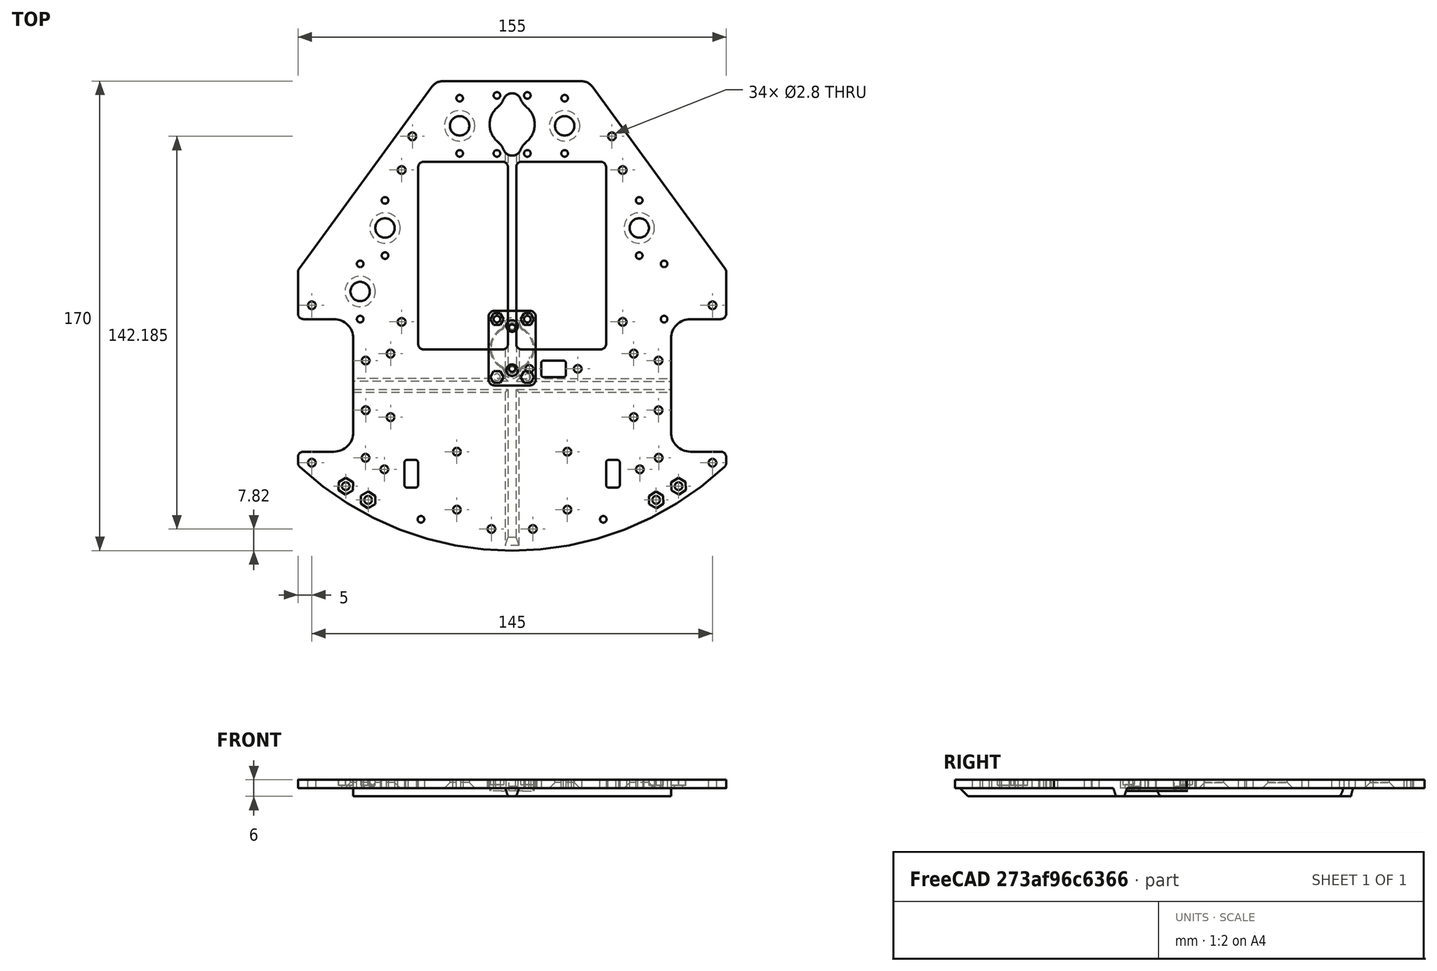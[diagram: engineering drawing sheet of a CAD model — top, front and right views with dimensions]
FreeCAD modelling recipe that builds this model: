
FCSTD DOCUMENT  (FreeCAD 0.19R24276 (Git))
Label: PB3D_TriPlate_Base
License: All rights reserved
LicenseURL: http://en.wikipedia.org/wiki/All_rights_reserved
objects: Sketcher::SketchObject×37, PartDesign::Pocket×23, PartDesign::Pad×5, PartDesign::Plane×5, PartDesign::SubtractiveLoft×4, PartDesign::Body×3, App::Part×3, Mesh::Feature×2, Spreadsheet::Sheet×1, PartDesign::Chamfer×1
note: 111 computed .brp shape members not serialized (recipe doc carries the construction recipe); baked Part::Feature solids carry a one-line shape summary decoded from their .brp

FEATURE [Sketcher::SketchObject] Sketch  label="Sketch_MainPlate"
  FullyConstrained = true
  MapMode = 5
  Support = -> [XY_Plane001]
  expr: Constraints[40] = <<params>>.plate_length
  expr: Constraints[65] = <<params>>.std_rad
  expr: Constraints[42] = <<params>>.tail_width
  expr: Constraints[78] = <<params>>.wheel_well_clearance
  expr: Constraints[79] = <<params>>.plate_width
  expr: Constraints[36] = <<params>>.wheel_well_plate_width
  expr: Constraints[47] = <<params>>.front_diameter
  expr: Constraints[63] = <<params>>.std_rad
  expr: Constraints[76] = <<params>>.front_vert_edge
  expr: Constraints[77] = <<params>>.back_vert_edge
  expr: Constraints[80] = <<params>>.std_rad
  expr: Constraints[81] = <<params>>.std_rad
  expr: Constraints[41] = <<params>>.tail_rad
  sketch-geometry (34):
    g0: LineSegment StartX=-57.5 StartY=17 StartZ=0 EndX=-57.5 EndY=-17 EndZ=0
    g1: LineSegment StartX=57.5 StartY=17 StartZ=0 EndX=57.5 EndY=-17 EndZ=0
    g2: LineSegment StartX=-57.5 StartY=0 StartZ=0 EndX=57.5 EndY=0 EndZ=0
    g3: LineSegment StartX=-64.5 StartY=-24 StartZ=0 EndX=64.5 EndY=-24 EndZ=0
    g4: LineSegment StartX=-64.5 StartY=24 StartZ=0 EndX=64.5 EndY=24 EndZ=0
    g5: LineSegment StartX=-64.5 StartY=-24 StartZ=0 EndX=-75.5 EndY=-24 EndZ=0
    g6: LineSegment StartX=64.5 StartY=-24 StartZ=0 EndX=75.5 EndY=-24 EndZ=0
    g7: ArcOfCircle CenterX=0 CenterY=52.6846 CenterZ=0 NormalX=0 NormalY=0 NormalZ=1 AngleXU=0 Radius=112.5 StartAngle=3.96017 EndAngle=5.4646
    g8: LineSegment StartX=-64.5 StartY=24 StartZ=0 EndX=-75.5 EndY=24 EndZ=0
    g9: LineSegment StartX=64.5 StartY=24 StartZ=0 EndX=75.5 EndY=24 EndZ=0
    g10: LineSegment StartX=-77.1162 StartY=42.1781 StartZ=0 EndX=-29.0404 EndY=108.13 EndZ=0
    g11: LineSegment StartX=-25 StartY=110.185 StartZ=0 EndX=25 EndY=110.185 EndZ=0
    g12: LineSegment StartX=29.0404 StartY=108.13 StartZ=0 EndX=77.1162 EndY=42.1781 EndZ=0
    g13: LineSegment StartX=0 StartY=0 StartZ=0 EndX=0 EndY=110.185 EndZ=0
    g14: ArcOfCircle CenterX=-25 CenterY=105.185 CenterZ=0 NormalX=0 NormalY=0 NormalZ=1 AngleXU=0 Radius=5 StartAngle=1.5708 EndAngle=2.5117
    g15: ArcOfCircle CenterX=25 CenterY=105.185 CenterZ=0 NormalX=0 NormalY=0 NormalZ=1 AngleXU=0 Radius=5 StartAngle=0.629894 EndAngle=1.5708
    g16: ArcOfCircle CenterX=-64.5 CenterY=17 CenterZ=0 NormalX=0 NormalY=0 NormalZ=1 AngleXU=0 Radius=7 StartAngle=0 EndAngle=1.5708
    g17: ArcOfCircle CenterX=-64.5 CenterY=-17 CenterZ=0 NormalX=0 NormalY=0 NormalZ=1 AngleXU=0 Radius=7 StartAngle=4.71239 EndAngle=6.28319
    g18: ArcOfCircle CenterX=64.5 CenterY=-17 CenterZ=0 NormalX=0 NormalY=0 NormalZ=1 AngleXU=0 Radius=7 StartAngle=3.14159 EndAngle=4.71239
    g19: ArcOfCircle CenterX=64.5 CenterY=17 CenterZ=0 NormalX=0 NormalY=0 NormalZ=1 AngleXU=0 Radius=7 StartAngle=1.5708 EndAngle=3.14159
    g20: GeomPoint X=0 Y=-59.8154 Z=0
    g21: Circle CenterX=0 CenterY=52.6846 CenterZ=0 NormalX=0 NormalY=0 NormalZ=1 AngleXU=0 Radius=112.5
    g22: LineSegment StartX=77.5 StartY=26 StartZ=0 EndX=77.5 EndY=41 EndZ=0
    g23: LineSegment StartX=77.5 StartY=-26 StartZ=0 EndX=77.5 EndY=-28 EndZ=0
    g24: LineSegment StartX=-77.5 StartY=-28 StartZ=0 EndX=-77.5 EndY=-26 EndZ=0
    g25: LineSegment StartX=-77.5 StartY=26 StartZ=0 EndX=-77.5 EndY=41 EndZ=0
    g26: ArcOfCircle CenterX=75.5 CenterY=-28 CenterZ=0 NormalX=0 NormalY=0 NormalZ=1 AngleXU=0 Radius=2 StartAngle=5.4646 EndAngle=6.28319
    g27: ArcOfCircle CenterX=75.5 CenterY=-26 CenterZ=0 NormalX=0 NormalY=0 NormalZ=1 AngleXU=0 Radius=2 StartAngle=-9e-16 EndAngle=1.5708
    g28: ArcOfCircle CenterX=-75.5 CenterY=-28 CenterZ=0 NormalX=0 NormalY=0 NormalZ=1 AngleXU=0 Radius=2 StartAngle=3.14159 EndAngle=3.96017
    g29: ArcOfCircle CenterX=-75.5 CenterY=-26 CenterZ=0 NormalX=0 NormalY=0 NormalZ=1 AngleXU=0 Radius=2 StartAngle=1.5708 EndAngle=3.14159
    g30: ArcOfCircle CenterX=75.5 CenterY=26 CenterZ=0 NormalX=0 NormalY=0 NormalZ=1 AngleXU=0 Radius=2 StartAngle=4.71239 EndAngle=6.28319
    g31: ArcOfCircle CenterX=75.5 CenterY=41 CenterZ=0 NormalX=0 NormalY=0 NormalZ=1 AngleXU=0 Radius=2 StartAngle=-7.1e-15 EndAngle=0.629894
    g32: ArcOfCircle CenterX=-75.5 CenterY=26 CenterZ=0 NormalX=0 NormalY=0 NormalZ=1 AngleXU=0 Radius=2 StartAngle=3.14159 EndAngle=4.71239
    g33: ArcOfCircle CenterX=-75.5 CenterY=41 CenterZ=0 NormalX=0 NormalY=0 NormalZ=1 AngleXU=0 Radius=2 StartAngle=2.5117 EndAngle=3.14159
  constraints (82):
    c: Vertical(g0)
    c: Vertical(g1)
    c: Horizontal(g2)
    c: Symmetric(g2,g2,g-1)
    c: Horizontal(g3)
    c: Horizontal(g5)
    c: Horizontal(g6)
    c: PointOnObject(g7,g-2)
    c: Horizontal(g8)
    c: Horizontal(g9)
    c: Horizontal(g11)
    c: Coincident(g13,g-1)
    c: PointOnObject(g13,g-2)
    c: Tangent(g10,g14) = 1.5708
    c: Tangent(g11,g14) = 1.5708
    c: Tangent(g11,g15) = 1.5708
    c: Tangent(g12,g15) = 1.5708
    c: Tangent(g8,g16) = -1.5708
    c: Tangent(g0,g16) = 1.5708
    c: Tangent(g5,g17) = 1.5708
    c: Tangent(g0,g17) = 1.5708
    c: Tangent(g1,g18) = -1.5708
    c: Tangent(g6,g18) = -1.5708
    c: Tangent(g1,g19) = -1.5708
    c: Tangent(g9,g19) = 1.5708
    c: Equal(g15,g14)
    c: Symmetric(g11,g11,g13)
    c: Equal(g18,g19)
    c: Equal(g19,g16)
    c: Equal(g16,g17)
    c: PointOnObject(g20,g-2)
    c: PointOnObject(g20,g7)
    c: Coincident(g4,g8)
    c: Coincident(g4,g9)
    c: Coincident(g3,g6)
    c: Coincident(g3,g5)
    c: DistanceX(g2,g2) = 115
    c: Symmetric(g0,g0,g2)
    c: Symmetric(g1,g1,g2)
    c: Radius(g19) = 7
    c: DistanceY(g20,g11) = 170
    c: Radius(g15) = 5
    c: DistanceX(g11,g11) = 50
    c: Equal(g9,g8)
    c: Equal(g9,g6)
    c: Coincident(g21,g7)
    c: PointOnObject(g20,g21)
    c: Diameter(g21) = 225
    c: Vertical(g22)
    c: Vertical(g23)
    c: Vertical(g24)
    c: Vertical(g25)
    c: Equal(g5,g8)
    c: Equal(g10,g12)
    c: Tangent(g7,g26) = -1.5708
    c: Tangent(g23,g26) = 1.5708
    c: Tangent(g23,g27) = 1.5708
    c: Tangent(g6,g27) = 1.5708
    c: Tangent(g7,g28) = -1.5708
    c: Tangent(g24,g28) = 1.5708
    c: Tangent(g24,g29) = 1.5708
    c: Tangent(g5,g29) = -1.5708
    c: Equal(g29,g27)
    c: Radius(g27) = 2
    c: Equal(g26,g28)
    c: Radius(g26) = 2
    c: Tangent(g9,g30) = -1.5708
    c: Tangent(g22,g30) = -1.5708
    c: Tangent(g22,g31) = -1.5708
    c: Tangent(g12,g31) = 1.5708
    c: Tangent(g8,g32) = 1.5708
    c: Tangent(g25,g32) = 1.5708
    c: Tangent(g10,g33) = 1.5708
    c: Tangent(g25,g33) = 1.5708
    c: Equal(g30,g32)
    c: Equal(g31,g33)
    c: DistanceY(g23,g23) = 2
    c: DistanceY(g22,g22) = 15
    c: DistanceY(g6,g9) = 48
    c: DistanceX(g24,g23) = 155
    c: Radius(g30) = 2
    c: Radius(g31) = 2
FEATURE [PartDesign::Pad] Pad  label="MainPlateExt"
  Direction = (1,1,1)
  Length = 6
  Length2 = 100
  Profile = -> Sketch
  Reversed = true
  Type = 0
  expr: Length = <<params>>.plate_thick + <<params>>.rib_thick
FEATURE [Spreadsheet::Sheet] Spreadsheet  label="params"
  cells = A1=Std Tol; B1(std_tol_clear)==0.3mm; A2=Bottom Plate Main Params; E2=Grove Board Mts; F2=X; G2=Y; I2=M2 Bolt Clearances; K2=M2.5 Bolt Clearances; A3=Plate Length; B3(plate_length)==170mm; C3=Mot Brac Hole Space L; D3(mot_brac_hole_space_l)==18mm; E3=LED 1; F3(grove_led_mood_x)==19mm; G3(grove_led_mood_y)==94mm; I3=Hole Clear Diam; J3(m2_hole_clear_diam)==2.4mm; K3=Hole Clear Diam; L3(m25_hole_clear_diam)==2.8mm; A4=Plate Width; B4(plate_width)==155mm; C4=Mot Brac Hole Space W; D4(mot_brac_hole_space_w)==wheel_well_plate_width - 2 * mot_brac_hole_offset_w; E4=LED 2; F4(grove_led_task_x)==46mm; G4(grove_led_task_y)==57mm; I4=Head Clear Diam; J4(m2_head_clear_diam)==4.2mm; K4=Head Clear Diam; L4(m25_head_clear_diam)==5mm; A5=Front Diameter; B5(front_diameter)==225mm; C5=Mot Brac Hole Offset W; D5(mot_brac_hole_offset_w)==4.5mm; E5=LSR/VIB; F5(grove_viblsr_x)==55mm; G5(grove_viblsr_y)==34mm; I5=Head Min Depth; J5(m2_head_min_depth)==1.3mm; K5=Head Min Depth; L5(m25_head_min_depth)==1.6mm; A6=Tail Width; B6(tail_width)==50mm; C6=Mot Ret Hole Space L; D6(mot_ret_hole_space_l)==23mm; I6=Nut Clear Flat; J6(m2_nut_clear_flat)==4.2mm; K6=Nut Clear Flat; L6(m25_nut_clear_flat)==5.2mm; A7=Plate Thickness; B7(plate_thick)==3mm; C7=Mot Ret Hole Space W; D7(mot_ret_hole_space_w)==wheel_well_plate_width - 2 * mot_ret_hole_offset_w; E7=BallCast Mt; G7=Shell Mts; I7=Nut Min Depth; J7(m2_nut_min_depth)==1.75mm; K7=Nut Min Depth; L7(m25_nut_min_depth)==2mm; C8=Mot Ret Hole Offset W; D8(mot_ret_hole_offset_w)==13.5mm; E8=BallC Mt L; F8(ballc_mt_l)==27mm; G8=ShellToBot FrMid Offset; H8(shelltobot_frontmid_offset_xy)==5mm; A9=Front Vert. Edge; B9(front_vert_edge)==2mm; E9=BallC Mt W; F9(ballc_mt_w)==17mm; G9=ShellToBot Back Offset X; H9(shelltobot_back_offset_x)==6mm; A10=Back Vert. Edge; B10(back_vert_edge)==15mm; E10=BallC Mt thick; F10(ballc_mt_t)==3mm; G10=ShellToBot Back Offset Y; H10(shelltobot_back_offset_y)==20mm; C11=BatB Cent Offset; D11(batb_cent_offset)==13mm; E11=BallC Mt Hole Space; F11(ballc_mt_holespace)==14.7mm; A12=Std. Radius; B12(std_rad)==2mm; C12=BatB Hole L; D12(batb_hole_l)==68mm; E12=BallC To Plate Offset; F12(ballc_to_plate_offset)==3mm; G12=US and LSR Mts; A13=Wheel Well Radius; B13(wheel_well_rad)==7mm; C13=BatB Hole W; D13(batb_hole_w)==64mm; E13=BallC To Plate L; F13(ballc_to_plate_l)==ballc_mt_l - 2 * ballc_to_plate_offset; G13=USR Mt Width; H13(usr_mt_width)==40mm; A14=Tail Radius; B14(tail_rad)==5mm; C14=BatB Mt L; D14(batb_mt_l)==55mm; E14=BallC To Plate W; F14(ballc_to_plate_w)==ballc_mt_w - 2 * ballc_to_plate_offset; G14=USR Mt Leng; H14(usr_mt_leng)==21mm; C15=BatB Mt W; D15(batb_mt_w)==80mm; E15=BallC Mt Thick Offset; F15(ballc_mt_thick_inset)==1mm; G15=USR Mt Loc X; H15(usr_mt_loc_x)==24mm; A16=Wheel Well Plate Width; B16(wheel_well_plate_width)==115mm; C16=BatB Mt Offset; D16(batb_mt_offset)==23mm; E16=BMPR Mts; G16=LSR Mt Width; H16(lsr_mt_width)==8mm; A17=Wheel Well Clearance; B17(wheel_well_clearance)==48mm; E17=BMPR Switch Hole Space; F17(bmpr_switch_hole_space)==9.5mm; G17=LSR Mt Diam Offset; H17(lsr_mt_diam_offset)==17.5mm; A18=Wheel Well Vert; B18(wheel_well_vert)==7mm; C18=Plate BallC Hole Loc L; D18(plate_ballc_hole_loc_l)==94.5mm; E18=BMPR Switch Diam Offset; F18(bmpr_switch_diam_offset)==5mm; G18=PWR Switch; E19=BMPR Switch Ang; F19(bmpr_switch_ang)=31.5; G19=PWR S Loc X; H19(pwrs_loc_x)==15mm; A20=Stiffeners; E20=BMPR Hole Diam; F20(bmpe_hole_diam)==3mm; G20=PWR S Loc Y; H20(pwrs_loc_y)==6mm; A21=Plate Rib Thickness; B21(rib_thick)==3mm; E21=BMPR Standoff Hole Width; F21(bmpr_standoff_hole_width)==66mm; G21=PWR S Slot Width; H21(pwrs_slot_w)==6mm; A22=Plate Rib Width Min; B22(rib_width_min)==3mm; E22=BMPR Standoff Hole Loc X; F22(bmpr_standoff_hole_loc_x)==48.5mm; G22=PWR S Slot Leng; H22(pwrs_slot_leng)==9mm; A23=Plate Rib Width Max; B23(rib_width_max)==5mm; E23=BMPR Pivot Hole Loc X; F23(bmpr_pivot_hole_loc_x)==52mm; G23=PWR S Slot Rad; H23(pwrs_slot_rad)==1mm; A24=Trim Front Rib Loc; B24(rib_trim_loc_front)==58mm; E24=BMPR Pivot Hole Spacing; F24(bmpr_pivot_hole_width)==15mm; G24=PWR S Hole Spacing; H24(pwrs_hole_spacing)==17.5mm; E26=BMPR Grove Hole Spacing Width; F26(bmpr_grove_hole_spacing_width)==68mm; E27=BMPR Grove Hole Loc X; F27(bmpr_grove_hole_loc_x)==32mm; E28=BMPR Grove Hole Width; F28(bmpr_grove_hole_width)==5mm; E29=BMPR Grove Hole Leng; F29(bmpr_grove_hole_leng)==10mm
FEATURE [Sketcher::SketchObject] Sketch016  label="Sketch_MainPlate_Temp"
  FullyConstrained = true
  MapMode = 5
  Support = -> [XY_Plane001]
  expr: Constraints[36] = <<params>>.tail_rad
  expr: Constraints[55] = <<params>>.std_rad
  expr: Constraints[70] = <<params>>.wheel_well_clearance
  expr: Constraints[68] = <<params>>.front_vert_edge
  expr: Constraints[72] = <<params>>.std_rad
  expr: Constraints[57] = <<params>>.std_rad
  expr: Constraints[73] = <<params>>.std_rad
  expr: Constraints[35] = <<params>>.plate_length
  expr: Constraints[37] = <<params>>.tail_width
  expr: Constraints[31] = <<params>>.wheel_well_plate_width
  expr: Constraints[71] = <<params>>.plate_width
  expr: Constraints[69] = <<params>>.back_vert_edge
  expr: Constraints[74] = <<params>>.front_diameter
  sketch-geometry (31):
    g0: LineSegment StartX=-57.5 StartY=17 StartZ=0 EndX=-57.5 EndY=-17 EndZ=0
    g1: LineSegment StartX=57.5 StartY=17 StartZ=0 EndX=57.5 EndY=-17 EndZ=0
    g2: LineSegment StartX=-57.5 StartY=0 StartZ=0 EndX=57.5 EndY=0 EndZ=0
    g3: LineSegment StartX=-64.5 StartY=-24 StartZ=0 EndX=-75.5 EndY=-24 EndZ=0
    g4: LineSegment StartX=64.5 StartY=-24 StartZ=0 EndX=75.5 EndY=-24 EndZ=0
    g5: ArcOfCircle CenterX=0 CenterY=52.6846 CenterZ=0 NormalX=0 NormalY=0 NormalZ=1 AngleXU=0 Radius=112.5 StartAngle=3.96017 EndAngle=5.4646
    g6: LineSegment StartX=-64.5 StartY=24 StartZ=0 EndX=-75.5 EndY=24 EndZ=0
    g7: LineSegment StartX=64.5 StartY=24 StartZ=0 EndX=75.5 EndY=24 EndZ=0
    g8: LineSegment StartX=-77.1162 StartY=42.1781 StartZ=0 EndX=-29.0404 EndY=108.13 EndZ=0
    g9: LineSegment StartX=-25 StartY=110.185 StartZ=0 EndX=25 EndY=110.185 EndZ=0
    g10: LineSegment StartX=29.0404 StartY=108.13 StartZ=0 EndX=77.1162 EndY=42.1781 EndZ=0
    g11: LineSegment StartX=0 StartY=0 StartZ=0 EndX=0 EndY=110.185 EndZ=0
    g12: ArcOfCircle CenterX=-25 CenterY=105.185 CenterZ=0 NormalX=0 NormalY=0 NormalZ=1 AngleXU=0 Radius=5 StartAngle=1.5708 EndAngle=2.5117
    g13: ArcOfCircle CenterX=25 CenterY=105.185 CenterZ=0 NormalX=0 NormalY=0 NormalZ=1 AngleXU=0 Radius=5 StartAngle=0.629894 EndAngle=1.5708
    g14: ArcOfCircle CenterX=-64.5 CenterY=17 CenterZ=0 NormalX=0 NormalY=0 NormalZ=1 AngleXU=0 Radius=7 StartAngle=0 EndAngle=1.5708
    g15: ArcOfCircle CenterX=-64.5 CenterY=-17 CenterZ=0 NormalX=0 NormalY=0 NormalZ=1 AngleXU=0 Radius=7 StartAngle=4.71239 EndAngle=6.28319
    g16: ArcOfCircle CenterX=64.5 CenterY=-17 CenterZ=0 NormalX=0 NormalY=0 NormalZ=1 AngleXU=0 Radius=7 StartAngle=3.14159 EndAngle=4.71239
    g17: ArcOfCircle CenterX=64.5 CenterY=17 CenterZ=0 NormalX=0 NormalY=0 NormalZ=1 AngleXU=0 Radius=7 StartAngle=1.5708 EndAngle=3.14159
    g18: GeomPoint X=0 Y=-59.8154 Z=0
    g19: LineSegment StartX=77.5 StartY=26 StartZ=0 EndX=77.5 EndY=41 EndZ=0
    g20: LineSegment StartX=77.5 StartY=-26 StartZ=0 EndX=77.5 EndY=-28 EndZ=0
    g21: LineSegment StartX=-77.5 StartY=-28 StartZ=0 EndX=-77.5 EndY=-26 EndZ=0
    g22: LineSegment StartX=-77.5 StartY=26 StartZ=0 EndX=-77.5 EndY=41 EndZ=0
    g23: ArcOfCircle CenterX=75.5 CenterY=-28 CenterZ=0 NormalX=0 NormalY=0 NormalZ=1 AngleXU=0 Radius=2 StartAngle=5.4646 EndAngle=6.28319
    g24: ArcOfCircle CenterX=75.5 CenterY=-26 CenterZ=0 NormalX=0 NormalY=0 NormalZ=1 AngleXU=0 Radius=2 StartAngle=-9e-16 EndAngle=1.5708
    g25: ArcOfCircle CenterX=-75.5 CenterY=-28 CenterZ=0 NormalX=0 NormalY=0 NormalZ=1 AngleXU=0 Radius=2 StartAngle=3.14159 EndAngle=3.96017
    g26: ArcOfCircle CenterX=-75.5 CenterY=-26 CenterZ=0 NormalX=0 NormalY=0 NormalZ=1 AngleXU=0 Radius=2 StartAngle=1.5708 EndAngle=3.14159
    g27: ArcOfCircle CenterX=75.5 CenterY=26 CenterZ=0 NormalX=0 NormalY=0 NormalZ=1 AngleXU=0 Radius=2 StartAngle=4.71239 EndAngle=6.28319
    g28: ArcOfCircle CenterX=75.5 CenterY=41 CenterZ=0 NormalX=0 NormalY=0 NormalZ=1 AngleXU=0 Radius=2 StartAngle=-7.1e-15 EndAngle=0.629894
    g29: ArcOfCircle CenterX=-75.5 CenterY=26 CenterZ=0 NormalX=0 NormalY=0 NormalZ=1 AngleXU=0 Radius=2 StartAngle=3.14159 EndAngle=4.71239
    g30: ArcOfCircle CenterX=-75.5 CenterY=41 CenterZ=0 NormalX=0 NormalY=0 NormalZ=1 AngleXU=0 Radius=2 StartAngle=2.5117 EndAngle=3.14159
  constraints (76):
    c: Vertical(g0)
    c: Vertical(g1)
    c: Horizontal(g2)
    c: Symmetric(g2,g2,g-1)
    c: Horizontal(g3)
    c: Horizontal(g4)
    c: PointOnObject(g5,g-2)
    c: Horizontal(g6)
    c: Horizontal(g7)
    c: Horizontal(g9)
    c: Coincident(g11,g-1)
    c: PointOnObject(g11,g-2)
    c: Tangent(g8,g12) = 1.5708
    c: Tangent(g9,g12) = 1.5708
    c: Tangent(g9,g13) = 1.5708
    c: Tangent(g10,g13) = 1.5708
    c: Tangent(g6,g14) = -1.5708
    c: Tangent(g0,g14) = 1.5708
    c: Tangent(g3,g15) = 1.5708
    c: Tangent(g0,g15) = 1.5708
    c: Tangent(g1,g16) = -1.5708
    c: Tangent(g4,g16) = -1.5708
    c: Tangent(g1,g17) = -1.5708
    c: Tangent(g7,g17) = 1.5708
    c: Equal(g13,g12)
    c: Symmetric(g9,g9,g11)
    c: Equal(g16,g17)
    c: Equal(g17,g14)
    c: Equal(g14,g15)
    c: PointOnObject(g18,g-2)
    c: PointOnObject(g18,g5)
    c: DistanceX(g2,g2) = 115
    c: Symmetric(g0,g0,g2)
    c: Symmetric(g1,g1,g2)
    c: Radius(g17) = 7
    c: DistanceY(g18,g9) = 170
    c: Radius(g13) = 5
    c: DistanceX(g9,g9) = 50
    c: Equal(g7,g6)
    c: Equal(g7,g4)
    c: Vertical(g19)
    c: Vertical(g20)
    c: Vertical(g21)
    c: Vertical(g22)
    c: Equal(g3,g6)
    c: Equal(g8,g10)
    c: Tangent(g5,g23) = -1.5708
    c: Tangent(g20,g23) = 1.5708
    c: Tangent(g20,g24) = 1.5708
    c: Tangent(g4,g24) = 1.5708
    c: Tangent(g5,g25) = -1.5708
    c: Tangent(g21,g25) = 1.5708
    c: Tangent(g21,g26) = 1.5708
    c: Tangent(g3,g26) = -1.5708
    c: Equal(g26,g24)
    c: Radius(g24) = 2
    c: Equal(g23,g25)
    c: Radius(g23) = 2
    c: Tangent(g7,g27) = -1.5708
    c: Tangent(g19,g27) = -1.5708
    c: Tangent(g19,g28) = -1.5708
    c: Tangent(g10,g28) = 1.5708
    c: Tangent(g6,g29) = 1.5708
    c: Tangent(g22,g29) = 1.5708
    c: Tangent(g8,g30) = 1.5708
    c: Tangent(g22,g30) = 1.5708
    c: Equal(g27,g29)
    c: Equal(g28,g30)
    c: DistanceY(g20,g20) = 2
    c: DistanceY(g19,g19) = 15
    c: DistanceY(g4,g7) = 48
    c: DistanceX(g21,g20) = 155
    c: Radius(g27) = 2
    c: Radius(g28) = 2
    c: Diameter(g5) = 225
    c: Equal(g21,g20)
FEATURE [Sketcher::SketchObject] Sketch017  label="Sketch_BatBoxCut"
  FullyConstrained = true
  MapMode = 5
  Support = -> [XY_Plane001]
  expr: Constraints[121] = Spreadsheet.rib_width_min
  expr: Constraints[87] = <<params>>.std_rad
  expr: Constraints[71] = <<params>>.plate_width
  expr: Constraints[69] = <<params>>.back_vert_edge
  expr: Constraints[120] = <<params>>.batb_hole_l
  expr: Constraints[72] = <<params>>.std_rad
  expr: Constraints[57] = <<params>>.std_rad
  expr: Constraints[37] = <<params>>.tail_width
  expr: Constraints[88] = <<params>>.batb_hole_w
  expr: Constraints[35] = <<params>>.plate_length
  expr: Constraints[89] = <<params>>.batb_cent_offset
  expr: Constraints[74] = <<params>>.front_diameter
  expr: Constraints[31] = <<params>>.wheel_well_plate_width
  expr: Constraints[73] = <<params>>.std_rad
  expr: Constraints[68] = <<params>>.front_vert_edge
  expr: Constraints[70] = <<params>>.wheel_well_clearance
  expr: Constraints[55] = <<params>>.std_rad
  expr: Constraints[36] = <<params>>.tail_rad
  sketch-geometry (50):
    g0: LineSegment StartX=-57.5 StartY=17 StartZ=0 EndX=-57.5 EndY=-17 EndZ=0
    g1: LineSegment StartX=57.5 StartY=17 StartZ=0 EndX=57.5 EndY=-17 EndZ=0
    g2: LineSegment StartX=-57.5 StartY=0 StartZ=0 EndX=57.5 EndY=0 EndZ=0
    g3: LineSegment StartX=-64.5 StartY=-24 StartZ=0 EndX=-75.5 EndY=-24 EndZ=0
    g4: LineSegment StartX=64.5 StartY=-24 StartZ=0 EndX=75.5 EndY=-24 EndZ=0
    g5: ArcOfCircle CenterX=0 CenterY=52.6846 CenterZ=0 NormalX=0 NormalY=0 NormalZ=1 AngleXU=0 Radius=112.5 StartAngle=3.96017 EndAngle=5.4646
    g6: LineSegment StartX=-64.5 StartY=24 StartZ=0 EndX=-75.5 EndY=24 EndZ=0
    g7: LineSegment StartX=64.5 StartY=24 StartZ=0 EndX=75.5 EndY=24 EndZ=0
    g8: LineSegment StartX=-77.1162 StartY=42.1781 StartZ=0 EndX=-29.0404 EndY=108.13 EndZ=0
    g9: LineSegment StartX=-25 StartY=110.185 StartZ=0 EndX=25 EndY=110.185 EndZ=0
    g10: LineSegment StartX=29.0404 StartY=108.13 StartZ=0 EndX=77.1162 EndY=42.1781 EndZ=0
    g11: LineSegment StartX=0 StartY=0 StartZ=0 EndX=0 EndY=110.185 EndZ=0
    g12: ArcOfCircle CenterX=-25 CenterY=105.185 CenterZ=0 NormalX=0 NormalY=0 NormalZ=1 AngleXU=0 Radius=5 StartAngle=1.5708 EndAngle=2.5117
    g13: ArcOfCircle CenterX=25 CenterY=105.185 CenterZ=0 NormalX=0 NormalY=0 NormalZ=1 AngleXU=0 Radius=5 StartAngle=0.629894 EndAngle=1.5708
    g14: ArcOfCircle CenterX=-64.5 CenterY=17 CenterZ=0 NormalX=0 NormalY=0 NormalZ=1 AngleXU=0 Radius=7 StartAngle=0 EndAngle=1.5708
    g15: ArcOfCircle CenterX=-64.5 CenterY=-17 CenterZ=0 NormalX=0 NormalY=0 NormalZ=1 AngleXU=0 Radius=7 StartAngle=4.71239 EndAngle=6.28319
    g16: ArcOfCircle CenterX=64.5 CenterY=-17 CenterZ=0 NormalX=0 NormalY=0 NormalZ=1 AngleXU=0 Radius=7 StartAngle=3.14159 EndAngle=4.71239
    g17: ArcOfCircle CenterX=64.5 CenterY=17 CenterZ=0 NormalX=0 NormalY=0 NormalZ=1 AngleXU=0 Radius=7 StartAngle=1.5708 EndAngle=3.14159
    g18: GeomPoint X=0 Y=-59.8154 Z=0
    g19: LineSegment StartX=77.5 StartY=26 StartZ=0 EndX=77.5 EndY=41 EndZ=0
    g20: LineSegment StartX=77.5 StartY=-26 StartZ=0 EndX=77.5 EndY=-28 EndZ=0
    g21: LineSegment StartX=-77.5 StartY=-28 StartZ=0 EndX=-77.5 EndY=-26 EndZ=0
    g22: LineSegment StartX=-77.5 StartY=26 StartZ=0 EndX=-77.5 EndY=41 EndZ=0
    g23: ArcOfCircle CenterX=75.5 CenterY=-28 CenterZ=0 NormalX=0 NormalY=0 NormalZ=1 AngleXU=0 Radius=2 StartAngle=5.4646 EndAngle=6.28319
    g24: ArcOfCircle CenterX=75.5 CenterY=-26 CenterZ=0 NormalX=0 NormalY=0 NormalZ=1 AngleXU=0 Radius=2 StartAngle=-9e-16 EndAngle=1.5708
    g25: ArcOfCircle CenterX=-75.5 CenterY=-28 CenterZ=0 NormalX=0 NormalY=0 NormalZ=1 AngleXU=0 Radius=2 StartAngle=3.14159 EndAngle=3.96017
    g26: ArcOfCircle CenterX=-75.5 CenterY=-26 CenterZ=0 NormalX=0 NormalY=0 NormalZ=1 AngleXU=0 Radius=2 StartAngle=1.5708 EndAngle=3.14159
    g27: ArcOfCircle CenterX=75.5 CenterY=26 CenterZ=0 NormalX=0 NormalY=0 NormalZ=1 AngleXU=0 Radius=2 StartAngle=4.71239 EndAngle=6.28319
    g28: ArcOfCircle CenterX=75.5 CenterY=41 CenterZ=0 NormalX=0 NormalY=0 NormalZ=1 AngleXU=0 Radius=2 StartAngle=-9e-16 EndAngle=0.629894
    g29: ArcOfCircle CenterX=-75.5 CenterY=26 CenterZ=0 NormalX=0 NormalY=0 NormalZ=1 AngleXU=0 Radius=2 StartAngle=3.14159 EndAngle=4.71239
    g30: ArcOfCircle CenterX=-75.5 CenterY=41 CenterZ=0 NormalX=0 NormalY=0 NormalZ=1 AngleXU=0 Radius=2 StartAngle=2.5117 EndAngle=3.14159
    g31: LineSegment StartX=34 StartY=79 StartZ=0 EndX=34 EndY=15 EndZ=0
    g32: LineSegment StartX=-34 StartY=15 StartZ=0 EndX=-34 EndY=79 EndZ=0
    g33: LineSegment StartX=0 StartY=0 StartZ=0 EndX=0 EndY=13 EndZ=0
    g34: ArcOfCircle CenterX=-32 CenterY=15 CenterZ=0 NormalX=0 NormalY=0 NormalZ=1 AngleXU=0 Radius=2 StartAngle=3.14159 EndAngle=4.71239
    g35: ArcOfCircle CenterX=32 CenterY=15 CenterZ=0 NormalX=0 NormalY=0 NormalZ=1 AngleXU=0 Radius=2 StartAngle=4.71239 EndAngle=6.28319
    g36: ArcOfCircle CenterX=32 CenterY=79 CenterZ=0 NormalX=0 NormalY=0 NormalZ=1 AngleXU=0 Radius=2 StartAngle=1.7e-15 EndAngle=1.5708
    g37: ArcOfCircle CenterX=-32 CenterY=79 CenterZ=0 NormalX=0 NormalY=0 NormalZ=1 AngleXU=0 Radius=2 StartAngle=1.5708 EndAngle=3.14159
    g38: LineSegment StartX=-32 StartY=81 StartZ=0 EndX=-3.5 EndY=81 EndZ=0
    g39: LineSegment StartX=-1.5 StartY=79 StartZ=0 EndX=-1.5 EndY=15 EndZ=0
    g40: LineSegment StartX=-3.5 StartY=13 StartZ=0 EndX=-32 EndY=13 EndZ=0
    g41: LineSegment StartX=32 StartY=81 StartZ=0 EndX=3.5 EndY=81 EndZ=0
    g42: LineSegment StartX=1.5 StartY=79 StartZ=0 EndX=1.5 EndY=15 EndZ=0
    g43: LineSegment StartX=3.5 StartY=13 StartZ=0 EndX=32 EndY=13 EndZ=0
    g44: ArcOfCircle CenterX=-3.5 CenterY=79 CenterZ=0 NormalX=0 NormalY=0 NormalZ=1 AngleXU=0 Radius=2 StartAngle=-1.8e-15 EndAngle=1.5708
    g45: ArcOfCircle CenterX=3.5 CenterY=79 CenterZ=0 NormalX=0 NormalY=0 NormalZ=1 AngleXU=0 Radius=2 StartAngle=1.5708 EndAngle=3.14159
    g46: ArcOfCircle CenterX=3.5 CenterY=15 CenterZ=0 NormalX=0 NormalY=0 NormalZ=1 AngleXU=0 Radius=2 StartAngle=3.14159 EndAngle=4.71239
    g47: ArcOfCircle CenterX=-3.5 CenterY=15 CenterZ=0 NormalX=0 NormalY=0 NormalZ=1 AngleXU=0 Radius=2 StartAngle=4.71239 EndAngle=6.28319
    g48: LineSegment StartX=-3.5 StartY=79 StartZ=0 EndX=3.5 EndY=79 EndZ=0
    g49: LineSegment StartX=-3.5 StartY=15 StartZ=0 EndX=3.5 EndY=15 EndZ=0
  constraints (126):
    c: Vertical(g0)
    c: Vertical(g1)
    c: Horizontal(g2)
    c: Symmetric(g2,g2,g-1)
    c: Horizontal(g3)
    c: Horizontal(g4)
    c: PointOnObject(g5,g-2)
    c: Horizontal(g6)
    c: Horizontal(g7)
    c: Horizontal(g9)
    c: Coincident(g11,g-1)
    c: PointOnObject(g11,g-2)
    c: Tangent(g8,g12) = 1.5708
    c: Tangent(g9,g12) = 1.5708
    c: Tangent(g9,g13) = 1.5708
    c: Tangent(g10,g13) = 1.5708
    c: Tangent(g6,g14) = -1.5708
    c: Tangent(g0,g14) = 1.5708
    c: Tangent(g3,g15) = 1.5708
    c: Tangent(g0,g15) = 1.5708
    c: Tangent(g1,g16) = -1.5708
    c: Tangent(g4,g16) = -1.5708
    c: Tangent(g1,g17) = -1.5708
    c: Tangent(g7,g17) = 1.5708
    c: Equal(g13,g12)
    c: Symmetric(g9,g9,g11)
    c: Equal(g16,g17)
    c: Equal(g17,g14)
    c: Equal(g14,g15)
    c: PointOnObject(g18,g-2)
    c: PointOnObject(g18,g5)
    c: DistanceX(g2,g2) = 115
    c: Symmetric(g0,g0,g2)
    c: Symmetric(g1,g1,g2)
    c: Radius(g17) = 7
    c: DistanceY(g18,g9) = 170
    c: Radius(g13) = 5
    c: DistanceX(g9,g9) = 50
    c: Equal(g7,g6)
    c: Equal(g7,g4)
    c: Vertical(g19)
    c: Vertical(g20)
    c: Vertical(g21)
    c: Vertical(g22)
    c: Equal(g3,g6)
    c: Equal(g8,g10)
    c: Tangent(g5,g23) = -1.5708
    c: Tangent(g20,g23) = 1.5708
    c: Tangent(g20,g24) = 1.5708
    c: Tangent(g4,g24) = 1.5708
    c: Tangent(g5,g25) = -1.5708
    c: Tangent(g21,g25) = 1.5708
    c: Tangent(g21,g26) = 1.5708
    c: Tangent(g3,g26) = -1.5708
    c: Equal(g26,g24)
    c: Radius(g24) = 2
    c: Equal(g23,g25)
    c: Radius(g23) = 2
    c: Tangent(g7,g27) = -1.5708
    c: Tangent(g19,g27) = -1.5708
    c: Tangent(g19,g28) = -1.5708
    c: Tangent(g10,g28) = 1.5708
    c: Tangent(g6,g29) = 1.5708
    c: Tangent(g22,g29) = 1.5708
    c: Tangent(g8,g30) = 1.5708
    c: Tangent(g22,g30) = 1.5708
    c: Equal(g27,g29)
    c: Equal(g28,g30)
    c: DistanceY(g20,g20) = 2
    c: DistanceY(g19,g19) = 15
    c: DistanceY(g4,g7) = 48
    c: DistanceX(g21,g20) = 155
    c: Radius(g27) = 2
    c: Radius(g28) = 2
    c: Diameter(g5) = 225
    c: Equal(g21,g20)
    c: Vertical(g31)
    c: Vertical(g32)
    c: Coincident(g33,g11)
    c: Vertical(g33)
    c: Tangent(g32,g34) = 1.5708
    c: Tangent(g31,g35) = 1.5708
    c: Tangent(g31,g36) = 1.5708
    c: Tangent(g32,g37) = 1.5708
    c: Equal(g36,g37)
    c: Equal(g37,g34)
    c: Equal(g34,g35)
    c: Radius(g35) = 2
    c: DistanceX(g37,g36) = 64
    c: DistanceY(g-1,g33) = 13
    c: Coincident(g38,g37)
    c: Horizontal(g38)
    c: Vertical(g39)
    c: Coincident(g40,g34)
    c: Horizontal(g40)
    c: Coincident(g41,g36)
    c: Horizontal(g41)
    c: Vertical(g42)
    c: Coincident(g43,g35)
    c: Horizontal(g43)
    c: Tangent(g38,g44) = 1.5708
    c: Tangent(g39,g44) = 1.5708
    c: Tangent(g42,g45) = -1.5708
    c: Tangent(g41,g45) = -1.5708
    c: Tangent(g42,g46) = -1.5708
    c: Tangent(g43,g46) = -1.5708
    c: Tangent(g39,g47) = 1.5708
    c: Tangent(g40,g47) = 1.5708
    c: Coincident(g48,g44)
    c: Coincident(g48,g45)
    c: Coincident(g49,g47)
    c: Coincident(g49,g46)
    c: Horizontal(g49)
    c: Horizontal(g48)
    c: Equal(g36,g45)
    c: Equal(g45,g44)
    c: Equal(g46,g47)
    c: Equal(g43,g40)
    c: Equal(g35,g46)
    c: Symmetric(g34,g35,g33)
    c: DistanceY(g35,g36) = 68
    c: DistanceX(g39,g42) = 3
    c: Tangent(g40,g34)
    c: Tangent(g43,g35)
    c: Tangent(g36,g41)
    c: Tangent(g37,g38)
FEATURE [PartDesign::Pocket] Pocket003  label="BatBoxCut"
  BaseFeature = -> Pad
  Length = 5
  Length2 = 100
  Profile = -> Sketch017
  Type = 1
FEATURE [Sketcher::SketchObject] Sketch018  label="Sketch_MotBrackHoles"
  FullyConstrained = true
  MapMode = 5
  Support = -> [XY_Plane001]
  expr: Constraints[9] = <<params>>.mot_brac_hole_space_l
  expr: Constraints[10] = <<params>>.mot_brac_hole_space_w
  expr: Constraints[18] = <<params>>.m25_hole_clear_diam
  sketch-geometry (8):
    g0: LineSegment StartX=-53 StartY=9 StartZ=0 EndX=53 EndY=9 EndZ=0
    g1: LineSegment StartX=53 StartY=9 StartZ=0 EndX=53 EndY=-9 EndZ=0
    g2: LineSegment StartX=53 StartY=-9 StartZ=0 EndX=-53 EndY=-9 EndZ=0
    g3: LineSegment StartX=-53 StartY=-9 StartZ=0 EndX=-53 EndY=9 EndZ=0
    g4: Circle CenterX=53 CenterY=9 CenterZ=0 NormalX=0 NormalY=0 NormalZ=1 AngleXU=0 Radius=1.4
    g5: Circle CenterX=53 CenterY=-9 CenterZ=0 NormalX=0 NormalY=0 NormalZ=1 AngleXU=0 Radius=1.4
    g6: Circle CenterX=-53 CenterY=-9 CenterZ=0 NormalX=0 NormalY=0 NormalZ=1 AngleXU=0 Radius=1.4
    g7: Circle CenterX=-53 CenterY=9 CenterZ=0 NormalX=0 NormalY=0 NormalZ=1 AngleXU=0 Radius=1.4
  constraints (19):
    c: Coincident(g0,g1)
    c: Coincident(g1,g2)
    c: Coincident(g2,g3)
    c: Coincident(g3,g0)
    c: Horizontal(g0)
    c: Horizontal(g2)
    c: Vertical(g1)
    c: Vertical(g3)
    c: Symmetric(g2,g0,g-1)
    c: DistanceY(g1,g0) = 18
    c: DistanceX(g0,g0) = 106
    c: Coincident(g4,g0)
    c: Coincident(g5,g1)
    c: Coincident(g6,g2)
    c: Coincident(g7,g0)
    c: Equal(g7,g4)
    c: Equal(g4,g5)
    c: Equal(g5,g6)
    c: Diameter(g5) = 2.8
FEATURE [PartDesign::Pocket] Pocket  label="MotBracketHoles"
  BaseFeature = -> Pocket003
  Length = 5
  Length2 = 100
  Midplane = true
  Profile = -> Sketch018
  Type = 1
FEATURE [Sketcher::SketchObject] Sketch019  label="Sketch_MotRetHoles"
  FullyConstrained = true
  MapMode = 5
  Support = -> [XY_Plane001]
  expr: Constraints[9] = <<params>>.mot_ret_hole_space_l
  expr: Constraints[18] = <<params>>.m25_hole_clear_diam
  expr: Constraints[10] = <<params>>.mot_ret_hole_space_w
  sketch-geometry (8):
    g0: LineSegment StartX=-44 StartY=11.5 StartZ=0 EndX=44 EndY=11.5 EndZ=0
    g1: LineSegment StartX=44 StartY=11.5 StartZ=0 EndX=44 EndY=-11.5 EndZ=0
    g2: LineSegment StartX=44 StartY=-11.5 StartZ=0 EndX=-44 EndY=-11.5 EndZ=0
    g3: LineSegment StartX=-44 StartY=-11.5 StartZ=0 EndX=-44 EndY=11.5 EndZ=0
    g4: Circle CenterX=-44 CenterY=11.5 CenterZ=0 NormalX=0 NormalY=0 NormalZ=1 AngleXU=0 Radius=1.4
    g5: Circle CenterX=44 CenterY=11.5 CenterZ=0 NormalX=0 NormalY=0 NormalZ=1 AngleXU=0 Radius=1.4
    g6: Circle CenterX=44 CenterY=-11.5 CenterZ=0 NormalX=0 NormalY=0 NormalZ=1 AngleXU=0 Radius=1.4
    g7: Circle CenterX=-44 CenterY=-11.5 CenterZ=0 NormalX=0 NormalY=0 NormalZ=1 AngleXU=0 Radius=1.4
  constraints (19):
    c: Coincident(g0,g1)
    c: Coincident(g1,g2)
    c: Coincident(g2,g3)
    c: Coincident(g3,g0)
    c: Horizontal(g0)
    c: Horizontal(g2)
    c: Vertical(g1)
    c: Vertical(g3)
    c: Symmetric(g0,g2,g-1)
    c: DistanceY(g1,g0) = 23
    c: DistanceX(g0,g0) = 88
    c: Coincident(g4,g0)
    c: Coincident(g5,g0)
    c: Coincident(g6,g1)
    c: Coincident(g7,g2)
    c: Equal(g4,g5)
    c: Equal(g5,g6)
    c: Equal(g6,g7)
    c: Diameter(g6) = 2.8
FEATURE [PartDesign::Pocket] Pocket004  label="MotWireRetHoles"
  BaseFeature = -> Pocket
  Length = 5
  Length2 = 100
  Midplane = true
  Profile = -> Sketch019
  Type = 1
FEATURE [Sketcher::SketchObject] Sketch020  label="Sketch_BatBMtHoles"
  FullyConstrained = true
  MapMode = 5
  Support = -> [XY_Plane001]
  expr: Constraints[11] = <<params>>.batb_mt_l
  expr: Constraints[12] = <<params>>.batb_mt_w
  expr: Constraints[13] = <<params>>.batb_mt_offset
  expr: Constraints[21] = <<params>>.m25_hole_clear_diam
  sketch-geometry (9):
    g0: LineSegment StartX=-40 StartY=78 StartZ=0 EndX=40 EndY=78 EndZ=0
    g1: LineSegment StartX=40 StartY=78 StartZ=0 EndX=40 EndY=23 EndZ=0
    g2: LineSegment StartX=40 StartY=23 StartZ=0 EndX=-40 EndY=23 EndZ=0
    g3: LineSegment StartX=-40 StartY=23 StartZ=0 EndX=-40 EndY=78 EndZ=0
    g4: LineSegment StartX=0 StartY=0 StartZ=0 EndX=0 EndY=23 EndZ=0
    g5: Circle CenterX=40 CenterY=78 CenterZ=0 NormalX=0 NormalY=0 NormalZ=1 AngleXU=0 Radius=1.4
    g6: Circle CenterX=40 CenterY=23 CenterZ=0 NormalX=0 NormalY=0 NormalZ=1 AngleXU=0 Radius=1.4
    g7: Circle CenterX=-40 CenterY=23 CenterZ=0 NormalX=0 NormalY=0 NormalZ=1 AngleXU=0 Radius=1.4
    g8: Circle CenterX=-40 CenterY=78 CenterZ=0 NormalX=0 NormalY=0 NormalZ=1 AngleXU=0 Radius=1.4
  constraints (22):
    c: Coincident(g0,g1)
    c: Coincident(g1,g2)
    c: Coincident(g2,g3)
    c: Coincident(g3,g0)
    c: Horizontal(g0)
    c: Horizontal(g2)
    c: Vertical(g1)
    c: Vertical(g3)
    c: Coincident(g4,g-1)
    c: PointOnObject(g4,g-2)
    c: Symmetric(g2,g1,g4)
    c: DistanceY(g1,g0) = 55
    c: DistanceX(g0,g0) = 80
    c: DistanceY(g-1,g4) = 23
    c: Coincident(g5,g0)
    c: Coincident(g6,g1)
    c: Coincident(g7,g2)
    c: Coincident(g8,g0)
    c: Equal(g8,g5)
    c: Equal(g5,g6)
    c: Equal(g6,g7)
    c: Diameter(g6) = 2.8
FEATURE [PartDesign::Pocket] Pocket005  label="BatBMtHoles"
  BaseFeature = -> Pocket004
  Length = 5
  Length2 = 100
  Midplane = true
  Profile = -> Sketch020
  Type = 1
FEATURE [Sketcher::SketchObject] Sketch021  label="Sketch_GroveMts"
  FullyConstrained = true
  MapMode = 5
  Support = -> [XY_Plane001]
  expr: Constraints[15] = <<params>>.grove_led_mood_y
  expr: Constraints[20] = <<params>>.grove_viblsr_y
  expr: Constraints[16] = <<params>>.grove_led_mood_x
  expr: Constraints[17] = <<params>>.grove_led_task_y
  expr: Constraints[18] = <<params>>.grove_led_task_x
  expr: Constraints[19] = <<params>>.grove_viblsr_x
  expr: Constraints[32] = <<params>>.m2_hole_clear_diam
  sketch-geometry (35):
    g0: LineSegment StartX=46 StartY=67 StartZ=0 EndX=46 EndY=57 EndZ=0
    g1: LineSegment StartX=46 StartY=57 StartZ=0 EndX=46 EndY=47 EndZ=0
    g2: LineSegment StartX=55 StartY=44 StartZ=0 EndX=55 EndY=34 EndZ=0
    g3: LineSegment StartX=55 StartY=34 StartZ=0 EndX=55 EndY=24 EndZ=0
    g4: LineSegment StartX=19 StartY=104 StartZ=0 EndX=19 EndY=94 EndZ=0
    g5: LineSegment StartX=19 StartY=94 StartZ=0 EndX=19 EndY=84 EndZ=0
    g6: Circle CenterX=19 CenterY=84 CenterZ=0 NormalX=0 NormalY=0 NormalZ=1 AngleXU=0 Radius=1.2
    g7: Circle CenterX=19 CenterY=104 CenterZ=0 NormalX=0 NormalY=0 NormalZ=1 AngleXU=0 Radius=1.2
    g8: Circle CenterX=46 CenterY=47 CenterZ=0 NormalX=0 NormalY=0 NormalZ=1 AngleXU=0 Radius=1.2
    g9: Circle CenterX=46 CenterY=67 CenterZ=0 NormalX=0 NormalY=0 NormalZ=1 AngleXU=0 Radius=1.2
    g10: Circle CenterX=55 CenterY=24 CenterZ=0 NormalX=0 NormalY=0 NormalZ=1 AngleXU=0 Radius=1.2
    g11: Circle CenterX=55 CenterY=44 CenterZ=0 NormalX=0 NormalY=0 NormalZ=1 AngleXU=0 Radius=1.2
    g12: Circle CenterX=19 CenterY=94 CenterZ=0 NormalX=0 NormalY=0 NormalZ=1 AngleXU=0 Radius=3.5
    g13: Circle CenterX=46 CenterY=57 CenterZ=0 NormalX=0 NormalY=0 NormalZ=1 AngleXU=0 Radius=3.5
    g14: LineSegment StartX=-19 StartY=104 StartZ=0 EndX=-19 EndY=94 EndZ=0
    g15: LineSegment StartX=-19 StartY=94 StartZ=0 EndX=-19 EndY=84 EndZ=0
    g16: LineSegment StartX=-46 StartY=67 StartZ=0 EndX=-46 EndY=57 EndZ=0
    g17: LineSegment StartX=-46 StartY=57 StartZ=0 EndX=-46 EndY=47 EndZ=0
    g18: LineSegment StartX=-55 StartY=44 StartZ=0 EndX=-55 EndY=34 EndZ=0
    g19: LineSegment StartX=-55 StartY=34 StartZ=0 EndX=-55 EndY=24 EndZ=0
    g20: LineSegment StartX=-55 StartY=34 StartZ=0 EndX=55 EndY=34 EndZ=0
    g21: LineSegment StartX=-46 StartY=57 StartZ=0 EndX=46 EndY=57 EndZ=0
    g22: LineSegment StartX=-19 StartY=94 StartZ=0 EndX=19 EndY=94 EndZ=0
    g23: LineSegment StartX=0 StartY=0 StartZ=0 EndX=0 EndY=34 EndZ=0
    g24: LineSegment StartX=0 StartY=0 StartZ=0 EndX=0 EndY=57 EndZ=0
    g25: LineSegment StartX=0 StartY=0 StartZ=0 EndX=0 EndY=94 EndZ=0
    g26: Circle CenterX=-19 CenterY=104 CenterZ=0 NormalX=0 NormalY=0 NormalZ=1 AngleXU=0 Radius=1.2
    g27: Circle CenterX=-19 CenterY=84 CenterZ=0 NormalX=0 NormalY=0 NormalZ=1 AngleXU=0 Radius=1.2
    g28: Circle CenterX=-46 CenterY=67 CenterZ=0 NormalX=0 NormalY=0 NormalZ=1 AngleXU=0 Radius=1.2
    g29: Circle CenterX=-19 CenterY=94 CenterZ=0 NormalX=0 NormalY=0 NormalZ=1 AngleXU=0 Radius=3.5
    g30: Circle CenterX=-46 CenterY=57 CenterZ=0 NormalX=0 NormalY=0 NormalZ=1 AngleXU=0 Radius=3.5
    g31: Circle CenterX=-55 CenterY=34 CenterZ=0 NormalX=0 NormalY=0 NormalZ=1 AngleXU=0 Radius=3.5
    g32: Circle CenterX=-46 CenterY=47 CenterZ=0 NormalX=0 NormalY=0 NormalZ=1 AngleXU=0 Radius=1.2
    g33: Circle CenterX=-55 CenterY=44 CenterZ=0 NormalX=0 NormalY=0 NormalZ=1 AngleXU=0 Radius=1.2
    g34: Circle CenterX=-55 CenterY=24 CenterZ=0 NormalX=0 NormalY=0 NormalZ=1 AngleXU=0 Radius=1.2
  constraints (88):
    c: Vertical(g0)
    c: Coincident(g1,g0)
    c: Vertical(g1)
    c: Vertical(g2)
    c: Coincident(g3,g2)
    c: Vertical(g3)
    c: Vertical(g4)
    c: Coincident(g5,g4)
    c: Vertical(g5)
    c: Equal(g4,g5)
    c: Equal(g0,g1)
    c: Equal(g2,g3)
    c: Equal(g3,g1)
    c: Equal(g1,g5)
    c: DistanceY(g3,g2) = 20
    c: DistanceY(g-1,g4) = 94
    c: DistanceX(g-1,g4) = 19
    c: DistanceY(g-1,g0) = 57
    c: DistanceX(g-1,g0) = 46
    c: DistanceX(g-1,g2) = 55
    c: DistanceY(g-1,g2) = 34
    c: Coincident(g6,g5)
    c: Coincident(g7,g4)
    c: Coincident(g8,g1)
    c: Coincident(g9,g0)
    c: Coincident(g10,g3)
    c: Coincident(g11,g2)
    c: Equal(g6,g7)
    c: Equal(g6,g9)
    c: Equal(g9,g8)
    c: Equal(g8,g11)
    c: Equal(g11,g10)
    c: Diameter(g10) = 2.4
    c: Coincident(g12,g4)
    c: Coincident(g13,g0)
    c: Equal(g13,g12)
    c: Diameter(g13) = 7
    c: Vertical(g14)
    c: Coincident(g15,g14)
    c: Vertical(g15)
    c: Vertical(g16)
    c: Coincident(g17,g16)
    c: Vertical(g17)
    c: Vertical(g18)
    c: Coincident(g19,g18)
    c: Vertical(g19)
    c: Equal(g14,g15)
    c: Equal(g17,g16)
    c: Equal(g18,g19)
    c: Equal(g19,g17)
    c: Equal(g17,g15)
    c: Equal(g19,g2)
    c: Coincident(g20,g18)
    c: Coincident(g20,g2)
    c: Coincident(g21,g16)
    c: Coincident(g21,g13)
    c: Coincident(g22,g14)
    c: Coincident(g22,g12)
    c: Coincident(g23,g-1)
    c: PointOnObject(g23,g-2)
    c: Coincident(g24,g-1)
    c: PointOnObject(g24,g-2)
    c: Coincident(g25,g-1)
    c: PointOnObject(g25,g-2)
    c: Horizontal(g22)
    c: Horizontal(g21)
    c: Horizontal(g20)
    c: Symmetric(g12,g14,g25)
    c: Symmetric(g16,g13,g24)
    c: Symmetric(g18,g2,g23)
    c: Coincident(g26,g14)
    c: Coincident(g27,g15)
    c: Coincident(g28,g16)
    c: Coincident(g29,g14)
    c: Coincident(g30,g16)
    c: Coincident(g31,g18)
    c: Coincident(g32,g17)
    c: Coincident(g33,g18)
    c: Coincident(g34,g19)
    c: Equal(g29,g12)
    c: Equal(g30,g29)
    c: Equal(g26,g27)
    c: Equal(g27,g28)
    c: Equal(g28,g32)
    c: Equal(g32,g33)
    c: Equal(g33,g34)
    c: Equal(g34,g10)
    c: Equal(g30,g31)
FEATURE [PartDesign::Pocket] Pocket006  label="GroveMtHoles"
  BaseFeature = -> Pocket005
  Length = 5
  Length2 = 100
  Midplane = true
  Profile = -> Sketch021
  Type = 1
FEATURE [Sketcher::SketchObject] Sketch022  label="Sketch_PlateDims"
  FullyConstrained = true
  MapMode = 5
  Support = -> [XY_Plane003]
  expr: Constraints[16] = <<params>>.std_rad
  expr: Constraints[17] = <<params>>.ballc_mt_w
  expr: Constraints[18] = <<params>>.ballc_mt_l
  sketch-geometry (8):
    g0: LineSegment StartX=-6.5 StartY=0 StartZ=0 EndX=6.5 EndY=0 EndZ=0
    g1: LineSegment StartX=8.5 StartY=2 StartZ=0 EndX=8.5 EndY=25 EndZ=0
    g2: LineSegment StartX=6.5 StartY=27 StartZ=0 EndX=-6.5 EndY=27 EndZ=0
    g3: LineSegment StartX=-8.5 StartY=25 StartZ=0 EndX=-8.5 EndY=2 EndZ=0
    g4: ArcOfCircle CenterX=-6.5 CenterY=2 CenterZ=0 NormalX=0 NormalY=0 NormalZ=1 AngleXU=0 Radius=2 StartAngle=3.14159 EndAngle=4.71239
    g5: ArcOfCircle CenterX=6.5 CenterY=2 CenterZ=0 NormalX=0 NormalY=0 NormalZ=1 AngleXU=0 Radius=2 StartAngle=4.71239 EndAngle=6.28319
    g6: ArcOfCircle CenterX=6.5 CenterY=25 CenterZ=0 NormalX=0 NormalY=0 NormalZ=1 AngleXU=0 Radius=2 StartAngle=0 EndAngle=1.5708
    g7: ArcOfCircle CenterX=-6.5 CenterY=25 CenterZ=0 NormalX=0 NormalY=0 NormalZ=1 AngleXU=0 Radius=2 StartAngle=1.5708 EndAngle=3.14159
  constraints (19):
    c: Horizontal(g0)
    c: Horizontal(g2)
    c: Vertical(g1)
    c: Vertical(g3)
    c: Tangent(g0,g4) = -1.5708
    c: Tangent(g3,g4) = -1.5708
    c: Tangent(g0,g5) = -1.5708
    c: Tangent(g1,g5) = -1.5708
    c: Tangent(g1,g6) = -1.5708
    c: Tangent(g2,g6) = -1.5708
    c: Tangent(g2,g7) = -1.5708
    c: Tangent(g3,g7) = -1.5708
    c: Equal(g7,g6)
    c: Equal(g6,g5)
    c: Equal(g5,g4)
    c: Symmetric(g0,g0,g-1)
    c: Radius(g5) = 2
    c: DistanceX(g3,g1) = 17
    c: DistanceY(g0,g2) = 27
FEATURE [PartDesign::Pad] Pad001  label="MainPlate_Ext"
  Direction = (1,1,1)
  Length = 3
  Length2 = 100
  Profile = -> Sketch022
  Reversed = true
  Type = 0
  expr: Length = <<params>>.ballc_mt_t
FEATURE [Sketcher::SketchObject] Sketch023  label="Sketch_BallCMtHoles"
  FullyConstrained = true
  MapMode = 5
  Support = -> [XY_Plane003]
  expr: Constraints[2] = <<params>>.ballc_mt_holespace
  expr: Constraints[4] = <<params>>.m2_hole_clear_diam
  expr: Constraints[6] = <<params>>.ballc_mt_l / 2
  sketch-geometry (3):
    g0: Circle CenterX=0 CenterY=6.15 CenterZ=0 NormalX=0 NormalY=0 NormalZ=1 AngleXU=0 Radius=1.2
    g1: Circle CenterX=0 CenterY=20.85 CenterZ=0 NormalX=0 NormalY=0 NormalZ=1 AngleXU=0 Radius=1.2
    g2: GeomPoint X=0 Y=13.5 Z=0
  constraints (7):
    c: PointOnObject(g0,g-2)
    c: PointOnObject(g1,g-2)
    c: DistanceY(g0,g1) = 14.7
    c: Equal(g1,g0)
    c: Diameter(g1) = 2.4
    c: Symmetric(g1,g0,g2)
    c: DistanceY(g-1,g2) = 13.5
FEATURE [Sketcher::SketchObject] Sketch024
  FullyConstrained = true
  MapMode = 5
  Support = -> [XY_Plane003]
  expr: Constraints[18] = <<params>>.m2_hole_clear_diam
  expr: Constraints[19] = <<params>>.ballc_to_plate_offset
  expr: Constraints[20] = <<params>>.ballc_to_plate_w
  expr: Constraints[21] = <<params>>.ballc_to_plate_l
  sketch-geometry (9):
    g0: LineSegment StartX=-5.5 StartY=24 StartZ=0 EndX=5.5 EndY=24 EndZ=0
    g1: LineSegment StartX=5.5 StartY=24 StartZ=0 EndX=5.5 EndY=3 EndZ=0
    g2: LineSegment StartX=5.5 StartY=3 StartZ=0 EndX=-5.5 EndY=3 EndZ=0
    g3: LineSegment StartX=-5.5 StartY=3 StartZ=0 EndX=-5.5 EndY=24 EndZ=0
    g4: LineSegment StartX=0 StartY=0 StartZ=0 EndX=0 EndY=3 EndZ=0
    g5: Circle CenterX=-5.5 CenterY=24 CenterZ=0 NormalX=0 NormalY=0 NormalZ=1 AngleXU=0 Radius=1.2
    g6: Circle CenterX=5.5 CenterY=24 CenterZ=0 NormalX=0 NormalY=0 NormalZ=1 AngleXU=0 Radius=1.2
    g7: Circle CenterX=5.5 CenterY=3 CenterZ=0 NormalX=0 NormalY=0 NormalZ=1 AngleXU=0 Radius=1.2
    g8: Circle CenterX=-5.5 CenterY=3 CenterZ=0 NormalX=0 NormalY=0 NormalZ=1 AngleXU=0 Radius=1.2
  constraints (22):
    c: Coincident(g0,g1)
    c: Coincident(g1,g2)
    c: Coincident(g2,g3)
    c: Coincident(g3,g0)
    c: Horizontal(g0)
    c: Horizontal(g2)
    c: Vertical(g1)
    c: Vertical(g3)
    c: Coincident(g4,g-1)
    c: PointOnObject(g4,g-2)
    c: Symmetric(g2,g1,g4)
    c: Coincident(g5,g0)
    c: Coincident(g6,g0)
    c: Coincident(g7,g1)
    c: Coincident(g8,g2)
    c: Equal(g7,g6)
    c: Equal(g6,g5)
    c: Equal(g5,g8)
    c: Diameter(g6) = 2.4
    c: DistanceY(g-1,g4) = 3
    c: DistanceX(g5,g6) = 11
    c: DistanceY(g7,g6) = 21
FEATURE [PartDesign::Pocket] Pocket008  label="BallCToPlateHoles"
  BaseFeature = -> Pad001
  Length = 5
  Length2 = 100
  Profile = -> Sketch024
  Type = 1
FEATURE [Sketcher::SketchObject] Sketch025
  FullyConstrained = true
  MapMode = 5
  Support = -> [XY_Plane001]
  expr: Constraints[30] = <<params>>.plate_ballc_hole_loc_l
  expr: Constraints[48] = <<params>>.m2_hole_clear_diam
  expr: Constraints[49] = <<params>>.ballc_to_plate_w
  expr: Constraints[50] = <<params>>.ballc_to_plate_l
  expr: Constraints[4] = 16mm + <<params>>.std_tol_clear
  expr: Constraints[5] = 3.3mm
  sketch-geometry (21):
    g0: Circle CenterX=0 CenterY=94.5 CenterZ=0 NormalX=0 NormalY=0 NormalZ=1 AngleXU=0 Radius=8.15
    g1: Circle CenterX=0 CenterY=102.5 CenterZ=0 NormalX=0 NormalY=0 NormalZ=1 AngleXU=0 Radius=3.3
    g2: Circle CenterX=0 CenterY=86.5 CenterZ=0 NormalX=0 NormalY=0 NormalZ=1 AngleXU=0 Radius=3.3
    g3: ArcOfCircle CenterX=0 CenterY=94.5 CenterZ=0 NormalX=0 NormalY=0 NormalZ=1 AngleXU=0 Radius=8.15 StartAngle=2.27381 EndAngle=4.00937
    g4: ArcOfCircle CenterX=0 CenterY=94.5 CenterZ=0 NormalX=0 NormalY=0 NormalZ=1 AngleXU=0 Radius=8.15 StartAngle=5.4154 EndAngle=7.15097
    g5: ArcOfCircle CenterX=0 CenterY=102.5 CenterZ=0 NormalX=0 NormalY=0 NormalZ=1 AngleXU=0 Radius=3.3 StartAngle=0.39236 EndAngle=2.74923
    g6: ArcOfCircle CenterX=0 CenterY=86.5 CenterZ=0 NormalX=0 NormalY=0 NormalZ=1 AngleXU=0 Radius=3.3 StartAngle=3.53395 EndAngle=5.89083
    g7: ArcOfCircle CenterX=-10.4413 CenterY=106.821 CenterZ=0 NormalX=0 NormalY=0 NormalZ=1 AngleXU=0 Radius=8 StartAngle=5.4154 EndAngle=5.89083
    g8: ArcOfCircle CenterX=10.4413 CenterY=106.821 CenterZ=0 NormalX=0 NormalY=0 NormalZ=1 AngleXU=0 Radius=8 StartAngle=3.53395 EndAngle=4.00937
    g9: ArcOfCircle CenterX=10.4413 CenterY=82.1792 CenterZ=0 NormalX=0 NormalY=0 NormalZ=1 AngleXU=0 Radius=8 StartAngle=2.27381 EndAngle=2.74923
    g10: ArcOfCircle CenterX=-10.4413 CenterY=82.1792 CenterZ=0 NormalX=0 NormalY=0 NormalZ=1 AngleXU=0 Radius=8 StartAngle=0.39236 EndAngle=0.867782
    g11: LineSegment StartX=-3.04923 StartY=103.762 StartZ=0 EndX=3.04923 EndY=103.762 EndZ=0
    g12: LineSegment StartX=-3.04923 StartY=85.2382 StartZ=0 EndX=3.04923 EndY=85.2382 EndZ=0
    g13: LineSegment StartX=-5.5 StartY=105 StartZ=0 EndX=5.5 EndY=105 EndZ=0
    g14: LineSegment StartX=5.5 StartY=105 StartZ=0 EndX=5.5 EndY=84 EndZ=0
    g15: LineSegment StartX=5.5 StartY=84 StartZ=0 EndX=-5.5 EndY=84 EndZ=0
    g16: LineSegment StartX=-5.5 StartY=84 StartZ=0 EndX=-5.5 EndY=105 EndZ=0
    g17: Circle CenterX=-5.5 CenterY=105 CenterZ=0 NormalX=0 NormalY=0 NormalZ=1 AngleXU=0 Radius=1.2
    g18: Circle CenterX=5.5 CenterY=105 CenterZ=0 NormalX=0 NormalY=0 NormalZ=1 AngleXU=0 Radius=1.2
    g19: Circle CenterX=5.5 CenterY=84 CenterZ=0 NormalX=0 NormalY=0 NormalZ=1 AngleXU=0 Radius=1.2
    g20: Circle CenterX=-5.5 CenterY=84 CenterZ=0 NormalX=0 NormalY=0 NormalZ=1 AngleXU=0 Radius=1.2
  constraints (51):
    c: PointOnObject(g0,g-2)
    c: PointOnObject(g1,g-2)
    c: Symmetric(g1,g2,g0)
    c: DistanceY(g2,g1) = 16
    c: Diameter(g0) = 16.3
    c: Radius(g2) = 3.3
    c: Equal(g1,g2)
    c: Coincident(g3,g0)
    c: Coincident(g4,g3)
    c: Coincident(g5,g1)
    c: Coincident(g6,g2)
    c: Tangent(g3,g7) = 1.5708
    c: Tangent(g5,g7) = 1.5708
    c: Tangent(g5,g8) = 1.5708
    c: Tangent(g4,g8) = 1.5708
    c: Tangent(g4,g9) = 1.5708
    c: Tangent(g6,g9) = 1.5708
    c: Tangent(g6,g10) = 1.5708
    c: Tangent(g3,g10) = 1.5708
    c: Equal(g7,g8)
    c: Equal(g8,g9)
    c: Equal(g9,g10)
    c: Coincident(g11,g5)
    c: Coincident(g11,g5)
    c: Horizontal(g11)
    c: Coincident(g12,g6)
    c: Coincident(g12,g6)
    c: PointOnObject(g5,g1)
    c: PointOnObject(g4,g0)
    c: PointOnObject(g6,g2)
    c: DistanceY(g-1,g3) = 94.5
    c: Radius(g8) = 8
    c: Coincident(g13,g14)
    c: Coincident(g14,g15)
    c: Coincident(g15,g16)
    c: Coincident(g16,g13)
    c: Horizontal(g13)
    c: Horizontal(g15)
    c: Vertical(g14)
    c: Vertical(g16)
    c: Symmetric(g13,g15,g3)
    c: Coincident(g17,g13)
    c: Coincident(g18,g13)
    c: Coincident(g19,g14)
    c: Coincident(g20,g15)
    c: Equal(g17,g18)
    c: Equal(g18,g19)
    c: Equal(g19,g20)
    c: Diameter(g18) = 2.4
    c: DistanceX(g17,g18) = 11
    c: DistanceY(g19,g18) = 21
FEATURE [PartDesign::Pocket] Pocket009  label="BallCThruMts"
  BaseFeature = -> Pocket006
  Length = 5
  Length2 = 100
  Midplane = true
  Profile = -> Sketch025
  Type = 1
FEATURE [PartDesign::Plane] DatumPlane  label="Datum_BallCPlate_Bottom"
  AttachmentOffset = pos=(0,0,-3) rot=(0,0,1;0rad)
  Length = 60.198
  MapMode = 5
  Placement = pos=(0,0,-3) rot=(0,0,1;0rad)
  ResizeMode = 0
  Support = -> [XY_Plane003]
  Width = 62.198
  expr: .AttachmentOffset.Base.z = -1 * <<params>>.ballc_mt_t
FEATURE [Sketcher::SketchObject] Sketch026  label="Sketch_BallC_Offset"
  FullyConstrained = true
  MapMode = 5
  Placement = pos=(0,0,-3) rot=(0,0,1;0rad)
  Support = -> [DatumPlane]
  expr: Constraints[7] = <<params>>.ballc_mt_l / 2
  sketch-geometry (11):
    g0: Circle CenterX=0 CenterY=13.5 CenterZ=0 NormalX=0 NormalY=0 NormalZ=1 AngleXU=0 Radius=7.6
    g1: Circle CenterX=0 CenterY=20.85 CenterZ=0 NormalX=0 NormalY=0 NormalZ=1 AngleXU=0 Radius=2.8
    g2: Circle CenterX=0 CenterY=6.15 CenterZ=0 NormalX=0 NormalY=0 NormalZ=1 AngleXU=0 Radius=2.8
    g3: ArcOfCircle CenterX=0 CenterY=13.5 CenterZ=0 NormalX=0 NormalY=0 NormalZ=1 AngleXU=0 Radius=7.6 StartAngle=2.08108 EndAngle=4.20211
    g4: ArcOfCircle CenterX=0 CenterY=13.5 CenterZ=0 NormalX=0 NormalY=0 NormalZ=1 AngleXU=0 Radius=7.6 StartAngle=5.22267 EndAngle=7.3437
    g5: ArcOfCircle CenterX=0 CenterY=20.85 CenterZ=0 NormalX=0 NormalY=0 NormalZ=1 AngleXU=0 Radius=2.8 StartAngle=0.215634 EndAngle=2.92596
    g6: ArcOfCircle CenterX=0 CenterY=6.15 CenterZ=0 NormalX=0 NormalY=0 NormalZ=1 AngleXU=0 Radius=2.8 StartAngle=3.35723 EndAngle=6.06755
    g7: ArcOfCircle CenterX=-4.68884 CenterY=21.877 CenterZ=0 NormalX=0 NormalY=0 NormalZ=1 AngleXU=0 Radius=2 StartAngle=5.22267 EndAngle=6.06755
    g8: ArcOfCircle CenterX=4.68884 CenterY=21.877 CenterZ=0 NormalX=0 NormalY=0 NormalZ=1 AngleXU=0 Radius=2 StartAngle=3.35723 EndAngle=4.20211
    g9: ArcOfCircle CenterX=4.68884 CenterY=5.12296 CenterZ=0 NormalX=0 NormalY=0 NormalZ=1 AngleXU=0 Radius=2 StartAngle=2.08108 EndAngle=2.92596
    g10: ArcOfCircle CenterX=-4.68884 CenterY=5.12296 CenterZ=0 NormalX=0 NormalY=0 NormalZ=1 AngleXU=0 Radius=2 StartAngle=0.215634 EndAngle=1.06052
  constraints (28):
    c: PointOnObject(g0,g-2)
    c: PointOnObject(g1,g-2)
    c: Symmetric(g1,g2,g0)
    c: Equal(g1,g2)
    c: Diameter(g0) = 15.2
    c: Radius(g2) = 2.8
    c: DistanceY(g2,g1) = 14.7
    c: DistanceY(g-1,g0) = 13.5
    c: Coincident(g3,g0)
    c: Coincident(g4,g3)
    c: Coincident(g5,g1)
    c: Coincident(g6,g2)
    c: Tangent(g3,g7) = 1.5708
    c: Tangent(g5,g7) = 1.5708
    c: Tangent(g5,g8) = 1.5708
    c: Tangent(g4,g8) = 1.5708
    c: Tangent(g4,g9) = 1.5708
    c: Tangent(g6,g9) = 1.5708
    c: Tangent(g6,g10) = 1.5708
    c: Tangent(g3,g10) = 1.5708
    c: Equal(g7,g8)
    c: Equal(g8,g9)
    c: Equal(g9,g10)
    c: Radius(g8) = 2
    c: PointOnObject(g3,g0)
    c: PointOnObject(g4,g0)
    c: PointOnObject(g6,g2)
    c: PointOnObject(g5,g1)
FEATURE [PartDesign::Pad] Pad002  label="BallCOffset"
  BaseFeature = -> Pocket008
  Direction = (1,1,1)
  Length = 1
  Length2 = 100
  Profile = -> Sketch026
  Reversed = true
  Type = 0
FEATURE [PartDesign::Pocket] Pocket010  label="BallCMtHoles"
  BaseFeature = -> Pad002
  Length = 5
  Length2 = 100
  Midplane = true
  Profile = -> Sketch023
  Type = 1
FEATURE [Sketcher::SketchObject] Sketch027
  FullyConstrained = true
  MapMode = 5
  Support = -> [XY_Plane003]
  expr: Constraints[11] = <<params>>.ballc_to_plate_w
  expr: Constraints[93] = <<params>>.m2_nut_clear_flat
  expr: Constraints[12] = <<params>>.ballc_to_plate_l
  expr: Constraints[13] = <<params>>.ballc_to_plate_offset
  sketch-geometry (33):
    g0: LineSegment StartX=-5.5 StartY=24 StartZ=0 EndX=5.5 EndY=24 EndZ=0
    g1: LineSegment StartX=5.5 StartY=24 StartZ=0 EndX=5.5 EndY=3 EndZ=0
    g2: LineSegment StartX=5.5 StartY=3 StartZ=0 EndX=-5.5 EndY=3 EndZ=0
    g3: LineSegment StartX=-5.5 StartY=3 StartZ=0 EndX=-5.5 EndY=24 EndZ=0
    g4: LineSegment StartX=0 StartY=0 StartZ=0 EndX=0 EndY=3 EndZ=0
    g5: LineSegment StartX=4.28756 StartY=0.9 StartZ=0 EndX=6.71244 EndY=0.9 EndZ=0
    g6: LineSegment StartX=6.71244 StartY=0.9 StartZ=0 EndX=7.92487 EndY=3 EndZ=0
    g7: LineSegment StartX=7.92487 StartY=3 StartZ=0 EndX=6.71244 EndY=5.1 EndZ=0
    g8: LineSegment StartX=6.71244 StartY=5.1 StartZ=0 EndX=4.28756 EndY=5.1 EndZ=0
    g9: LineSegment StartX=4.28756 StartY=5.1 StartZ=0 EndX=3.07513 EndY=3 EndZ=0
    g10: LineSegment StartX=3.07513 StartY=3 StartZ=0 EndX=4.28756 EndY=0.9 EndZ=0
    g11: Circle CenterX=5.5 CenterY=3 CenterZ=0 NormalX=0 NormalY=0 NormalZ=1 AngleXU=0 Radius=2.42487
    g12: LineSegment StartX=6.71244 StartY=26.1 StartZ=0 EndX=4.28756 EndY=26.1 EndZ=0
    g13: LineSegment StartX=4.28756 StartY=26.1 StartZ=0 EndX=3.07513 EndY=24 EndZ=0
    g14: LineSegment StartX=3.07513 StartY=24 StartZ=0 EndX=4.28756 EndY=21.9 EndZ=0
    g15: LineSegment StartX=4.28756 StartY=21.9 StartZ=0 EndX=6.71244 EndY=21.9 EndZ=0
    g16: LineSegment StartX=6.71244 StartY=21.9 StartZ=0 EndX=7.92487 EndY=24 EndZ=0
    g17: LineSegment StartX=7.92487 StartY=24 StartZ=0 EndX=6.71244 EndY=26.1 EndZ=0
    g18: Circle CenterX=5.5 CenterY=24 CenterZ=0 NormalX=0 NormalY=0 NormalZ=1 AngleXU=0 Radius=2.42487
    g19: LineSegment StartX=-4.28756 StartY=21.9 StartZ=0 EndX=-3.07513 EndY=24 EndZ=0
    g20: LineSegment StartX=-3.07513 StartY=24 StartZ=0 EndX=-4.28756 EndY=26.1 EndZ=0
    g21: LineSegment StartX=-4.28756 StartY=26.1 StartZ=0 EndX=-6.71244 EndY=26.1 EndZ=0
    g22: LineSegment StartX=-6.71244 StartY=26.1 StartZ=0 EndX=-7.92487 EndY=24 EndZ=0
    g23: LineSegment StartX=-7.92487 StartY=24 StartZ=0 EndX=-6.71244 EndY=21.9 EndZ=0
    g24: LineSegment StartX=-6.71244 StartY=21.9 StartZ=0 EndX=-4.28756 EndY=21.9 EndZ=0
    g25: Circle CenterX=-5.5 CenterY=24 CenterZ=0 NormalX=0 NormalY=0 NormalZ=1 AngleXU=0 Radius=2.42487
    g26: LineSegment StartX=-4.28756 StartY=0.9 StartZ=0 EndX=-3.07513 EndY=3 EndZ=0
    g27: LineSegment StartX=-3.07513 StartY=3 StartZ=0 EndX=-4.28756 EndY=5.1 EndZ=0
    g28: LineSegment StartX=-4.28756 StartY=5.1 StartZ=0 EndX=-6.71244 EndY=5.1 EndZ=0
    g29: LineSegment StartX=-6.71244 StartY=5.1 StartZ=0 EndX=-7.92487 EndY=3 EndZ=0
    g30: LineSegment StartX=-7.92487 StartY=3 StartZ=0 EndX=-6.71244 EndY=0.9 EndZ=0
    g31: LineSegment StartX=-6.71244 StartY=0.9 StartZ=0 EndX=-4.28756 EndY=0.9 EndZ=0
    g32: Circle CenterX=-5.5 CenterY=3 CenterZ=0 NormalX=0 NormalY=0 NormalZ=1 AngleXU=0 Radius=2.42487
  constraints (78):
    c: Coincident(g0,g1)
    c: Coincident(g1,g2)
    c: Coincident(g2,g3)
    c: Coincident(g3,g0)
    c: Horizontal(g0)
    c: Horizontal(g2)
    c: Vertical(g1)
    c: Vertical(g3)
    c: Coincident(g4,g-1)
    c: PointOnObject(g4,g-2)
    c: Symmetric(g2,g1,g4)
    c: DistanceX(g0,g0) = 11
    c: DistanceY(g1,g0) = 21
    c: DistanceY(g-1,g4) = 3
    c: Coincident(g5,g6)
    c: Coincident(g6,g7)
    c: Coincident(g7,g8)
    c: Coincident(g8,g9)
    c: Coincident(g9,g10)
    c: Coincident(g10,g5)
    c: Equal(g5, g6-g10) x5
    c: PointOnObject(g5,g11)
    c: PointOnObject(g6,g11)
    c: PointOnObject(g7,g11)
    c: PointOnObject(g8,g11)
    c: PointOnObject(g9,g11)
    c: PointOnObject(g10,g11)
    c: Coincident(g11,g1)
    c: Coincident(g12,g13)
    c: Coincident(g13,g14)
    c: Coincident(g14,g15)
    c: Coincident(g15,g16)
    c: Coincident(g16,g17)
    c: Coincident(g17,g12)
    c: Equal(g12, g13-g17) x5
    c: PointOnObject(g12,g18)
    c: PointOnObject(g13,g18)
    c: PointOnObject(g14,g18)
    c: PointOnObject(g15,g18)
    c: PointOnObject(g16,g18)
    c: PointOnObject(g17,g18)
    c: Coincident(g18,g0)
    c: Coincident(g19,g20)
    c: Coincident(g20,g21)
    c: Coincident(g21,g22)
    c: Coincident(g22,g23)
    c: Coincident(g23,g24)
    c: Coincident(g24,g19)
    c: Equal(g19, g20-g24) x5
    c: PointOnObject(g19,g25)
    c: PointOnObject(g20,g25)
    c: PointOnObject(g21,g25)
    c: PointOnObject(g22,g25)
    c: PointOnObject(g23,g25)
    c: PointOnObject(g24,g25)
    c: Coincident(g25,g0)
    c: Coincident(g26,g27)
    c: Coincident(g27,g28)
    c: Coincident(g28,g29)
    c: Coincident(g29,g30)
    c: Coincident(g30,g31)
    c: Coincident(g31,g26)
    c: Equal(g26, g27-g31) x5
    c: PointOnObject(g26,g32)
    c: PointOnObject(g27,g32)
    c: PointOnObject(g28,g32)
    c: PointOnObject(g29,g32)
    c: PointOnObject(g30,g32)
    c: PointOnObject(g31,g32)
    c: Coincident(g32,g2)
    c: Horizontal(g15)
    c: Horizontal(g24)
    c: Horizontal(g28)
    c: Horizontal(g8)
    c: Equal(g18,g11)
    c: Equal(g18,g25)
    c: Equal(g25,g32)
    c: DistanceY(g5,g7) = 4.2
FEATURE [PartDesign::Pocket] Pocket011  label="BallCMtCSunk"
  BaseFeature = -> Pocket010
  Length = 1.75
  Length2 = 100
  Profile = -> Sketch027
  Type = 0
  expr: Length = <<params>>.m2_nut_min_depth
FEATURE [PartDesign::Body] Body001  label="PB3D_Triplate_BallCastMt"
  Group = -> [Sketch022,Pad001,Sketch023,Sketch024,Pocket008,Sketch026,DatumPlane,Pad002,Pocket010,Sketch027,Pocket011]
  Origin = -> Origin003
  Tip = -> Pocket011
FEATURE [App::Part] Part001  label="PB3D_TriPlate_BallCastMt_Pololu"
  Group = -> [Body001]
  Origin = -> Origin002
  Placement = pos=(0,81,3) rot=(0,0,1;0rad)
FEATURE [Sketcher::SketchObject] Sketch028  label="Sketch_ShellMts"
  FullyConstrained = true
  MapMode = 5
  Support = -> [XY_Plane001]
  expr: Constraints[74] = <<params>>.front_diameter
  expr: Constraints[69] = <<params>>.back_vert_edge
  expr: Constraints[71] = <<params>>.plate_width
  expr: Constraints[31] = <<params>>.wheel_well_plate_width
  expr: Constraints[37] = <<params>>.tail_width
  expr: Constraints[35] = <<params>>.plate_length
  expr: Constraints[57] = <<params>>.std_rad
  expr: Constraints[72] = <<params>>.std_rad
  expr: Constraints[68] = <<params>>.front_vert_edge
  expr: Constraints[70] = <<params>>.wheel_well_clearance
  expr: Constraints[55] = <<params>>.std_rad
  expr: Constraints[36] = <<params>>.tail_rad
  expr: Constraints[99] = <<params>>.m25_hole_clear_diam
  expr: Constraints[102] = <<params>>.shelltobot_frontmid_offset_xy
  expr: Constraints[106] = <<params>>.shelltobot_frontmid_offset_xy
  expr: Constraints[101] = <<params>>.shelltobot_frontmid_offset_xy
  expr: Constraints[100] = <<params>>.shelltobot_back_offset_y
  expr: Constraints[73] = <<params>>.std_rad
  expr: Constraints[113] = <<params>>.shelltobot_back_offset_x
  sketch-geometry (46):
    g0: LineSegment StartX=-57.5 StartY=17 StartZ=0 EndX=-57.5 EndY=-17 EndZ=0
    g1: LineSegment StartX=57.5 StartY=17 StartZ=0 EndX=57.5 EndY=-17 EndZ=0
    g2: LineSegment StartX=-57.5 StartY=0 StartZ=0 EndX=57.5 EndY=0 EndZ=0
    g3: LineSegment StartX=-64.5 StartY=-24 StartZ=0 EndX=-75.5 EndY=-24 EndZ=0
    g4: LineSegment StartX=64.5 StartY=-24 StartZ=0 EndX=75.5 EndY=-24 EndZ=0
    g5: ArcOfCircle CenterX=0 CenterY=52.6846 CenterZ=0 NormalX=0 NormalY=0 NormalZ=1 AngleXU=0 Radius=112.5 StartAngle=3.96017 EndAngle=5.4646
    g6: LineSegment StartX=-64.5 StartY=24 StartZ=0 EndX=-75.5 EndY=24 EndZ=0
    g7: LineSegment StartX=64.5 StartY=24 StartZ=0 EndX=75.5 EndY=24 EndZ=0
    g8: LineSegment StartX=-77.1162 StartY=42.1781 StartZ=0 EndX=-29.0404 EndY=108.13 EndZ=0
    g9: LineSegment StartX=-25 StartY=110.185 StartZ=0 EndX=25 EndY=110.185 EndZ=0
    g10: LineSegment StartX=29.0404 StartY=108.13 StartZ=0 EndX=77.1162 EndY=42.1781 EndZ=0
    g11: LineSegment StartX=0 StartY=0 StartZ=0 EndX=0 EndY=110.185 EndZ=0
    g12: ArcOfCircle CenterX=-25 CenterY=105.185 CenterZ=0 NormalX=0 NormalY=0 NormalZ=1 AngleXU=0 Radius=5 StartAngle=1.5708 EndAngle=2.5117
    g13: ArcOfCircle CenterX=25 CenterY=105.185 CenterZ=0 NormalX=0 NormalY=0 NormalZ=1 AngleXU=0 Radius=5 StartAngle=0.629894 EndAngle=1.5708
    g14: ArcOfCircle CenterX=-64.5 CenterY=17 CenterZ=0 NormalX=0 NormalY=0 NormalZ=1 AngleXU=0 Radius=7 StartAngle=0 EndAngle=1.5708
    g15: ArcOfCircle CenterX=-64.5 CenterY=-17 CenterZ=0 NormalX=0 NormalY=0 NormalZ=1 AngleXU=0 Radius=7 StartAngle=4.71239 EndAngle=6.28319
    g16: ArcOfCircle CenterX=64.5 CenterY=-17 CenterZ=0 NormalX=0 NormalY=0 NormalZ=1 AngleXU=0 Radius=7 StartAngle=3.14159 EndAngle=4.71239
    g17: ArcOfCircle CenterX=64.5 CenterY=17 CenterZ=0 NormalX=0 NormalY=0 NormalZ=1 AngleXU=0 Radius=7 StartAngle=1.5708 EndAngle=3.14159
    g18: GeomPoint X=0 Y=-59.8154 Z=0
    g19: LineSegment StartX=77.5 StartY=26 StartZ=0 EndX=77.5 EndY=41 EndZ=0
    g20: LineSegment StartX=77.5 StartY=-26 StartZ=0 EndX=77.5 EndY=-28 EndZ=0
    g21: LineSegment StartX=-77.5 StartY=-28 StartZ=0 EndX=-77.5 EndY=-26 EndZ=0
    g22: LineSegment StartX=-77.5 StartY=26 StartZ=0 EndX=-77.5 EndY=41 EndZ=0
    g23: ArcOfCircle CenterX=75.5 CenterY=-28 CenterZ=0 NormalX=0 NormalY=0 NormalZ=1 AngleXU=0 Radius=2 StartAngle=5.4646 EndAngle=6.28319
    g24: ArcOfCircle CenterX=75.5 CenterY=-26 CenterZ=0 NormalX=0 NormalY=0 NormalZ=1 AngleXU=0 Radius=2 StartAngle=0 EndAngle=1.5708
    g25: ArcOfCircle CenterX=-75.5 CenterY=-28 CenterZ=0 NormalX=0 NormalY=0 NormalZ=1 AngleXU=0 Radius=2 StartAngle=3.14159 EndAngle=3.96017
    g26: ArcOfCircle CenterX=-75.5 CenterY=-26 CenterZ=0 NormalX=0 NormalY=0 NormalZ=1 AngleXU=0 Radius=2 StartAngle=1.5708 EndAngle=3.14159
    g27: ArcOfCircle CenterX=75.5 CenterY=26 CenterZ=0 NormalX=0 NormalY=0 NormalZ=1 AngleXU=0 Radius=2 StartAngle=4.71239 EndAngle=6.28319
    g28: ArcOfCircle CenterX=75.5 CenterY=41 CenterZ=0 NormalX=0 NormalY=0 NormalZ=1 AngleXU=0 Radius=2 StartAngle=5e-16 EndAngle=0.629894
    g29: ArcOfCircle CenterX=-75.5 CenterY=26 CenterZ=0 NormalX=0 NormalY=0 NormalZ=1 AngleXU=0 Radius=2 StartAngle=3.14159 EndAngle=4.71239
    g30: ArcOfCircle CenterX=-75.5 CenterY=41 CenterZ=0 NormalX=0 NormalY=0 NormalZ=1 AngleXU=0 Radius=2 StartAngle=2.5117 EndAngle=3.14159
    g31: LineSegment StartX=-36.1217 StartY=90.1846 StartZ=0 EndX=36.1217 EndY=90.1846 EndZ=0
    g32: LineSegment StartX=-72.5 StartY=29 StartZ=0 EndX=72.5 EndY=29 EndZ=0
    g33: LineSegment StartX=-72.5 StartY=-28 StartZ=0 EndX=72.5 EndY=-28 EndZ=0
    g34: LineSegment StartX=0 StartY=0 StartZ=0 EndX=0 EndY=29 EndZ=0
    g35: LineSegment StartX=0 StartY=0 StartZ=0 EndX=0 EndY=90.1846 EndZ=0
    g36: LineSegment StartX=0 StartY=0 StartZ=0 EndX=0 EndY=-28 EndZ=0
    g37: Circle CenterX=-36.1217 CenterY=90.1846 CenterZ=0 NormalX=0 NormalY=0 NormalZ=1 AngleXU=0 Radius=1.4
    g38: Circle CenterX=36.1217 CenterY=90.1846 CenterZ=0 NormalX=0 NormalY=0 NormalZ=1 AngleXU=0 Radius=1.4
    g39: Circle CenterX=72.5 CenterY=29 CenterZ=0 NormalX=0 NormalY=0 NormalZ=1 AngleXU=0 Radius=1.4
    g40: Circle CenterX=-72.5 CenterY=29 CenterZ=0 NormalX=0 NormalY=0 NormalZ=1 AngleXU=0 Radius=1.4
    g41: Circle CenterX=72.5 CenterY=-28 CenterZ=0 NormalX=0 NormalY=0 NormalZ=1 AngleXU=0 Radius=1.4
    g42: Circle CenterX=-72.5 CenterY=-28 CenterZ=0 NormalX=0 NormalY=0 NormalZ=1 AngleXU=0 Radius=1.4
    g43: LineSegment StartX=36.1217 StartY=90.1846 StartZ=0 EndX=42.1217 EndY=90.1846 EndZ=0
    g44: LineSegment StartX=36.1217 StartY=90.1846 StartZ=0 EndX=36.1217 EndY=98.4156 EndZ=0
    g45: LineSegment StartX=72.5 StartY=-28 StartZ=0 EndX=77.5 EndY=-28 EndZ=0
  constraints (114):
    c: Vertical(g0)
    c: Vertical(g1)
    c: Horizontal(g2)
    c: Symmetric(g2,g2,g-1)
    c: Horizontal(g3)
    c: Horizontal(g4)
    c: PointOnObject(g5,g-2)
    c: Horizontal(g6)
    c: Horizontal(g7)
    c: Horizontal(g9)
    c: Coincident(g11,g-1)
    c: PointOnObject(g11,g-2)
    c: Tangent(g8,g12) = 1.5708
    c: Tangent(g9,g12) = 1.5708
    c: Tangent(g9,g13) = 1.5708
    c: Tangent(g10,g13) = 1.5708
    c: Tangent(g6,g14) = -1.5708
    c: Tangent(g0,g14) = 1.5708
    c: Tangent(g3,g15) = 1.5708
    c: Tangent(g0,g15) = 1.5708
    c: Tangent(g1,g16) = -1.5708
    c: Tangent(g4,g16) = -1.5708
    c: Tangent(g1,g17) = -1.5708
    c: Tangent(g7,g17) = 1.5708
    c: Equal(g13,g12)
    c: Symmetric(g9,g9,g11)
    c: Equal(g16,g17)
    c: Equal(g17,g14)
    c: Equal(g14,g15)
    c: PointOnObject(g18,g-2)
    c: PointOnObject(g18,g5)
    c: DistanceX(g2,g2) = 115
    c: Symmetric(g0,g0,g2)
    c: Symmetric(g1,g1,g2)
    c: Radius(g17) = 7
    c: DistanceY(g18,g9) = 170
    c: Radius(g13) = 5
    c: DistanceX(g9,g9) = 50
    c: Equal(g7,g6)
    c: Equal(g7,g4)
    c: Vertical(g19)
    c: Vertical(g20)
    c: Vertical(g21)
    c: Vertical(g22)
    c: Equal(g3,g6)
    c: Equal(g8,g10)
    c: Tangent(g5,g23) = -1.5708
    c: Tangent(g20,g23) = 1.5708
    c: Tangent(g20,g24) = 1.5708
    c: Tangent(g4,g24) = 1.5708
    c: Tangent(g5,g25) = -1.5708
    c: Tangent(g21,g25) = 1.5708
    c: Tangent(g21,g26) = 1.5708
    c: Tangent(g3,g26) = -1.5708
    c: Equal(g26,g24)
    c: Radius(g24) = 2
    c: Equal(g23,g25)
    c: Radius(g23) = 2
    c: Tangent(g7,g27) = -1.5708
    c: Tangent(g19,g27) = -1.5708
    c: Tangent(g19,g28) = -1.5708
    c: Tangent(g10,g28) = 1.5708
    c: Tangent(g6,g29) = 1.5708
    c: Tangent(g22,g29) = 1.5708
    c: Tangent(g8,g30) = 1.5708
    c: Tangent(g22,g30) = 1.5708
    c: Equal(g27,g29)
    c: Equal(g28,g30)
    c: DistanceY(g20,g20) = 2
    c: DistanceY(g19,g19) = 15
    c: DistanceY(g4,g7) = 48
    c: DistanceX(g21,g20) = 155
    c: Radius(g27) = 2
    c: Radius(g28) = 2
    c: Diameter(g5) = 225
    c: Equal(g21,g20)
    c: Horizontal(g31)
    c: Horizontal(g32)
    c: Horizontal(g33)
    c: Coincident(g34,g-1)
    c: PointOnObject(g34,g11)
    c: Coincident(g35,g-1)
    c: PointOnObject(g35,g11)
    c: Coincident(g36,g-1)
    c: PointOnObject(g36,g-2)
    c: Symmetric(g31,g31,g35)
    c: Symmetric(g32,g32,g34)
    c: Symmetric(g33,g33,g36)
    c: Coincident(g37,g31)
    c: Coincident(g38,g31)
    c: Coincident(g39,g32)
    c: Coincident(g40,g32)
    c: Coincident(g41,g33)
    c: Coincident(g42,g33)
    c: Equal(g41,g39)
    c: Equal(g39,g38)
    c: Equal(g38,g37)
    c: Equal(g37,g40)
    c: Equal(g40,g42)
    c: Diameter(g41) = 2.8
    c: DistanceY(g35,g11) = 20
    c: DistanceX(g39,g19) = 5
    c: DistanceY(g7,g39) = 5
    c: Coincident(g43,g38)
    c: PointOnObject(g43,g10)
    c: Horizontal(g43)
    c: DistanceX(g41,g20) = 5
    c: Coincident(g44,g38)
    c: PointOnObject(g44,g10)
    c: Vertical(g44)
    c: Coincident(g45,g41)
    c: Coincident(g45,g20)
    c: Horizontal(g45)
    c: DistanceX(g38,g43) = 6
FEATURE [PartDesign::Pocket] Pocket012  label="ShellMts"
  BaseFeature = -> Pocket009
  Length = 5
  Length2 = 100
  Midplane = true
  Profile = -> Sketch028
  Type = 1
FEATURE [Sketcher::SketchObject] Sketch029  label="USMtHoles"
  FullyConstrained = true
  MapMode = 5
  Support = -> [XY_Plane001]
  expr: Constraints[19] = <<params>>.usr_mt_leng
  expr: Constraints[9] = <<params>>.usr_mt_width
  expr: Constraints[8] = <<params>>.usr_mt_loc_x
  expr: Constraints[7] = <<params>>.m25_hole_clear_diam
  sketch-geometry (8):
    g0: LineSegment StartX=-20 StartY=-24 StartZ=0 EndX=20 EndY=-24 EndZ=0
    g1: LineSegment StartX=0 StartY=0 StartZ=0 EndX=0 EndY=-24 EndZ=0
    g2: Circle CenterX=20 CenterY=-24 CenterZ=0 NormalX=0 NormalY=0 NormalZ=1 AngleXU=0 Radius=1.4
    g3: Circle CenterX=-20 CenterY=-24 CenterZ=0 NormalX=0 NormalY=0 NormalZ=1 AngleXU=0 Radius=1.4
    g4: LineSegment StartX=-20 StartY=-24 StartZ=0 EndX=-20 EndY=-45 EndZ=0
    g5: LineSegment StartX=20 StartY=-24 StartZ=0 EndX=20 EndY=-45 EndZ=0
    g6: Circle CenterX=-20 CenterY=-45 CenterZ=0 NormalX=0 NormalY=0 NormalZ=1 AngleXU=0 Radius=1.4
    g7: Circle CenterX=20 CenterY=-45 CenterZ=0 NormalX=0 NormalY=0 NormalZ=1 AngleXU=0 Radius=1.4
  constraints (20):
    c: Horizontal(g0)
    c: Coincident(g1,g-1)
    c: PointOnObject(g1,g-2)
    c: Symmetric(g0,g0,g1)
    c: Coincident(g2,g0)
    c: Coincident(g3,g0)
    c: Equal(g2,g3)
    c: Diameter(g2) = 2.8
    c: DistanceY(g1,g-1) = 24
    c: DistanceX(g3,g2) = 40
    c: Coincident(g4,g3)
    c: Vertical(g4)
    c: Coincident(g5,g2)
    c: Vertical(g5)
    c: Equal(g5,g4)
    c: Coincident(g6,g4)
    c: Coincident(g7,g5)
    c: Equal(g7,g2)
    c: Equal(g6,g3)
    c: DistanceY(g7,g2) = 21
FEATURE [PartDesign::Pocket] Pocket013  label="USRMtHoles"
  BaseFeature = -> Pocket012
  Length = 5
  Length2 = 100
  Profile = -> Sketch029
  Type = 1
FEATURE [Sketcher::SketchObject] Sketch030  label="Sketch_BMPRHoles"
  FullyConstrained = true
  MapMode = 5
  Support = -> [XY_Plane001]
  expr: Constraints[101] = <<params>>.m25_hole_clear_diam
  expr: Constraints[93] = <<params>>.bmpr_switch_hole_space
  expr: Constraints[77] = <<params>>.front_diameter - 2 * <<params>>.bmpr_switch_diam_offset
  expr: Constraints[92] = <<params>>.bmpr_switch_ang
  expr: Constraints[91] = <<params>>.bmpr_switch_ang
  expr: Constraints[72] = <<params>>.std_rad
  expr: Constraints[57] = <<params>>.std_rad
  expr: Constraints[68] = <<params>>.front_vert_edge
  expr: Constraints[71] = <<params>>.plate_width
  expr: Constraints[69] = <<params>>.back_vert_edge
  expr: Constraints[74] = <<params>>.front_diameter
  expr: Constraints[36] = <<params>>.tail_rad
  expr: Constraints[37] = <<params>>.tail_width
  expr: Constraints[35] = <<params>>.plate_length
  expr: Constraints[73] = <<params>>.std_rad
  expr: Constraints[31] = <<params>>.wheel_well_plate_width
  expr: Constraints[70] = <<params>>.wheel_well_clearance
  expr: Constraints[55] = <<params>>.std_rad
  sketch-geometry (44):
    g0: LineSegment StartX=-57.5 StartY=17 StartZ=0 EndX=-57.5 EndY=-17 EndZ=0
    g1: LineSegment StartX=57.5 StartY=17 StartZ=0 EndX=57.5 EndY=-17 EndZ=0
    g2: LineSegment StartX=-57.5 StartY=0 StartZ=0 EndX=57.5 EndY=0 EndZ=0
    g3: LineSegment StartX=-64.5 StartY=-24 StartZ=0 EndX=-75.5 EndY=-24 EndZ=0
    g4: LineSegment StartX=64.5 StartY=-24 StartZ=0 EndX=75.5 EndY=-24 EndZ=0
    g5: ArcOfCircle CenterX=0 CenterY=52.6846 CenterZ=0 NormalX=0 NormalY=0 NormalZ=1 AngleXU=0 Radius=112.5 StartAngle=3.96017 EndAngle=5.4646
    g6: LineSegment StartX=-64.5 StartY=24 StartZ=0 EndX=-75.5 EndY=24 EndZ=0
    g7: LineSegment StartX=64.5 StartY=24 StartZ=0 EndX=75.5 EndY=24 EndZ=0
    g8: LineSegment StartX=-77.1162 StartY=42.1781 StartZ=0 EndX=-29.0404 EndY=108.13 EndZ=0
    g9: LineSegment StartX=-25 StartY=110.185 StartZ=0 EndX=25 EndY=110.185 EndZ=0
    g10: LineSegment StartX=29.0404 StartY=108.13 StartZ=0 EndX=77.1162 EndY=42.1781 EndZ=0
    g11: LineSegment StartX=0 StartY=0 StartZ=0 EndX=0 EndY=110.185 EndZ=0
    g12: ArcOfCircle CenterX=-25 CenterY=105.185 CenterZ=0 NormalX=0 NormalY=0 NormalZ=1 AngleXU=0 Radius=5 StartAngle=1.5708 EndAngle=2.5117
    g13: ArcOfCircle CenterX=25 CenterY=105.185 CenterZ=0 NormalX=0 NormalY=0 NormalZ=1 AngleXU=0 Radius=5 StartAngle=0.629894 EndAngle=1.5708
    g14: ArcOfCircle CenterX=-64.5 CenterY=17 CenterZ=0 NormalX=0 NormalY=0 NormalZ=1 AngleXU=0 Radius=7 StartAngle=0 EndAngle=1.5708
    g15: ArcOfCircle CenterX=-64.5 CenterY=-17 CenterZ=0 NormalX=0 NormalY=0 NormalZ=1 AngleXU=0 Radius=7 StartAngle=4.71239 EndAngle=6.28319
    g16: ArcOfCircle CenterX=64.5 CenterY=-17 CenterZ=0 NormalX=0 NormalY=0 NormalZ=1 AngleXU=0 Radius=7 StartAngle=3.14159 EndAngle=4.71239
    g17: ArcOfCircle CenterX=64.5 CenterY=17 CenterZ=0 NormalX=0 NormalY=0 NormalZ=1 AngleXU=0 Radius=7 StartAngle=1.5708 EndAngle=3.14159
    g18: GeomPoint X=0 Y=-59.8154 Z=0
    g19: LineSegment StartX=77.5 StartY=26 StartZ=0 EndX=77.5 EndY=41 EndZ=0
    g20: LineSegment StartX=77.5 StartY=-26 StartZ=0 EndX=77.5 EndY=-28 EndZ=0
    g21: LineSegment StartX=-77.5 StartY=-28 StartZ=0 EndX=-77.5 EndY=-26 EndZ=0
    g22: LineSegment StartX=-77.5 StartY=26 StartZ=0 EndX=-77.5 EndY=41 EndZ=0
    g23: ArcOfCircle CenterX=75.5 CenterY=-28 CenterZ=0 NormalX=0 NormalY=0 NormalZ=1 AngleXU=0 Radius=2 StartAngle=5.4646 EndAngle=6.28319
    g24: ArcOfCircle CenterX=75.5 CenterY=-26 CenterZ=0 NormalX=0 NormalY=0 NormalZ=1 AngleXU=0 Radius=2 StartAngle=0 EndAngle=1.5708
    g25: ArcOfCircle CenterX=-75.5 CenterY=-28 CenterZ=0 NormalX=0 NormalY=0 NormalZ=1 AngleXU=0 Radius=2 StartAngle=3.14159 EndAngle=3.96017
    g26: ArcOfCircle CenterX=-75.5 CenterY=-26 CenterZ=0 NormalX=0 NormalY=0 NormalZ=1 AngleXU=0 Radius=2 StartAngle=1.5708 EndAngle=3.14159
    g27: ArcOfCircle CenterX=75.5 CenterY=26 CenterZ=0 NormalX=0 NormalY=0 NormalZ=1 AngleXU=0 Radius=2 StartAngle=4.71239 EndAngle=6.28319
    g28: ArcOfCircle CenterX=75.5 CenterY=41 CenterZ=0 NormalX=0 NormalY=0 NormalZ=1 AngleXU=0 Radius=2 StartAngle=-9e-16 EndAngle=0.629894
    g29: ArcOfCircle CenterX=-75.5 CenterY=26 CenterZ=0 NormalX=0 NormalY=0 NormalZ=1 AngleXU=0 Radius=2 StartAngle=3.14159 EndAngle=4.71239
    g30: ArcOfCircle CenterX=-75.5 CenterY=41 CenterZ=0 NormalX=0 NormalY=0 NormalZ=1 AngleXU=0 Radius=2 StartAngle=2.5117 EndAngle=3.14159
    g31: Circle CenterX=0 CenterY=52.6846 CenterZ=0 NormalX=0 NormalY=0 NormalZ=1 AngleXU=0 Radius=107.5
    g32: LineSegment StartX=0 StartY=52.6846 StartZ=0 EndX=56.1686 EndY=-38.9742 EndZ=0
    g33: LineSegment StartX=0 StartY=52.6846 StartZ=0 EndX=-56.1686 EndY=-38.9742 EndZ=0
    g34: LineSegment StartX=52.1186 StartY=-41.4561 StartZ=0 EndX=60.2186 EndY=-36.4924 EndZ=0
    g35: LineSegment StartX=-52.1186 StartY=-41.4561 StartZ=0 EndX=-60.2186 EndY=-36.4924 EndZ=0
    g36: GeomPoint X=-56.1686 Y=-38.9742 Z=0
    g37: GeomPoint X=56.1686 Y=-38.9742 Z=0
    g38: GeomPoint X=-56.1686 Y=-38.9742 Z=0
    g39: GeomPoint X=56.1686 Y=-38.9742 Z=0
    g40: Circle CenterX=60.2186 CenterY=-36.4924 CenterZ=0 NormalX=0 NormalY=0 NormalZ=1 AngleXU=0 Radius=1.4
    g41: Circle CenterX=52.1186 CenterY=-41.4561 CenterZ=0 NormalX=0 NormalY=0 NormalZ=1 AngleXU=0 Radius=1.4
    g42: Circle CenterX=-52.1186 CenterY=-41.4561 CenterZ=0 NormalX=0 NormalY=0 NormalZ=1 AngleXU=0 Radius=1.4
    g43: Circle CenterX=-60.2186 CenterY=-36.4924 CenterZ=0 NormalX=0 NormalY=0 NormalZ=1 AngleXU=0 Radius=1.4
  constraints (102):
    c: Vertical(g0)
    c: Vertical(g1)
    c: Horizontal(g2)
    c: Symmetric(g2,g2,g-1)
    c: Horizontal(g3)
    c: Horizontal(g4)
    c: PointOnObject(g5,g-2)
    c: Horizontal(g6)
    c: Horizontal(g7)
    c: Horizontal(g9)
    c: Coincident(g11,g-1)
    c: PointOnObject(g11,g-2)
    c: Tangent(g8,g12) = 1.5708
    c: Tangent(g9,g12) = 1.5708
    c: Tangent(g9,g13) = 1.5708
    c: Tangent(g10,g13) = 1.5708
    c: Tangent(g6,g14) = -1.5708
    c: Tangent(g0,g14) = 1.5708
    c: Tangent(g3,g15) = 1.5708
    c: Tangent(g0,g15) = 1.5708
    c: Tangent(g1,g16) = -1.5708
    c: Tangent(g4,g16) = -1.5708
    c: Tangent(g1,g17) = -1.5708
    c: Tangent(g7,g17) = 1.5708
    c: Equal(g13,g12)
    c: Symmetric(g9,g9,g11)
    c: Equal(g16,g17)
    c: Equal(g17,g14)
    c: Equal(g14,g15)
    c: PointOnObject(g18,g-2)
    c: PointOnObject(g18,g5)
    c: DistanceX(g2,g2) = 115
    c: Symmetric(g0,g0,g2)
    c: Symmetric(g1,g1,g2)
    c: Radius(g17) = 7
    c: DistanceY(g18,g9) = 170
    c: Radius(g13) = 5
    c: DistanceX(g9,g9) = 50
    c: Equal(g7,g6)
    c: Equal(g7,g4)
    c: Vertical(g19)
    c: Vertical(g20)
    c: Vertical(g21)
    c: Vertical(g22)
    c: Equal(g3,g6)
    c: Equal(g8,g10)
    c: Tangent(g5,g23) = -1.5708
    c: Tangent(g20,g23) = 1.5708
    c: Tangent(g20,g24) = 1.5708
    c: Tangent(g4,g24) = 1.5708
    c: Tangent(g5,g25) = -1.5708
    c: Tangent(g21,g25) = 1.5708
    c: Tangent(g21,g26) = 1.5708
    c: Tangent(g3,g26) = -1.5708
    c: Equal(g26,g24)
    c: Radius(g24) = 2
    c: Equal(g23,g25)
    c: Radius(g23) = 2
    c: Tangent(g7,g27) = -1.5708
    c: Tangent(g19,g27) = -1.5708
    c: Tangent(g19,g28) = -1.5708
    c: Tangent(g10,g28) = 1.5708
    c: Tangent(g6,g29) = 1.5708
    c: Tangent(g22,g29) = 1.5708
    c: Tangent(g8,g30) = 1.5708
    c: Tangent(g22,g30) = 1.5708
    c: Equal(g27,g29)
    c: Equal(g28,g30)
    c: DistanceY(g20,g20) = 2
    c: DistanceY(g19,g19) = 15
    c: DistanceY(g4,g7) = 48
    c: DistanceX(g21,g20) = 155
    c: Radius(g27) = 2
    c: Radius(g28) = 2
    c: Diameter(g5) = 225
    c: Equal(g21,g20)
    c: Coincident(g31,g5)
    c: Diameter(g31) = 215
    c: Coincident(g32,g5)
    c: PointOnObject(g32,g31)
    c: Coincident(g33,g5)
    c: PointOnObject(g33,g31)
    c: Equal(g34,g35)
    c: Symmetric(g34,g34,g32)
    c: Symmetric(g35,g35,g33)
    c: Perpendicular(g35,g33)
    c: Perpendicular(g32,g34)
    c: Coincident(g36,g33)
    c: Coincident(g37,g32)
    c: Coincident(g38,g33)
    c: Coincident(g39,g32)
    c: Angle(g-2,g32) = 0.549779
    c: Angle(g33,g-2) = 0.549779
    c: Distance(g34) = 9.5
    c: Coincident(g40,g34)
    c: Coincident(g41,g34)
    c: Coincident(g42,g35)
    c: Coincident(g43,g35)
    c: Equal(g41,g40)
    c: Equal(g41,g42)
    c: Equal(g42,g43)
    c: Diameter(g40) = 2.8
FEATURE [PartDesign::Pocket] Pocket014  label="BMPR_SwitchHoles"
  BaseFeature = -> Pocket013
  Length = 5
  Length2 = 100
  Profile = -> Sketch030
  Type = 1
FEATURE [PartDesign::Plane] DatumPlane001  label="Datum_BMPRCSunk"
  AttachmentOffset = pos=(0,0,-2) rot=(0,0,1;0rad)
  Length = 187.465
  MapMode = 5
  Placement = pos=(0,0,-2) rot=(0,0,1;0rad)
  ResizeMode = 0
  Support = -> [XY_Plane001]
  Width = 202.462
  expr: .AttachmentOffset.Base.z = -1 * <<params>>.m25_nut_min_depth
FEATURE [Sketcher::SketchObject] Sketch032  label="Sketch_BMPRStandoffHoleLocs"
  FullyConstrained = true
  MapMode = 5
  Support = -> [XY_Plane001]
  expr: Constraints[9] = <<params>>.bmpr_standoff_hole_loc_x
  expr: Constraints[8] = <<params>>.bmpr_standoff_hole_width
  expr: Constraints[7] = <<params>>.m2_hole_clear_diam
  sketch-geometry (4):
    g0: LineSegment StartX=0 StartY=0 StartZ=0 EndX=0 EndY=-48.5 EndZ=0
    g1: LineSegment StartX=-33 StartY=-48.5 StartZ=0 EndX=33 EndY=-48.5 EndZ=0
    g2: Circle CenterX=-33 CenterY=-48.5 CenterZ=0 NormalX=0 NormalY=0 NormalZ=1 AngleXU=0 Radius=1.2
    g3: Circle CenterX=33 CenterY=-48.5 CenterZ=0 NormalX=0 NormalY=0 NormalZ=1 AngleXU=0 Radius=1.2
  constraints (10):
    c: Coincident(g0,g-1)
    c: PointOnObject(g0,g-2)
    c: Horizontal(g1)
    c: Symmetric(g1,g1,g0)
    c: Coincident(g2,g1)
    c: Coincident(g3,g1)
    c: Equal(g3,g2)
    c: Diameter(g3) = 2.4
    c: DistanceX(g2,g3) = 66
    c: DistanceY(g0,g-1) = 48.5
FEATURE [PartDesign::Pocket] Pocket016  label="BMPR_StandoffHoles"
  BaseFeature = -> Pocket014
  Length = 5
  Length2 = 100
  Profile = -> Sketch032
  Type = 1
FEATURE [Sketcher::SketchObject] Sketch033  label="Sketch_PivotPlateHoles"
  FullyConstrained = true
  MapMode = 5
  Support = -> [XY_Plane001]
  expr: Constraints[9] = Spreadsheet.bmpr_pivot_hole_loc_x
  expr: Constraints[8] = <<params>>.m25_hole_clear_diam
  expr: Constraints[4] = <<params>>.bmpr_pivot_hole_width
  sketch-geometry (4):
    g0: LineSegment StartX=-7.5 StartY=-52 StartZ=0 EndX=7.5 EndY=-52 EndZ=0
    g1: LineSegment StartX=0 StartY=0 StartZ=0 EndX=0 EndY=-52 EndZ=0
    g2: Circle CenterX=-7.5 CenterY=-52 CenterZ=0 NormalX=0 NormalY=0 NormalZ=1 AngleXU=0 Radius=1.4
    g3: Circle CenterX=7.5 CenterY=-52 CenterZ=0 NormalX=0 NormalY=0 NormalZ=1 AngleXU=0 Radius=1.4
  constraints (10):
    c: Horizontal(g0)
    c: Coincident(g1,g-1)
    c: PointOnObject(g1,g-2)
    c: Symmetric(g0,g0,g1)
    c: DistanceX(g0,g0) = 15
    c: Coincident(g2,g0)
    c: Coincident(g3,g0)
    c: Equal(g3,g2)
    c: Diameter(g3) = 2.8
    c: DistanceY(g1,g1) = 52
FEATURE [PartDesign::Pocket] Pocket017  label="BMPR_PivotPlateHoles"
  BaseFeature = -> Pocket016
  Length = 5
  Length2 = 100
  Profile = -> Sketch033
  Type = 1
FEATURE [Sketcher::SketchObject] Sketch034  label="Sketch_PWRSwitchHoles"
  FullyConstrained = true
  MapMode = 5
  Support = -> [XY_Plane001]
  expr: Constraints[26] = <<params>>.pwrs_slot_leng
  expr: Constraints[29] = <<params>>.pwrs_loc_y
  expr: Constraints[30] = <<params>>.pwrs_loc_x
  expr: Constraints[28] = <<params>>.m25_hole_clear_diam
  expr: Constraints[25] = <<params>>.pwrs_hole_spacing
  expr: Constraints[27] = <<params>>.pwrs_slot_w
  expr: Constraints[23] = <<params>>.pwrs_slot_rad
  sketch-geometry (13):
    g0: LineSegment StartX=11.5 StartY=9 StartZ=0 EndX=18.5 EndY=9 EndZ=0
    g1: LineSegment StartX=19.5 StartY=8 StartZ=0 EndX=19.5 EndY=4 EndZ=0
    g2: LineSegment StartX=18.5 StartY=3 StartZ=0 EndX=11.5 EndY=3 EndZ=0
    g3: LineSegment StartX=10.5 StartY=4 StartZ=0 EndX=10.5 EndY=8 EndZ=0
    g4: ArcOfCircle CenterX=11.5 CenterY=8 CenterZ=0 NormalX=0 NormalY=0 NormalZ=1 AngleXU=0 Radius=1 StartAngle=1.5708 EndAngle=3.14159
    g5: ArcOfCircle CenterX=18.5 CenterY=8 CenterZ=0 NormalX=0 NormalY=0 NormalZ=1 AngleXU=0 Radius=1 StartAngle=2.9834e-12 EndAngle=1.5708
    g6: ArcOfCircle CenterX=18.5 CenterY=4 CenterZ=0 NormalX=0 NormalY=0 NormalZ=1 AngleXU=0 Radius=1 StartAngle=4.71239 EndAngle=6.28319
    g7: ArcOfCircle CenterX=11.5 CenterY=4 CenterZ=0 NormalX=0 NormalY=0 NormalZ=1 AngleXU=0 Radius=1 StartAngle=3.14159 EndAngle=4.71239
    g8: Circle CenterX=6.25 CenterY=6 CenterZ=0 NormalX=0 NormalY=0 NormalZ=1 AngleXU=0 Radius=1.4
    g9: Circle CenterX=23.75 CenterY=6 CenterZ=0 NormalX=0 NormalY=0 NormalZ=1 AngleXU=0 Radius=1.4
    g10: LineSegment StartX=6.25 StartY=6 StartZ=0 EndX=10.5 EndY=6 EndZ=0
    g11: LineSegment StartX=23.75 StartY=6 StartZ=0 EndX=19.5 EndY=6 EndZ=0
    g12: GeomPoint X=15 Y=6 Z=0
  constraints (31):
    c: Horizontal(g0)
    c: Horizontal(g2)
    c: Vertical(g1)
    c: Vertical(g3)
    c: Tangent(g3,g4) = 1.5708
    c: Tangent(g0,g4) = 1.5708
    c: Tangent(g0,g5) = 1.5708
    c: Tangent(g1,g5) = 1.5708
    c: Tangent(g1,g6) = 1.5708
    c: Tangent(g2,g6) = 1.5708
    c: Tangent(g2,g7) = 1.5708
    c: Tangent(g3,g7) = 1.5708
    c: Equal(g4,g5)
    c: Equal(g5,g6)
    c: Equal(g6,g7)
    c: Equal(g8,g9)
    c: Coincident(g10,g8)
    c: Horizontal(g10)
    c: Coincident(g11,g9)
    c: Horizontal(g11)
    c: Symmetric(g3,g3,g10)
    c: Symmetric(g1,g1,g11)
    c: Equal(g11,g10)
    c: Radius(g5) = 1
    c: Symmetric(g5,g7,g12)
    c: DistanceX(g8,g9) = 17.5
    c: DistanceX(g3,g1) = 9
    c: DistanceY(g2,g0) = 6
    c: Diameter(g9) = 2.8
    c: DistanceY(g-1,g12) = 6
    c: DistanceX(g-1,g12) = 15
FEATURE [PartDesign::Pocket] Pocket018  label="PWR_Switch_Holes"
  BaseFeature = -> Pocket017
  Length = 5
  Length2 = 100
  Profile = -> Sketch034
  Type = 1
FEATURE [Sketcher::SketchObject] Sketch035  label="Sketch_BMPRCSunk"
  FullyConstrained = true
  MapMode = 5
  Placement = pos=(0,0,-2) rot=(0,0,1;0rad)
  Support = -> [DatumPlane001]
  expr: Constraints[174] = <<params>>.m25_nut_clear_flat
  expr: Constraints[73] = <<params>>.std_rad
  expr: Constraints[55] = <<params>>.std_rad
  expr: Constraints[70] = <<params>>.wheel_well_clearance
  expr: Constraints[31] = <<params>>.wheel_well_plate_width
  expr: Constraints[35] = <<params>>.plate_length
  expr: Constraints[37] = <<params>>.tail_width
  expr: Constraints[36] = <<params>>.tail_rad
  expr: Constraints[74] = <<params>>.front_diameter
  expr: Constraints[71] = <<params>>.plate_width
  expr: Constraints[69] = <<params>>.back_vert_edge
  expr: Constraints[68] = <<params>>.front_vert_edge
  expr: Constraints[92] = <<params>>.bmpr_switch_ang
  expr: Constraints[91] = <<params>>.bmpr_switch_ang
  expr: Constraints[72] = <<params>>.std_rad
  expr: Constraints[57] = <<params>>.std_rad
  expr: Constraints[77] = <<params>>.front_diameter - 2 * <<params>>.bmpr_switch_diam_offset
  expr: Constraints[93] = <<params>>.bmpr_switch_hole_space
  sketch-geometry (69):
    g0: LineSegment StartX=-57.5 StartY=17 StartZ=0 EndX=-57.5 EndY=-17 EndZ=0
    g1: LineSegment StartX=57.5 StartY=17 StartZ=0 EndX=57.5 EndY=-17 EndZ=0
    g2: LineSegment StartX=-57.5 StartY=0 StartZ=0 EndX=57.5 EndY=0 EndZ=0
    g3: LineSegment StartX=-64.5 StartY=-24 StartZ=0 EndX=-75.5 EndY=-24 EndZ=0
    g4: LineSegment StartX=64.5 StartY=-24 StartZ=0 EndX=75.5 EndY=-24 EndZ=0
    g5: ArcOfCircle CenterX=0 CenterY=52.6846 CenterZ=0 NormalX=0 NormalY=0 NormalZ=1 AngleXU=0 Radius=112.5 StartAngle=3.96017 EndAngle=5.4646
    g6: LineSegment StartX=-64.5 StartY=24 StartZ=0 EndX=-75.5 EndY=24 EndZ=0
    g7: LineSegment StartX=64.5 StartY=24 StartZ=0 EndX=75.5 EndY=24 EndZ=0
    g8: LineSegment StartX=-77.1162 StartY=42.1781 StartZ=0 EndX=-29.0404 EndY=108.13 EndZ=0
    g9: LineSegment StartX=-25 StartY=110.185 StartZ=0 EndX=25 EndY=110.185 EndZ=0
    g10: LineSegment StartX=29.0404 StartY=108.13 StartZ=0 EndX=77.1162 EndY=42.1781 EndZ=0
    g11: LineSegment StartX=0 StartY=0 StartZ=0 EndX=0 EndY=110.185 EndZ=0
    g12: ArcOfCircle CenterX=-25 CenterY=105.185 CenterZ=0 NormalX=0 NormalY=0 NormalZ=1 AngleXU=0 Radius=5 StartAngle=1.5708 EndAngle=2.5117
    g13: ArcOfCircle CenterX=25 CenterY=105.185 CenterZ=0 NormalX=0 NormalY=0 NormalZ=1 AngleXU=0 Radius=5 StartAngle=0.629894 EndAngle=1.5708
    g14: ArcOfCircle CenterX=-64.5 CenterY=17 CenterZ=0 NormalX=0 NormalY=0 NormalZ=1 AngleXU=0 Radius=7 StartAngle=0 EndAngle=1.5708
    g15: ArcOfCircle CenterX=-64.5 CenterY=-17 CenterZ=0 NormalX=0 NormalY=0 NormalZ=1 AngleXU=0 Radius=7 StartAngle=4.71239 EndAngle=6.28319
    g16: ArcOfCircle CenterX=64.5 CenterY=-17 CenterZ=0 NormalX=0 NormalY=0 NormalZ=1 AngleXU=0 Radius=7 StartAngle=3.14159 EndAngle=4.71239
    g17: ArcOfCircle CenterX=64.5 CenterY=17 CenterZ=0 NormalX=0 NormalY=0 NormalZ=1 AngleXU=0 Radius=7 StartAngle=1.5708 EndAngle=3.14159
    g18: GeomPoint X=0 Y=-59.8154 Z=0
    g19: LineSegment StartX=77.5 StartY=26 StartZ=0 EndX=77.5 EndY=41 EndZ=0
    g20: LineSegment StartX=77.5 StartY=-26 StartZ=0 EndX=77.5 EndY=-28 EndZ=0
    g21: LineSegment StartX=-77.5 StartY=-28 StartZ=0 EndX=-77.5 EndY=-26 EndZ=0
    g22: LineSegment StartX=-77.5 StartY=26 StartZ=0 EndX=-77.5 EndY=41 EndZ=0
    g23: ArcOfCircle CenterX=75.5 CenterY=-28 CenterZ=0 NormalX=0 NormalY=0 NormalZ=1 AngleXU=0 Radius=2 StartAngle=5.4646 EndAngle=6.28319
    g24: ArcOfCircle CenterX=75.5 CenterY=-26 CenterZ=0 NormalX=0 NormalY=0 NormalZ=1 AngleXU=0 Radius=2 StartAngle=0 EndAngle=1.5708
    g25: ArcOfCircle CenterX=-75.5 CenterY=-28 CenterZ=0 NormalX=0 NormalY=0 NormalZ=1 AngleXU=0 Radius=2 StartAngle=3.14159 EndAngle=3.96017
    g26: ArcOfCircle CenterX=-75.5 CenterY=-26 CenterZ=0 NormalX=0 NormalY=0 NormalZ=1 AngleXU=0 Radius=2 StartAngle=1.5708 EndAngle=3.14159
    g27: ArcOfCircle CenterX=75.5 CenterY=26 CenterZ=0 NormalX=0 NormalY=0 NormalZ=1 AngleXU=0 Radius=2 StartAngle=4.71239 EndAngle=6.28319
    g28: ArcOfCircle CenterX=75.5 CenterY=41 CenterZ=0 NormalX=0 NormalY=0 NormalZ=1 AngleXU=0 Radius=2 StartAngle=-9e-16 EndAngle=0.629894
    g29: ArcOfCircle CenterX=-75.5 CenterY=26 CenterZ=0 NormalX=0 NormalY=0 NormalZ=1 AngleXU=0 Radius=2 StartAngle=3.14159 EndAngle=4.71239
    g30: ArcOfCircle CenterX=-75.5 CenterY=41 CenterZ=0 NormalX=0 NormalY=0 NormalZ=1 AngleXU=0 Radius=2 StartAngle=2.5117 EndAngle=3.14159
    g31: Circle CenterX=0 CenterY=52.6846 CenterZ=0 NormalX=0 NormalY=0 NormalZ=1 AngleXU=0 Radius=107.5
    g32: LineSegment StartX=0 StartY=52.6846 StartZ=0 EndX=56.1686 EndY=-38.9742 EndZ=0
    g33: LineSegment StartX=0 StartY=52.6846 StartZ=0 EndX=-56.1686 EndY=-38.9742 EndZ=0
    g34: LineSegment StartX=52.1186 StartY=-41.4561 StartZ=0 EndX=60.2186 EndY=-36.4924 EndZ=0
    g35: LineSegment StartX=-52.1186 StartY=-41.4561 StartZ=0 EndX=-60.2186 EndY=-36.4924 EndZ=0
    g36: GeomPoint X=-56.1686 Y=-38.9742 Z=0
    g37: GeomPoint X=56.1686 Y=-38.9742 Z=0
    g38: GeomPoint X=-56.1686 Y=-38.9742 Z=0
    g39: GeomPoint X=56.1686 Y=-38.9742 Z=0
    g40: LineSegment StartX=57.6588 StartY=-38.061 StartZ=0 EndX=60.2972 EndY=-39.4936 EndZ=0
    g41: LineSegment StartX=60.2972 StartY=-39.4936 StartZ=0 EndX=62.857 EndY=-37.9249 EndZ=0
    g42: LineSegment StartX=62.857 StartY=-37.9249 StartZ=0 EndX=62.7785 EndY=-34.9237 EndZ=0
    g43: LineSegment StartX=62.7785 StartY=-34.9237 StartZ=0 EndX=60.14 EndY=-33.4912 EndZ=0
    g44: LineSegment StartX=60.14 StartY=-33.4912 StartZ=0 EndX=57.5802 EndY=-35.0598 EndZ=0
    g45: LineSegment StartX=57.5802 StartY=-35.0598 StartZ=0 EndX=57.6588 EndY=-38.061 EndZ=0
    g46: Circle CenterX=60.2186 CenterY=-36.4924 CenterZ=0 NormalX=0 NormalY=0 NormalZ=1 AngleXU=0 Radius=3.00222
    g47: LineSegment StartX=54.6784 StartY=-39.8875 StartZ=0 EndX=52.04 EndY=-38.4549 EndZ=0
    g48: LineSegment StartX=52.04 StartY=-38.4549 StartZ=0 EndX=49.4802 EndY=-40.0236 EndZ=0
    g49: LineSegment StartX=49.4802 StartY=-40.0236 StartZ=0 EndX=49.5587 EndY=-43.0248 EndZ=0
    g50: LineSegment StartX=49.5587 StartY=-43.0248 StartZ=0 EndX=52.1971 EndY=-44.4573 EndZ=0
    g51: LineSegment StartX=52.1971 StartY=-44.4573 StartZ=0 EndX=54.757 EndY=-42.8887 EndZ=0
    g52: LineSegment StartX=54.757 StartY=-42.8887 StartZ=0 EndX=54.6784 EndY=-39.8875 EndZ=0
    g53: Circle CenterX=52.1186 CenterY=-41.4561 CenterZ=0 NormalX=0 NormalY=0 NormalZ=1 AngleXU=0 Radius=3.00222
    g54: LineSegment StartX=-54.6784 StartY=-39.8875 StartZ=0 EndX=-54.757 EndY=-42.8887 EndZ=0
    g55: LineSegment StartX=-54.757 StartY=-42.8887 StartZ=0 EndX=-52.1971 EndY=-44.4573 EndZ=0
    g56: LineSegment StartX=-52.1971 StartY=-44.4573 StartZ=0 EndX=-49.5587 EndY=-43.0248 EndZ=0
    g57: LineSegment StartX=-49.5587 StartY=-43.0248 StartZ=0 EndX=-49.4802 EndY=-40.0236 EndZ=0
    g58: LineSegment StartX=-49.4802 StartY=-40.0236 StartZ=0 EndX=-52.04 EndY=-38.4549 EndZ=0
    g59: LineSegment StartX=-52.04 StartY=-38.4549 StartZ=0 EndX=-54.6784 EndY=-39.8875 EndZ=0
    g60: Circle CenterX=-52.1186 CenterY=-41.4561 CenterZ=0 NormalX=0 NormalY=0 NormalZ=1 AngleXU=0 Radius=3.00222
    g61: LineSegment StartX=-57.6588 StartY=-38.061 StartZ=0 EndX=-57.5802 EndY=-35.0598 EndZ=0
    g62: LineSegment StartX=-57.5802 StartY=-35.0598 StartZ=0 EndX=-60.14 EndY=-33.4912 EndZ=0
    g63: LineSegment StartX=-60.14 StartY=-33.4912 StartZ=0 EndX=-62.7785 EndY=-34.9237 EndZ=0
    g64: LineSegment StartX=-62.7785 StartY=-34.9237 StartZ=0 EndX=-62.857 EndY=-37.9249 EndZ=0
    g65: LineSegment StartX=-62.857 StartY=-37.9249 StartZ=0 EndX=-60.2972 EndY=-39.4936 EndZ=0
    g66: LineSegment StartX=-60.2972 StartY=-39.4936 StartZ=0 EndX=-57.6588 EndY=-38.061 EndZ=0
    g67: Circle CenterX=-60.2186 CenterY=-36.4924 CenterZ=0 NormalX=0 NormalY=0 NormalZ=1 AngleXU=0 Radius=3.00222
    g68: LineSegment StartX=60.14 StartY=-33.4912 StartZ=0 EndX=62.857 EndY=-37.9249 EndZ=0
  constraints (160):
    c: Vertical(g0)
    c: Vertical(g1)
    c: Horizontal(g2)
    c: Symmetric(g2,g2,g-1)
    c: Horizontal(g3)
    c: Horizontal(g4)
    c: PointOnObject(g5,g-2)
    c: Horizontal(g6)
    c: Horizontal(g7)
    c: Horizontal(g9)
    c: Coincident(g11,g-1)
    c: PointOnObject(g11,g-2)
    c: Tangent(g8,g12) = 1.5708
    c: Tangent(g9,g12) = 1.5708
    c: Tangent(g9,g13) = 1.5708
    c: Tangent(g10,g13) = 1.5708
    c: Tangent(g6,g14) = -1.5708
    c: Tangent(g0,g14) = 1.5708
    c: Tangent(g3,g15) = 1.5708
    c: Tangent(g0,g15) = 1.5708
    c: Tangent(g1,g16) = -1.5708
    c: Tangent(g4,g16) = -1.5708
    c: Tangent(g1,g17) = -1.5708
    c: Tangent(g7,g17) = 1.5708
    c: Equal(g13,g12)
    c: Symmetric(g9,g9,g11)
    c: Equal(g16,g17)
    c: Equal(g17,g14)
    c: Equal(g14,g15)
    c: PointOnObject(g18,g-2)
    c: PointOnObject(g18,g5)
    c: DistanceX(g2,g2) = 115
    c: Symmetric(g0,g0,g2)
    c: Symmetric(g1,g1,g2)
    c: Radius(g17) = 7
    c: DistanceY(g18,g9) = 170
    c: Radius(g13) = 5
    c: DistanceX(g9,g9) = 50
    c: Equal(g7,g6)
    c: Equal(g7,g4)
    c: Vertical(g19)
    c: Vertical(g20)
    c: Vertical(g21)
    c: Vertical(g22)
    c: Equal(g3,g6)
    c: Equal(g8,g10)
    c: Tangent(g5,g23) = -1.5708
    c: Tangent(g20,g23) = 1.5708
    c: Tangent(g20,g24) = 1.5708
    c: Tangent(g4,g24) = 1.5708
    c: Tangent(g5,g25) = -1.5708
    c: Tangent(g21,g25) = 1.5708
    c: Tangent(g21,g26) = 1.5708
    c: Tangent(g3,g26) = -1.5708
    c: Equal(g26,g24)
    c: Radius(g24) = 2
    c: Equal(g23,g25)
    c: Radius(g23) = 2
    c: Tangent(g7,g27) = -1.5708
    c: Tangent(g19,g27) = -1.5708
    c: Tangent(g19,g28) = -1.5708
    c: Tangent(g10,g28) = 1.5708
    c: Tangent(g6,g29) = 1.5708
    c: Tangent(g22,g29) = 1.5708
    c: Tangent(g8,g30) = 1.5708
    c: Tangent(g22,g30) = 1.5708
    c: Equal(g27,g29)
    c: Equal(g28,g30)
    c: DistanceY(g20,g20) = 2
    c: DistanceY(g19,g19) = 15
    c: DistanceY(g4,g7) = 48
    c: DistanceX(g21,g20) = 155
    c: Radius(g27) = 2
    c: Radius(g28) = 2
    c: Diameter(g5) = 225
    c: Equal(g21,g20)
    c: Coincident(g31,g5)
    c: Diameter(g31) = 215
    c: Coincident(g32,g5)
    c: PointOnObject(g32,g31)
    c: Coincident(g33,g5)
    c: PointOnObject(g33,g31)
    c: Equal(g34,g35)
    c: Symmetric(g34,g34,g32)
    c: Symmetric(g35,g35,g33)
    c: Perpendicular(g35,g33)
    c: Perpendicular(g32,g34)
    c: Coincident(g36,g33)
    c: Coincident(g37,g32)
    c: Coincident(g38,g33)
    c: Coincident(g39,g32)
    c: Angle(g-2,g32) = 0.549779
    c: Angle(g33,g-2) = 0.549779
    c: Distance(g34) = 9.5
    c: Coincident(g40,g41)
    c: Coincident(g41,g42)
    c: Coincident(g42,g43)
    c: Coincident(g43,g44)
    c: Coincident(g44,g45)
    c: Coincident(g45,g40)
    c: Equal(g40, g41-g45) x5
    c: PointOnObject(g40,g46)
    c: PointOnObject(g41,g46)
    c: PointOnObject(g42,g46)
    c: PointOnObject(g43,g46)
    c: PointOnObject(g44,g46)
    c: PointOnObject(g45,g46)
    c: Coincident(g46,g34)
    c: PointOnObject(g45,g34)
    c: Coincident(g47,g48)
    c: Coincident(g48,g49)
    c: Coincident(g49,g50)
    c: Coincident(g50,g51)
    c: Coincident(g51,g52)
    c: Coincident(g52,g47)
    c: Equal(g47, g48-g52) x5
    c: PointOnObject(g47,g53)
    c: PointOnObject(g48,g53)
    c: PointOnObject(g49,g53)
    c: PointOnObject(g50,g53)
    c: PointOnObject(g51,g53)
    c: PointOnObject(g52,g53)
    c: Coincident(g53,g34)
    c: PointOnObject(g52,g34)
    c: Coincident(g54,g55)
    c: Coincident(g55,g56)
    c: Coincident(g56,g57)
    c: Coincident(g57,g58)
    c: Coincident(g58,g59)
    c: Coincident(g59,g54)
    c: Equal(g54, g55-g59) x5
    c: PointOnObject(g54,g60)
    c: PointOnObject(g55,g60)
    c: PointOnObject(g56,g60)
    c: PointOnObject(g57,g60)
    c: PointOnObject(g58,g60)
    c: PointOnObject(g59,g60)
    c: PointOnObject(g59,g35)
    c: Coincident(g61,g62)
    c: Coincident(g62,g63)
    c: Coincident(g63,g64)
    c: Coincident(g64,g65)
    c: Coincident(g65,g66)
    c: Coincident(g66,g61)
    c: Equal(g61, g62-g66) x5
    c: PointOnObject(g61,g67)
    c: PointOnObject(g62,g67)
    c: PointOnObject(g63,g67)
    c: PointOnObject(g64,g67)
    c: PointOnObject(g65,g67)
    c: PointOnObject(g66,g67)
    c: Coincident(g67,g35)
    c: PointOnObject(g66,g35)
    c: Equal(g67,g60)
    c: Equal(g60,g53)
    c: Equal(g53,g46)
    c: Coincident(g68,g43)
    c: Coincident(g68,g41)
    c: Distance(g68) = 5.2
    c: Coincident(g60,g35)
FEATURE [PartDesign::Pocket] Pocket019  label="BMPR_SwitchCSunk"
  BaseFeature = -> Pocket018
  Length = 5
  Length2 = 100
  Profile = -> Sketch035
  Reversed = true
  Type = 1
FEATURE [Sketcher::SketchObject] Sketch036  label="Sketch_LSRHoles"
  FullyConstrained = true
  MapMode = 5
  Support = -> [XY_Plane001]
  expr: Constraints[55] = <<params>>.std_rad
  expr: Constraints[70] = <<params>>.wheel_well_clearance
  expr: Constraints[31] = <<params>>.wheel_well_plate_width
  expr: Constraints[73] = <<params>>.std_rad
  expr: Constraints[35] = <<params>>.plate_length
  expr: Constraints[37] = <<params>>.tail_width
  expr: Constraints[36] = <<params>>.tail_rad
  expr: Constraints[74] = <<params>>.front_diameter
  expr: Constraints[71] = <<params>>.plate_width
  expr: Constraints[69] = <<params>>.back_vert_edge
  expr: Constraints[68] = <<params>>.front_vert_edge
  expr: Constraints[92] = <<params>>.bmpr_switch_ang
  expr: Constraints[91] = <<params>>.bmpr_switch_ang
  expr: Constraints[72] = <<params>>.std_rad
  expr: Constraints[57] = <<params>>.std_rad
  expr: Constraints[77] = <<params>>.front_diameter - 2 * <<params>>.lsr_mt_diam_offset
  expr: Constraints[93] = <<params>>.lsr_mt_width
  expr: Constraints[101] = <<params>>.m25_hole_clear_diam
  sketch-geometry (44):
    g0: LineSegment StartX=-57.5 StartY=17 StartZ=0 EndX=-57.5 EndY=-17 EndZ=0
    g1: LineSegment StartX=57.5 StartY=17 StartZ=0 EndX=57.5 EndY=-17 EndZ=0
    g2: LineSegment StartX=-57.5 StartY=0 StartZ=0 EndX=57.5 EndY=0 EndZ=0
    g3: LineSegment StartX=-64.5 StartY=-24 StartZ=0 EndX=-75.5 EndY=-24 EndZ=0
    g4: LineSegment StartX=64.5 StartY=-24 StartZ=0 EndX=75.5 EndY=-24 EndZ=0
    g5: ArcOfCircle CenterX=0 CenterY=52.6846 CenterZ=0 NormalX=0 NormalY=0 NormalZ=1 AngleXU=0 Radius=112.5 StartAngle=3.96017 EndAngle=5.4646
    g6: LineSegment StartX=-64.5 StartY=24 StartZ=0 EndX=-75.5 EndY=24 EndZ=0
    g7: LineSegment StartX=64.5 StartY=24 StartZ=0 EndX=75.5 EndY=24 EndZ=0
    g8: LineSegment StartX=-77.1162 StartY=42.1781 StartZ=0 EndX=-29.0404 EndY=108.13 EndZ=0
    g9: LineSegment StartX=-25 StartY=110.185 StartZ=0 EndX=25 EndY=110.185 EndZ=0
    g10: LineSegment StartX=29.0404 StartY=108.13 StartZ=0 EndX=77.1162 EndY=42.1781 EndZ=0
    g11: LineSegment StartX=0 StartY=0 StartZ=0 EndX=0 EndY=110.185 EndZ=0
    g12: ArcOfCircle CenterX=-25 CenterY=105.185 CenterZ=0 NormalX=0 NormalY=0 NormalZ=1 AngleXU=0 Radius=5 StartAngle=1.5708 EndAngle=2.5117
    g13: ArcOfCircle CenterX=25 CenterY=105.185 CenterZ=0 NormalX=0 NormalY=0 NormalZ=1 AngleXU=0 Radius=5 StartAngle=0.629894 EndAngle=1.5708
    g14: ArcOfCircle CenterX=-64.5 CenterY=17 CenterZ=0 NormalX=0 NormalY=0 NormalZ=1 AngleXU=0 Radius=7 StartAngle=1e-16 EndAngle=1.5708
    g15: ArcOfCircle CenterX=-64.5 CenterY=-17 CenterZ=0 NormalX=0 NormalY=0 NormalZ=1 AngleXU=0 Radius=7 StartAngle=4.71239 EndAngle=6.28319
    g16: ArcOfCircle CenterX=64.5 CenterY=-17 CenterZ=0 NormalX=0 NormalY=0 NormalZ=1 AngleXU=0 Radius=7 StartAngle=3.14159 EndAngle=4.71239
    g17: ArcOfCircle CenterX=64.5 CenterY=17 CenterZ=0 NormalX=0 NormalY=0 NormalZ=1 AngleXU=0 Radius=7 StartAngle=1.5708 EndAngle=3.14159
    g18: GeomPoint X=0 Y=-59.8154 Z=0
    g19: LineSegment StartX=77.5 StartY=26 StartZ=0 EndX=77.5 EndY=41 EndZ=0
    g20: LineSegment StartX=77.5 StartY=-26 StartZ=0 EndX=77.5 EndY=-28 EndZ=0
    g21: LineSegment StartX=-77.5 StartY=-28 StartZ=0 EndX=-77.5 EndY=-26 EndZ=0
    g22: LineSegment StartX=-77.5 StartY=26 StartZ=0 EndX=-77.5 EndY=41 EndZ=0
    g23: ArcOfCircle CenterX=75.5 CenterY=-28 CenterZ=0 NormalX=0 NormalY=0 NormalZ=1 AngleXU=0 Radius=2 StartAngle=5.4646 EndAngle=6.28319
    g24: ArcOfCircle CenterX=75.5 CenterY=-26 CenterZ=0 NormalX=0 NormalY=0 NormalZ=1 AngleXU=0 Radius=2 StartAngle=0 EndAngle=1.5708
    g25: ArcOfCircle CenterX=-75.5 CenterY=-28 CenterZ=0 NormalX=0 NormalY=0 NormalZ=1 AngleXU=0 Radius=2 StartAngle=3.14159 EndAngle=3.96017
    g26: ArcOfCircle CenterX=-75.5 CenterY=-26 CenterZ=0 NormalX=0 NormalY=0 NormalZ=1 AngleXU=0 Radius=2 StartAngle=1.5708 EndAngle=3.14159
    g27: ArcOfCircle CenterX=75.5 CenterY=26 CenterZ=0 NormalX=0 NormalY=0 NormalZ=1 AngleXU=0 Radius=2 StartAngle=4.71239 EndAngle=6.28319
    g28: ArcOfCircle CenterX=75.5 CenterY=41 CenterZ=0 NormalX=0 NormalY=0 NormalZ=1 AngleXU=0 Radius=2 StartAngle=-9e-16 EndAngle=0.629894
    g29: ArcOfCircle CenterX=-75.5 CenterY=26 CenterZ=0 NormalX=0 NormalY=0 NormalZ=1 AngleXU=0 Radius=2 StartAngle=3.14159 EndAngle=4.71239
    g30: ArcOfCircle CenterX=-75.5 CenterY=41 CenterZ=0 NormalX=0 NormalY=0 NormalZ=1 AngleXU=0 Radius=2 StartAngle=2.5117 EndAngle=3.14159
    g31: Circle CenterX=0 CenterY=52.6846 CenterZ=0 NormalX=0 NormalY=0 NormalZ=1 AngleXU=0 Radius=95
    g32: LineSegment StartX=0 StartY=52.6846 StartZ=0 EndX=49.6374 EndY=-28.3162 EndZ=0
    g33: LineSegment StartX=0 StartY=52.6846 StartZ=0 EndX=-49.6374 EndY=-28.3162 EndZ=0
    g34: LineSegment StartX=46.2268 StartY=-30.4062 StartZ=0 EndX=53.0479 EndY=-26.2263 EndZ=0
    g35: LineSegment StartX=-46.2268 StartY=-30.4062 StartZ=0 EndX=-53.0479 EndY=-26.2263 EndZ=0
    g36: GeomPoint X=-49.6374 Y=-28.3162 Z=0
    g37: GeomPoint X=49.6374 Y=-28.3162 Z=0
    g38: GeomPoint X=-49.6374 Y=-28.3162 Z=0
    g39: GeomPoint X=49.6374 Y=-28.3162 Z=0
    g40: Circle CenterX=53.0479 CenterY=-26.2263 CenterZ=0 NormalX=0 NormalY=0 NormalZ=1 AngleXU=0 Radius=1.4
    g41: Circle CenterX=46.2268 CenterY=-30.4062 CenterZ=0 NormalX=0 NormalY=0 NormalZ=1 AngleXU=0 Radius=1.4
    g42: Circle CenterX=-46.2268 CenterY=-30.4062 CenterZ=0 NormalX=0 NormalY=0 NormalZ=1 AngleXU=0 Radius=1.4
    g43: Circle CenterX=-53.0479 CenterY=-26.2263 CenterZ=0 NormalX=0 NormalY=0 NormalZ=1 AngleXU=0 Radius=1.4
  constraints (102):
    c: Vertical(g0)
    c: Vertical(g1)
    c: Horizontal(g2)
    c: Symmetric(g2,g2,g-1)
    c: Horizontal(g3)
    c: Horizontal(g4)
    c: PointOnObject(g5,g-2)
    c: Horizontal(g6)
    c: Horizontal(g7)
    c: Horizontal(g9)
    c: Coincident(g11,g-1)
    c: PointOnObject(g11,g-2)
    c: Tangent(g8,g12) = 1.5708
    c: Tangent(g9,g12) = 1.5708
    c: Tangent(g9,g13) = 1.5708
    c: Tangent(g10,g13) = 1.5708
    c: Tangent(g6,g14) = -1.5708
    c: Tangent(g0,g14) = 1.5708
    c: Tangent(g3,g15) = 1.5708
    c: Tangent(g0,g15) = 1.5708
    c: Tangent(g1,g16) = -1.5708
    c: Tangent(g4,g16) = -1.5708
    c: Tangent(g1,g17) = -1.5708
    c: Tangent(g7,g17) = 1.5708
    c: Equal(g13,g12)
    c: Symmetric(g9,g9,g11)
    c: Equal(g16,g17)
    c: Equal(g17,g14)
    c: Equal(g14,g15)
    c: PointOnObject(g18,g-2)
    c: PointOnObject(g18,g5)
    c: DistanceX(g2,g2) = 115
    c: Symmetric(g0,g0,g2)
    c: Symmetric(g1,g1,g2)
    c: Radius(g17) = 7
    c: DistanceY(g18,g9) = 170
    c: Radius(g13) = 5
    c: DistanceX(g9,g9) = 50
    c: Equal(g7,g6)
    c: Equal(g7,g4)
    c: Vertical(g19)
    c: Vertical(g20)
    c: Vertical(g21)
    c: Vertical(g22)
    c: Equal(g3,g6)
    c: Equal(g8,g10)
    c: Tangent(g5,g23) = -1.5708
    c: Tangent(g20,g23) = 1.5708
    c: Tangent(g20,g24) = 1.5708
    c: Tangent(g4,g24) = 1.5708
    c: Tangent(g5,g25) = -1.5708
    c: Tangent(g21,g25) = 1.5708
    c: Tangent(g21,g26) = 1.5708
    c: Tangent(g3,g26) = -1.5708
    c: Equal(g26,g24)
    c: Radius(g24) = 2
    c: Equal(g23,g25)
    c: Radius(g23) = 2
    c: Tangent(g7,g27) = -1.5708
    c: Tangent(g19,g27) = -1.5708
    c: Tangent(g19,g28) = -1.5708
    c: Tangent(g10,g28) = 1.5708
    c: Tangent(g6,g29) = 1.5708
    c: Tangent(g22,g29) = 1.5708
    c: Tangent(g8,g30) = 1.5708
    c: Tangent(g22,g30) = 1.5708
    c: Equal(g27,g29)
    c: Equal(g28,g30)
    c: DistanceY(g20,g20) = 2
    c: DistanceY(g19,g19) = 15
    c: DistanceY(g4,g7) = 48
    c: DistanceX(g21,g20) = 155
    c: Radius(g27) = 2
    c: Radius(g28) = 2
    c: Diameter(g5) = 225
    c: Equal(g21,g20)
    c: Coincident(g31,g5)
    c: Diameter(g31) = 190
    c: Coincident(g32,g5)
    c: PointOnObject(g32,g31)
    c: Coincident(g33,g5)
    c: PointOnObject(g33,g31)
    c: Equal(g34,g35)
    c: Symmetric(g34,g34,g32)
    c: Symmetric(g35,g35,g33)
    c: Perpendicular(g35,g33)
    c: Perpendicular(g32,g34)
    c: Coincident(g36,g33)
    c: Coincident(g37,g32)
    c: Coincident(g38,g33)
    c: Coincident(g39,g32)
    c: Angle(g-2,g32) = 0.549779
    c: Angle(g33,g-2) = 0.549779
    c: Distance(g34) = 8
    c: Coincident(g40,g34)
    c: Coincident(g41,g34)
    c: Coincident(g42,g35)
    c: Coincident(g43,g35)
    c: Equal(g41,g40)
    c: Equal(g41,g42)
    c: Equal(g42,g43)
    c: Diameter(g40) = 2.8
FEATURE [PartDesign::Pocket] Pocket020  label="LSR_MtHoles"
  BaseFeature = -> Pocket019
  Length = 5
  Length2 = 100
  Profile = -> Sketch036
  Type = 1
FEATURE [Sketcher::SketchObject] Sketch037
  FullyConstrained = true
  MapMode = 5
  Support = -> [XY_Plane001]
  expr: Constraints[43] = <<params>>.bmpr_grove_hole_loc_x
  expr: Constraints[42] = <<params>>.bmpr_grove_hole_spacing_width
  expr: Constraints[41] = <<params>>.bmpr_grove_hole_leng
  expr: Constraints[40] = <<params>>.bmpr_grove_hole_width
  expr: Constraints[31] = <<params>>.std_rad / 2
  sketch-geometry (18):
    g0: LineSegment StartX=-38 StartY=-27 StartZ=0 EndX=-35 EndY=-27 EndZ=0
    g1: LineSegment StartX=-34 StartY=-28 StartZ=0 EndX=-34 EndY=-36 EndZ=0
    g2: LineSegment StartX=-35 StartY=-37 StartZ=0 EndX=-38 EndY=-37 EndZ=0
    g3: LineSegment StartX=-39 StartY=-36 StartZ=0 EndX=-39 EndY=-28 EndZ=0
    g4: LineSegment StartX=35 StartY=-27 StartZ=0 EndX=38 EndY=-27 EndZ=0
    g5: LineSegment StartX=39 StartY=-28 StartZ=0 EndX=39 EndY=-36 EndZ=0
    g6: LineSegment StartX=38 StartY=-37 StartZ=0 EndX=35 EndY=-37 EndZ=0
    g7: LineSegment StartX=34 StartY=-36 StartZ=0 EndX=34 EndY=-28 EndZ=0
    g8: ArcOfCircle CenterX=-35 CenterY=-28 CenterZ=0 NormalX=0 NormalY=0 NormalZ=1 AngleXU=0 Radius=1 StartAngle=-1.8e-15 EndAngle=1.5708
    g9: ArcOfCircle CenterX=-38 CenterY=-28 CenterZ=0 NormalX=0 NormalY=0 NormalZ=1 AngleXU=0 Radius=1 StartAngle=1.5708 EndAngle=3.14159
    g10: ArcOfCircle CenterX=-38 CenterY=-36 CenterZ=0 NormalX=0 NormalY=0 NormalZ=1 AngleXU=0 Radius=1 StartAngle=3.14159 EndAngle=4.71239
    g11: ArcOfCircle CenterX=-35 CenterY=-36 CenterZ=0 NormalX=0 NormalY=0 NormalZ=1 AngleXU=0 Radius=1 StartAngle=4.71239 EndAngle=6.28319
    g12: ArcOfCircle CenterX=35 CenterY=-28 CenterZ=0 NormalX=0 NormalY=0 NormalZ=1 AngleXU=0 Radius=1 StartAngle=1.5708 EndAngle=3.14159
    g13: ArcOfCircle CenterX=38 CenterY=-28 CenterZ=0 NormalX=0 NormalY=0 NormalZ=1 AngleXU=0 Radius=1 StartAngle=-1.8e-15 EndAngle=1.5708
    g14: ArcOfCircle CenterX=35 CenterY=-36 CenterZ=0 NormalX=0 NormalY=0 NormalZ=1 AngleXU=0 Radius=1 StartAngle=3.14159 EndAngle=4.71239
    g15: ArcOfCircle CenterX=38 CenterY=-36 CenterZ=0 NormalX=0 NormalY=0 NormalZ=1 AngleXU=0 Radius=1 StartAngle=4.71239 EndAngle=6.28319
    g16: LineSegment StartX=0 StartY=0 StartZ=0 EndX=0 EndY=-32 EndZ=0
    g17: LineSegment StartX=-34 StartY=-32 StartZ=0 EndX=34 EndY=-32 EndZ=0
  constraints (44):
    c: Horizontal(g0)
    c: Horizontal(g2)
    c: Vertical(g1)
    c: Vertical(g3)
    c: Horizontal(g4)
    c: Horizontal(g6)
    c: Vertical(g5)
    c: Vertical(g7)
    c: Tangent(g1,g8) = 1.5708
    c: Tangent(g0,g8) = 1.5708
    c: Tangent(g0,g9) = 1.5708
    c: Tangent(g3,g9) = 1.5708
    c: Tangent(g3,g10) = 1.5708
    c: Tangent(g2,g10) = 1.5708
    c: Tangent(g2,g11) = 1.5708
    c: Tangent(g1,g11) = 1.5708
    c: Tangent(g7,g12) = 1.5708
    c: Tangent(g4,g12) = 1.5708
    c: Tangent(g5,g13) = 1.5708
    c: Tangent(g4,g13) = 1.5708
    c: Tangent(g7,g14) = 1.5708
    c: Tangent(g6,g14) = 1.5708
    c: Tangent(g6,g15) = 1.5708
    c: Tangent(g5,g15) = 1.5708
    c: Equal(g15,g14)
    c: Equal(g14,g12)
    c: Equal(g12,g13)
    c: Equal(g12,g8)
    c: Equal(g8,g11)
    c: Equal(g11,g10)
    c: Equal(g10,g9)
    c: Radius(g13) = 1
    c: Coincident(g16,g-1)
    c: PointOnObject(g16,g-2)
    c: Horizontal(g17)
    c: Symmetric(g17,g17,g16)
    c: Symmetric(g7,g7,g17)
    c: Symmetric(g1,g1,g17)
    c: Equal(g3,g5)
    c: Equal(g4,g0)
    c: DistanceX(g7,g5) = 5
    c: DistanceY(g6,g4) = 10
    c: DistanceX(g1,g7) = 68
    c: DistanceY(g16,g-1) = 32
FEATURE [PartDesign::Pocket] Pocket021  label="BMPR_GroveCableHoles"
  BaseFeature = -> Pocket020
  Length = 5
  Length2 = 100
  Profile = -> Sketch037
  Type = 1
FEATURE [PartDesign::Plane] DatumPlane002  label="Datum_PlateBot"
  AttachmentOffset = pos=(0,0,-3) rot=(0,0,1;0rad)
  Length = 187.465
  MapMode = 5
  Placement = pos=(0,0,-3) rot=(0,0,1;0rad)
  ResizeMode = 0
  Support = -> [XY_Plane001]
  Width = 202.462
  expr: .AttachmentOffset.Base.z = -<<params>>.plate_thick
FEATURE [PartDesign::Plane] DatumPlane003  label="Datum_RibBot"
  AttachmentOffset = pos=(0,0,-6) rot=(0,0,1;0rad)
  Length = 187.465
  MapMode = 5
  Placement = pos=(0,0,-6) rot=(0,0,1;0rad)
  ResizeMode = 0
  Support = -> [XY_Plane001]
  Width = 202.462
  expr: .AttachmentOffset.Base.z = -(<<params>>.plate_thick + <<params>>.rib_thick)
FEATURE [Sketcher::SketchObject] Sketch038  label="Sketch_RibSubLoftTop"
  FullyConstrained = true
  MapMode = 5
  Placement = pos=(0,0,-3) rot=(0,0,1;0rad)
  Support = -> [DatumPlane002]
  expr: Constraints[138] = <<params>>.rib_width_max
  expr: Constraints[74] = <<params>>.front_diameter
  expr: Constraints[69] = <<params>>.back_vert_edge
  expr: Constraints[71] = <<params>>.plate_width
  expr: Constraints[31] = <<params>>.wheel_well_plate_width
  expr: Constraints[37] = <<params>>.tail_width
  expr: Constraints[35] = <<params>>.plate_length
  expr: Constraints[73] = <<params>>.std_rad
  expr: Constraints[57] = <<params>>.std_rad
  expr: Constraints[72] = <<params>>.std_rad
  expr: Constraints[68] = <<params>>.front_vert_edge
  expr: Constraints[70] = <<params>>.wheel_well_clearance
  expr: Constraints[55] = <<params>>.std_rad
  expr: Constraints[36] = <<params>>.tail_rad
  sketch-geometry (55):
    g0: LineSegment StartX=-57.5 StartY=17 StartZ=0 EndX=-57.5 EndY=-17 EndZ=0
    g1: LineSegment StartX=57.5 StartY=17 StartZ=0 EndX=57.5 EndY=-17 EndZ=0
    g2: LineSegment StartX=-57.5 StartY=0 StartZ=0 EndX=57.5 EndY=0 EndZ=0
    g3: LineSegment StartX=-64.5 StartY=-24 StartZ=0 EndX=-75.5 EndY=-24 EndZ=0
    g4: LineSegment StartX=64.5 StartY=-24 StartZ=0 EndX=75.5 EndY=-24 EndZ=0
    g5: ArcOfCircle CenterX=0 CenterY=52.6846 CenterZ=0 NormalX=0 NormalY=0 NormalZ=1 AngleXU=0 Radius=112.5 StartAngle=3.96017 EndAngle=5.4646
    g6: LineSegment StartX=-64.5 StartY=24 StartZ=0 EndX=-75.5 EndY=24 EndZ=0
    g7: LineSegment StartX=64.5 StartY=24 StartZ=0 EndX=75.5 EndY=24 EndZ=0
    g8: LineSegment StartX=-77.1162 StartY=42.1781 StartZ=0 EndX=-29.0404 EndY=108.13 EndZ=0
    g9: LineSegment StartX=-25 StartY=110.185 StartZ=0 EndX=25 EndY=110.185 EndZ=0
    g10: LineSegment StartX=29.0404 StartY=108.13 StartZ=0 EndX=77.1162 EndY=42.1781 EndZ=0
    g11: LineSegment StartX=0 StartY=0 StartZ=0 EndX=0 EndY=110.185 EndZ=0
    g12: ArcOfCircle CenterX=-25 CenterY=105.185 CenterZ=0 NormalX=0 NormalY=0 NormalZ=1 AngleXU=0 Radius=5 StartAngle=1.5708 EndAngle=2.5117
    g13: ArcOfCircle CenterX=25 CenterY=105.185 CenterZ=0 NormalX=0 NormalY=0 NormalZ=1 AngleXU=0 Radius=5 StartAngle=0.629894 EndAngle=1.5708
    g14: ArcOfCircle CenterX=-64.5 CenterY=17 CenterZ=0 NormalX=0 NormalY=0 NormalZ=1 AngleXU=0 Radius=7 StartAngle=0 EndAngle=1.5708
    g15: ArcOfCircle CenterX=-64.5 CenterY=-17 CenterZ=0 NormalX=0 NormalY=0 NormalZ=1 AngleXU=0 Radius=7 StartAngle=4.71239 EndAngle=6.28319
    g16: ArcOfCircle CenterX=64.5 CenterY=-17 CenterZ=0 NormalX=0 NormalY=0 NormalZ=1 AngleXU=0 Radius=7 StartAngle=3.14159 EndAngle=4.71239
    g17: ArcOfCircle CenterX=64.5 CenterY=17 CenterZ=0 NormalX=0 NormalY=0 NormalZ=1 AngleXU=0 Radius=7 StartAngle=1.5708 EndAngle=3.14159
    g18: GeomPoint X=0 Y=-59.8154 Z=0
    g19: LineSegment StartX=77.5 StartY=26 StartZ=0 EndX=77.5 EndY=41 EndZ=0
    g20: LineSegment StartX=77.5 StartY=-26 StartZ=0 EndX=77.5 EndY=-28 EndZ=0
    g21: LineSegment StartX=-77.5 StartY=-28 StartZ=0 EndX=-77.5 EndY=-26 EndZ=0
    g22: LineSegment StartX=-77.5 StartY=26 StartZ=0 EndX=-77.5 EndY=41 EndZ=0
    g23: ArcOfCircle CenterX=75.5 CenterY=-28 CenterZ=0 NormalX=0 NormalY=0 NormalZ=1 AngleXU=0 Radius=2 StartAngle=5.4646 EndAngle=6.28319
    g24: ArcOfCircle CenterX=75.5 CenterY=-26 CenterZ=0 NormalX=0 NormalY=0 NormalZ=1 AngleXU=0 Radius=2 StartAngle=0 EndAngle=1.5708
    g25: ArcOfCircle CenterX=-75.5 CenterY=-28 CenterZ=0 NormalX=0 NormalY=0 NormalZ=1 AngleXU=0 Radius=2 StartAngle=3.14159 EndAngle=3.96017
    g26: ArcOfCircle CenterX=-75.5 CenterY=-26 CenterZ=0 NormalX=0 NormalY=0 NormalZ=1 AngleXU=0 Radius=2 StartAngle=1.5708 EndAngle=3.14159
    g27: ArcOfCircle CenterX=75.5 CenterY=26 CenterZ=0 NormalX=0 NormalY=0 NormalZ=1 AngleXU=0 Radius=2 StartAngle=4.71239 EndAngle=6.28319
    g28: ArcOfCircle CenterX=75.5 CenterY=41 CenterZ=0 NormalX=0 NormalY=0 NormalZ=1 AngleXU=0 Radius=2 StartAngle=1.3e-15 EndAngle=0.629894
    g29: ArcOfCircle CenterX=-75.5 CenterY=26 CenterZ=0 NormalX=0 NormalY=0 NormalZ=1 AngleXU=0 Radius=2 StartAngle=3.14159 EndAngle=4.71239
    g30: ArcOfCircle CenterX=-75.5 CenterY=41 CenterZ=0 NormalX=0 NormalY=0 NormalZ=1 AngleXU=0 Radius=2 StartAngle=2.5117 EndAngle=3.14159
    g31: LineSegment StartX=-77.5 StartY=110.185 StartZ=0 EndX=-2.5 EndY=110.185 EndZ=0
    g32: LineSegment StartX=-2.5 StartY=110.185 StartZ=0 EndX=-2.5 EndY=2.5 EndZ=0
    g33: LineSegment StartX=-2.5 StartY=2.5 StartZ=0 EndX=-77.5 EndY=2.5 EndZ=0
    g34: LineSegment StartX=-77.5 StartY=2.5 StartZ=0 EndX=-77.5 EndY=110.185 EndZ=0
    g35: LineSegment StartX=2.5 StartY=2.5 StartZ=0 EndX=77.5 EndY=2.5 EndZ=0
    g36: LineSegment StartX=77.5 StartY=2.5 StartZ=0 EndX=77.5 EndY=110.185 EndZ=0
    g37: LineSegment StartX=77.5 StartY=110.185 StartZ=0 EndX=2.5 EndY=110.185 EndZ=0
    g38: LineSegment StartX=2.5 StartY=110.185 StartZ=0 EndX=2.5 EndY=2.5 EndZ=0
    g39: LineSegment StartX=-77.5 StartY=-2.5 StartZ=0 EndX=-2.5 EndY=-2.5 EndZ=0
    g40: LineSegment StartX=-2.5 StartY=-2.5 StartZ=0 EndX=-2.5 EndY=-59.8154 EndZ=0
    g41: LineSegment StartX=-2.5 StartY=-59.8154 StartZ=0 EndX=-77.5 EndY=-59.8154 EndZ=0
    g42: LineSegment StartX=-77.5 StartY=-59.8154 StartZ=0 EndX=-77.5 EndY=-2.5 EndZ=0
    g43: LineSegment StartX=2.5 StartY=-2.5 StartZ=0 EndX=77.5 EndY=-2.5 EndZ=0
    g44: LineSegment StartX=77.5 StartY=-2.5 StartZ=0 EndX=77.5 EndY=-59.8154 EndZ=0
    g45: LineSegment StartX=77.5 StartY=-59.8154 StartZ=0 EndX=2.5 EndY=-59.8154 EndZ=0
    g46: LineSegment StartX=2.5 StartY=-59.8154 StartZ=0 EndX=2.5 EndY=-2.5 EndZ=0
    g47: LineSegment StartX=-2.5 StartY=110.185 StartZ=0 EndX=2.5 EndY=110.185 EndZ=0
    g48: LineSegment StartX=-2.5 StartY=2.5 StartZ=0 EndX=2.5 EndY=2.5 EndZ=0
    g49: LineSegment StartX=-2.5 StartY=-2.5 StartZ=0 EndX=2.5 EndY=-2.5 EndZ=0
    g50: LineSegment StartX=-77.5 StartY=-2.5 StartZ=0 EndX=-77.5 EndY=2.5 EndZ=0
    g51: LineSegment StartX=-2.5 StartY=-2.5 StartZ=0 EndX=-2.5 EndY=2.5 EndZ=0
    g52: LineSegment StartX=2.5 StartY=-2.5 StartZ=0 EndX=2.5 EndY=2.5 EndZ=0
    g53: LineSegment StartX=77.5 StartY=-2.5 StartZ=0 EndX=77.5 EndY=2.5 EndZ=0
    g54: LineSegment StartX=-2.5 StartY=-59.8154 StartZ=0 EndX=2.5 EndY=-59.8154 EndZ=0
  constraints (139):
    c: Vertical(g0)
    c: Vertical(g1)
    c: Horizontal(g2)
    c: Symmetric(g2,g2,g-1)
    c: Horizontal(g3)
    c: Horizontal(g4)
    c: PointOnObject(g5,g-2)
    c: Horizontal(g6)
    c: Horizontal(g7)
    c: Horizontal(g9)
    c: Coincident(g11,g-1)
    c: PointOnObject(g11,g-2)
    c: Tangent(g8,g12) = 1.5708
    c: Tangent(g9,g12) = 1.5708
    c: Tangent(g9,g13) = 1.5708
    c: Tangent(g10,g13) = 1.5708
    c: Tangent(g6,g14) = -1.5708
    c: Tangent(g0,g14) = 1.5708
    c: Tangent(g3,g15) = 1.5708
    c: Tangent(g0,g15) = 1.5708
    c: Tangent(g1,g16) = -1.5708
    c: Tangent(g4,g16) = -1.5708
    c: Tangent(g1,g17) = -1.5708
    c: Tangent(g7,g17) = 1.5708
    c: Equal(g13,g12)
    c: Symmetric(g9,g9,g11)
    c: Equal(g16,g17)
    c: Equal(g17,g14)
    c: Equal(g14,g15)
    c: PointOnObject(g18,g-2)
    c: PointOnObject(g18,g5)
    c: DistanceX(g2,g2) = 115
    c: Symmetric(g0,g0,g2)
    c: Symmetric(g1,g1,g2)
    c: Radius(g17) = 7
    c: DistanceY(g18,g9) = 170
    c: Radius(g13) = 5
    c: DistanceX(g9,g9) = 50
    c: Equal(g7,g6)
    c: Equal(g7,g4)
    c: Vertical(g19)
    c: Vertical(g20)
    c: Vertical(g21)
    c: Vertical(g22)
    c: Equal(g3,g6)
    c: Equal(g8,g10)
    c: Tangent(g5,g23) = -1.5708
    c: Tangent(g20,g23) = 1.5708
    c: Tangent(g20,g24) = 1.5708
    c: Tangent(g4,g24) = 1.5708
    c: Tangent(g5,g25) = -1.5708
    c: Tangent(g21,g25) = 1.5708
    c: Tangent(g21,g26) = 1.5708
    c: Tangent(g3,g26) = -1.5708
    c: Equal(g26,g24)
    c: Radius(g24) = 2
    c: Equal(g23,g25)
    c: Radius(g23) = 2
    c: Tangent(g7,g27) = -1.5708
    c: Tangent(g19,g27) = -1.5708
    c: Tangent(g19,g28) = -1.5708
    c: Tangent(g10,g28) = 1.5708
    c: Tangent(g6,g29) = 1.5708
    c: Tangent(g22,g29) = 1.5708
    c: Tangent(g8,g30) = 1.5708
    c: Tangent(g22,g30) = 1.5708
    c: Equal(g27,g29)
    c: Equal(g28,g30)
    c: DistanceY(g20,g20) = 2
    c: DistanceY(g19,g19) = 15
    c: DistanceY(g4,g7) = 48
    c: DistanceX(g21,g20) = 155
    c: Radius(g27) = 2
    c: Radius(g28) = 2
    c: Diameter(g5) = 225
    c: Equal(g21,g20)
    c: Coincident(g31,g32)
    c: Coincident(g32,g33)
    c: Coincident(g33,g34)
    c: Coincident(g34,g31)
    c: Horizontal(g31)
    c: Horizontal(g33)
    c: Vertical(g32)
    c: Vertical(g34)
    c: Coincident(g35,g36)
    c: Coincident(g36,g37)
    c: Coincident(g37,g38)
    c: Coincident(g38,g35)
    c: Horizontal(g35)
    c: Horizontal(g37)
    c: Vertical(g36)
    c: Vertical(g38)
    c: Coincident(g39,g40)
    c: Coincident(g40,g41)
    c: Coincident(g41,g42)
    c: Coincident(g42,g39)
    c: Horizontal(g39)
    c: Horizontal(g41)
    c: Vertical(g40)
    c: Vertical(g42)
    c: Coincident(g43,g44)
    c: Coincident(g44,g45)
    c: Coincident(g45,g46)
    c: Coincident(g46,g43)
    c: Horizontal(g43)
    c: Horizontal(g45)
    c: Vertical(g44)
    c: Vertical(g46)
    c: Coincident(g47,g31)
    c: Coincident(g47,g37)
    c: Coincident(g48,g32)
    c: Coincident(g48,g35)
    c: Horizontal(g48)
    c: Coincident(g49,g39)
    c: Coincident(g49,g43)
    c: Horizontal(g49)
    c: Coincident(g50,g39)
    c: Coincident(g50,g33)
    c: Coincident(g51,g39)
    c: Coincident(g51,g32)
    c: Coincident(g52,g43)
    c: Coincident(g52,g35)
    c: Coincident(g53,g43)
    c: Coincident(g53,g35)
    c: Coincident(g54,g40)
    c: Coincident(g54,g45)
    c: Horizontal(g47)
    c: Horizontal(g54)
    c: Vertical(g51)
    c: Vertical(g52)
    c: Vertical(g53)
    c: Vertical(g50)
    c: Symmetric(g39,g35,g-1)
    c: PointOnObject(g37,g9)
    c: PointOnObject(g19,g36)
    c: PointOnObject(g22,g34)
    c: PointOnObject(g18,g54)
    c: Equal(g52,g48)
    c: DistanceX(g39,g43) = 5
FEATURE [Sketcher::SketchObject] Sketch039  label="Sketch_RibSubLoftBot"
  FullyConstrained = true
  MapMode = 5
  Placement = pos=(0,0,-6) rot=(0,0,1;0rad)
  Support = -> [DatumPlane003]
  expr: Constraints[36] = <<params>>.tail_rad
  expr: Constraints[55] = <<params>>.std_rad
  expr: Constraints[70] = <<params>>.wheel_well_clearance
  expr: Constraints[68] = <<params>>.front_vert_edge
  expr: Constraints[72] = <<params>>.std_rad
  expr: Constraints[57] = <<params>>.std_rad
  expr: Constraints[73] = <<params>>.std_rad
  expr: Constraints[35] = <<params>>.plate_length
  expr: Constraints[37] = <<params>>.tail_width
  expr: Constraints[31] = <<params>>.wheel_well_plate_width
  expr: Constraints[71] = <<params>>.plate_width
  expr: Constraints[69] = <<params>>.back_vert_edge
  expr: Constraints[74] = <<params>>.front_diameter
  expr: Constraints[138] = Spreadsheet.rib_width_min
  sketch-geometry (55):
    g0: LineSegment StartX=-57.5 StartY=17 StartZ=0 EndX=-57.5 EndY=-17 EndZ=0
    g1: LineSegment StartX=57.5 StartY=17 StartZ=0 EndX=57.5 EndY=-17 EndZ=0
    g2: LineSegment StartX=-57.5 StartY=0 StartZ=0 EndX=57.5 EndY=0 EndZ=0
    g3: LineSegment StartX=-64.5 StartY=-24 StartZ=0 EndX=-75.5 EndY=-24 EndZ=0
    g4: LineSegment StartX=64.5 StartY=-24 StartZ=0 EndX=75.5 EndY=-24 EndZ=0
    g5: ArcOfCircle CenterX=0 CenterY=52.6846 CenterZ=0 NormalX=0 NormalY=0 NormalZ=1 AngleXU=0 Radius=112.5 StartAngle=3.96017 EndAngle=5.4646
    g6: LineSegment StartX=-64.5 StartY=24 StartZ=0 EndX=-75.5 EndY=24 EndZ=0
    g7: LineSegment StartX=64.5 StartY=24 StartZ=0 EndX=75.5 EndY=24 EndZ=0
    g8: LineSegment StartX=-77.1162 StartY=42.1781 StartZ=0 EndX=-29.0404 EndY=108.13 EndZ=0
    g9: LineSegment StartX=-25 StartY=110.185 StartZ=0 EndX=25 EndY=110.185 EndZ=0
    g10: LineSegment StartX=29.0404 StartY=108.13 StartZ=0 EndX=77.1162 EndY=42.1781 EndZ=0
    g11: LineSegment StartX=0 StartY=0 StartZ=0 EndX=0 EndY=110.185 EndZ=0
    g12: ArcOfCircle CenterX=-25 CenterY=105.185 CenterZ=0 NormalX=0 NormalY=0 NormalZ=1 AngleXU=0 Radius=5 StartAngle=1.5708 EndAngle=2.5117
    g13: ArcOfCircle CenterX=25 CenterY=105.185 CenterZ=0 NormalX=0 NormalY=0 NormalZ=1 AngleXU=0 Radius=5 StartAngle=0.629894 EndAngle=1.5708
    g14: ArcOfCircle CenterX=-64.5 CenterY=17 CenterZ=0 NormalX=0 NormalY=0 NormalZ=1 AngleXU=0 Radius=7 StartAngle=0 EndAngle=1.5708
    g15: ArcOfCircle CenterX=-64.5 CenterY=-17 CenterZ=0 NormalX=0 NormalY=0 NormalZ=1 AngleXU=0 Radius=7 StartAngle=4.71239 EndAngle=6.28319
    g16: ArcOfCircle CenterX=64.5 CenterY=-17 CenterZ=0 NormalX=0 NormalY=0 NormalZ=1 AngleXU=0 Radius=7 StartAngle=3.14159 EndAngle=4.71239
    g17: ArcOfCircle CenterX=64.5 CenterY=17 CenterZ=0 NormalX=0 NormalY=0 NormalZ=1 AngleXU=0 Radius=7 StartAngle=1.5708 EndAngle=3.14159
    g18: GeomPoint X=0 Y=-59.8154 Z=0
    g19: LineSegment StartX=77.5 StartY=26 StartZ=0 EndX=77.5 EndY=41 EndZ=0
    g20: LineSegment StartX=77.5 StartY=-26 StartZ=0 EndX=77.5 EndY=-28 EndZ=0
    g21: LineSegment StartX=-77.5 StartY=-28 StartZ=0 EndX=-77.5 EndY=-26 EndZ=0
    g22: LineSegment StartX=-77.5 StartY=26 StartZ=0 EndX=-77.5 EndY=41 EndZ=0
    g23: ArcOfCircle CenterX=75.5 CenterY=-28 CenterZ=0 NormalX=0 NormalY=0 NormalZ=1 AngleXU=0 Radius=2 StartAngle=5.4646 EndAngle=6.28319
    g24: ArcOfCircle CenterX=75.5 CenterY=-26 CenterZ=0 NormalX=0 NormalY=0 NormalZ=1 AngleXU=0 Radius=2 StartAngle=0 EndAngle=1.5708
    g25: ArcOfCircle CenterX=-75.5 CenterY=-28 CenterZ=0 NormalX=0 NormalY=0 NormalZ=1 AngleXU=0 Radius=2 StartAngle=3.14159 EndAngle=3.96017
    g26: ArcOfCircle CenterX=-75.5 CenterY=-26 CenterZ=0 NormalX=0 NormalY=0 NormalZ=1 AngleXU=0 Radius=2 StartAngle=1.5708 EndAngle=3.14159
    g27: ArcOfCircle CenterX=75.5 CenterY=26 CenterZ=0 NormalX=0 NormalY=0 NormalZ=1 AngleXU=0 Radius=2 StartAngle=4.71239 EndAngle=6.28319
    g28: ArcOfCircle CenterX=75.5 CenterY=41 CenterZ=0 NormalX=0 NormalY=0 NormalZ=1 AngleXU=0 Radius=2 StartAngle=1.3e-15 EndAngle=0.629894
    g29: ArcOfCircle CenterX=-75.5 CenterY=26 CenterZ=0 NormalX=0 NormalY=0 NormalZ=1 AngleXU=0 Radius=2 StartAngle=3.14159 EndAngle=4.71239
    g30: ArcOfCircle CenterX=-75.5 CenterY=41 CenterZ=0 NormalX=0 NormalY=0 NormalZ=1 AngleXU=0 Radius=2 StartAngle=2.5117 EndAngle=3.14159
    g31: LineSegment StartX=-77.5 StartY=110.185 StartZ=0 EndX=-1.5 EndY=110.185 EndZ=0
    g32: LineSegment StartX=-1.5 StartY=110.185 StartZ=0 EndX=-1.5 EndY=1.5 EndZ=0
    g33: LineSegment StartX=-1.5 StartY=1.5 StartZ=0 EndX=-77.5 EndY=1.5 EndZ=0
    g34: LineSegment StartX=-77.5 StartY=1.5 StartZ=0 EndX=-77.5 EndY=110.185 EndZ=0
    g35: LineSegment StartX=1.5 StartY=1.5 StartZ=0 EndX=77.5 EndY=1.5 EndZ=0
    g36: LineSegment StartX=77.5 StartY=1.5 StartZ=0 EndX=77.5 EndY=110.185 EndZ=0
    g37: LineSegment StartX=77.5 StartY=110.185 StartZ=0 EndX=1.5 EndY=110.185 EndZ=0
    g38: LineSegment StartX=1.5 StartY=110.185 StartZ=0 EndX=1.5 EndY=1.5 EndZ=0
    g39: LineSegment StartX=-77.5 StartY=-1.5 StartZ=0 EndX=-1.5 EndY=-1.5 EndZ=0
    g40: LineSegment StartX=-1.5 StartY=-1.5 StartZ=0 EndX=-1.5 EndY=-59.8154 EndZ=0
    g41: LineSegment StartX=-1.5 StartY=-59.8154 StartZ=0 EndX=-77.5 EndY=-59.8154 EndZ=0
    g42: LineSegment StartX=-77.5 StartY=-59.8154 StartZ=0 EndX=-77.5 EndY=-1.5 EndZ=0
    g43: LineSegment StartX=1.5 StartY=-1.5 StartZ=0 EndX=77.5 EndY=-1.5 EndZ=0
    g44: LineSegment StartX=77.5 StartY=-1.5 StartZ=0 EndX=77.5 EndY=-59.8154 EndZ=0
    g45: LineSegment StartX=77.5 StartY=-59.8154 StartZ=0 EndX=1.5 EndY=-59.8154 EndZ=0
    g46: LineSegment StartX=1.5 StartY=-59.8154 StartZ=0 EndX=1.5 EndY=-1.5 EndZ=0
    g47: LineSegment StartX=-1.5 StartY=110.185 StartZ=0 EndX=1.5 EndY=110.185 EndZ=0
    g48: LineSegment StartX=-1.5 StartY=1.5 StartZ=0 EndX=1.5 EndY=1.5 EndZ=0
    g49: LineSegment StartX=-1.5 StartY=-1.5 StartZ=0 EndX=1.5 EndY=-1.5 EndZ=0
    g50: LineSegment StartX=-77.5 StartY=-1.5 StartZ=0 EndX=-77.5 EndY=1.5 EndZ=0
    g51: LineSegment StartX=-1.5 StartY=-1.5 StartZ=0 EndX=-1.5 EndY=1.5 EndZ=0
    g52: LineSegment StartX=1.5 StartY=-1.5 StartZ=0 EndX=1.5 EndY=1.5 EndZ=0
    g53: LineSegment StartX=77.5 StartY=-1.5 StartZ=0 EndX=77.5 EndY=1.5 EndZ=0
    g54: LineSegment StartX=-1.5 StartY=-59.8154 StartZ=0 EndX=1.5 EndY=-59.8154 EndZ=0
  constraints (139):
    c: Vertical(g0)
    c: Vertical(g1)
    c: Horizontal(g2)
    c: Symmetric(g2,g2,g-1)
    c: Horizontal(g3)
    c: Horizontal(g4)
    c: PointOnObject(g5,g-2)
    c: Horizontal(g6)
    c: Horizontal(g7)
    c: Horizontal(g9)
    c: Coincident(g11,g-1)
    c: PointOnObject(g11,g-2)
    c: Tangent(g8,g12) = 1.5708
    c: Tangent(g9,g12) = 1.5708
    c: Tangent(g9,g13) = 1.5708
    c: Tangent(g10,g13) = 1.5708
    c: Tangent(g6,g14) = -1.5708
    c: Tangent(g0,g14) = 1.5708
    c: Tangent(g3,g15) = 1.5708
    c: Tangent(g0,g15) = 1.5708
    c: Tangent(g1,g16) = -1.5708
    c: Tangent(g4,g16) = -1.5708
    c: Tangent(g1,g17) = -1.5708
    c: Tangent(g7,g17) = 1.5708
    c: Equal(g13,g12)
    c: Symmetric(g9,g9,g11)
    c: Equal(g16,g17)
    c: Equal(g17,g14)
    c: Equal(g14,g15)
    c: PointOnObject(g18,g-2)
    c: PointOnObject(g18,g5)
    c: DistanceX(g2,g2) = 115
    c: Symmetric(g0,g0,g2)
    c: Symmetric(g1,g1,g2)
    c: Radius(g17) = 7
    c: DistanceY(g18,g9) = 170
    c: Radius(g13) = 5
    c: DistanceX(g9,g9) = 50
    c: Equal(g7,g6)
    c: Equal(g7,g4)
    c: Vertical(g19)
    c: Vertical(g20)
    c: Vertical(g21)
    c: Vertical(g22)
    c: Equal(g3,g6)
    c: Equal(g8,g10)
    c: Tangent(g5,g23) = -1.5708
    c: Tangent(g20,g23) = 1.5708
    c: Tangent(g20,g24) = 1.5708
    c: Tangent(g4,g24) = 1.5708
    c: Tangent(g5,g25) = -1.5708
    c: Tangent(g21,g25) = 1.5708
    c: Tangent(g21,g26) = 1.5708
    c: Tangent(g3,g26) = -1.5708
    c: Equal(g26,g24)
    c: Radius(g24) = 2
    c: Equal(g23,g25)
    c: Radius(g23) = 2
    c: Tangent(g7,g27) = -1.5708
    c: Tangent(g19,g27) = -1.5708
    c: Tangent(g19,g28) = -1.5708
    c: Tangent(g10,g28) = 1.5708
    c: Tangent(g6,g29) = 1.5708
    c: Tangent(g22,g29) = 1.5708
    c: Tangent(g8,g30) = 1.5708
    c: Tangent(g22,g30) = 1.5708
    c: Equal(g27,g29)
    c: Equal(g28,g30)
    c: DistanceY(g20,g20) = 2
    c: DistanceY(g19,g19) = 15
    c: DistanceY(g4,g7) = 48
    c: DistanceX(g21,g20) = 155
    c: Radius(g27) = 2
    c: Radius(g28) = 2
    c: Diameter(g5) = 225
    c: Equal(g21,g20)
    c: Coincident(g31,g32)
    c: Coincident(g32,g33)
    c: Coincident(g33,g34)
    c: Coincident(g34,g31)
    c: Horizontal(g31)
    c: Horizontal(g33)
    c: Vertical(g32)
    c: Vertical(g34)
    c: Coincident(g35,g36)
    c: Coincident(g36,g37)
    c: Coincident(g37,g38)
    c: Coincident(g38,g35)
    c: Horizontal(g35)
    c: Horizontal(g37)
    c: Vertical(g36)
    c: Vertical(g38)
    c: Coincident(g39,g40)
    c: Coincident(g40,g41)
    c: Coincident(g41,g42)
    c: Coincident(g42,g39)
    c: Horizontal(g39)
    c: Horizontal(g41)
    c: Vertical(g40)
    c: Vertical(g42)
    c: Coincident(g43,g44)
    c: Coincident(g44,g45)
    c: Coincident(g45,g46)
    c: Coincident(g46,g43)
    c: Horizontal(g43)
    c: Horizontal(g45)
    c: Vertical(g44)
    c: Vertical(g46)
    c: Coincident(g47,g31)
    c: Coincident(g47,g37)
    c: Coincident(g48,g32)
    c: Coincident(g48,g35)
    c: Horizontal(g48)
    c: Coincident(g49,g39)
    c: Coincident(g49,g43)
    c: Horizontal(g49)
    c: Coincident(g50,g39)
    c: Coincident(g50,g33)
    c: Coincident(g51,g39)
    c: Coincident(g51,g32)
    c: Coincident(g52,g43)
    c: Coincident(g52,g35)
    c: Coincident(g53,g43)
    c: Coincident(g53,g35)
    c: Coincident(g54,g40)
    c: Coincident(g54,g45)
    c: Horizontal(g47)
    c: Horizontal(g54)
    c: Vertical(g51)
    c: Vertical(g52)
    c: Vertical(g53)
    c: Vertical(g50)
    c: Symmetric(g39,g35,g-1)
    c: PointOnObject(g37,g9)
    c: PointOnObject(g19,g36)
    c: PointOnObject(g22,g34)
    c: PointOnObject(g18,g54)
    c: Equal(g52,g48)
    c: DistanceX(g39,g43) = 3
FEATURE [PartDesign::SubtractiveLoft] SubtractiveLoft  label="SubLoft_Ribs_Front1"
  BaseFeature = -> Pocket021
  Closed = false
  Profile = -> Sketch038
  Ruled = false
  Sections = -> [Sketch039]
FEATURE [Sketcher::SketchObject] Sketch040  label="Sketch_RibSubLoftTop001"
  FullyConstrained = true
  MapMode = 5
  Placement = pos=(0,0,-3) rot=(0,0,1;0rad)
  Support = -> [DatumPlane002]
  expr: Constraints[36] = <<params>>.tail_rad
  expr: Constraints[55] = <<params>>.std_rad
  expr: Constraints[70] = <<params>>.wheel_well_clearance
  expr: Constraints[68] = <<params>>.front_vert_edge
  expr: Constraints[72] = <<params>>.std_rad
  expr: Constraints[57] = <<params>>.std_rad
  expr: Constraints[73] = <<params>>.std_rad
  expr: Constraints[35] = <<params>>.plate_length
  expr: Constraints[37] = <<params>>.tail_width
  expr: Constraints[31] = <<params>>.wheel_well_plate_width
  expr: Constraints[71] = <<params>>.plate_width
  expr: Constraints[69] = <<params>>.back_vert_edge
  expr: Constraints[74] = <<params>>.front_diameter
  expr: Constraints[138] = <<params>>.rib_width_max
  sketch-geometry (55):
    g0: LineSegment StartX=-57.5 StartY=17 StartZ=0 EndX=-57.5 EndY=-17 EndZ=0
    g1: LineSegment StartX=57.5 StartY=17 StartZ=0 EndX=57.5 EndY=-17 EndZ=0
    g2: LineSegment StartX=-57.5 StartY=0 StartZ=0 EndX=57.5 EndY=0 EndZ=0
    g3: LineSegment StartX=-64.5 StartY=-24 StartZ=0 EndX=-75.5 EndY=-24 EndZ=0
    g4: LineSegment StartX=64.5 StartY=-24 StartZ=0 EndX=75.5 EndY=-24 EndZ=0
    g5: ArcOfCircle CenterX=0 CenterY=52.6846 CenterZ=0 NormalX=0 NormalY=0 NormalZ=1 AngleXU=0 Radius=112.5 StartAngle=3.96017 EndAngle=5.4646
    g6: LineSegment StartX=-64.5 StartY=24 StartZ=0 EndX=-75.5 EndY=24 EndZ=0
    g7: LineSegment StartX=64.5 StartY=24 StartZ=0 EndX=75.5 EndY=24 EndZ=0
    g8: LineSegment StartX=-77.1162 StartY=42.1781 StartZ=0 EndX=-29.0404 EndY=108.13 EndZ=0
    g9: LineSegment StartX=-25 StartY=110.185 StartZ=0 EndX=25 EndY=110.185 EndZ=0
    g10: LineSegment StartX=29.0404 StartY=108.13 StartZ=0 EndX=77.1162 EndY=42.1781 EndZ=0
    g11: LineSegment StartX=0 StartY=0 StartZ=0 EndX=0 EndY=110.185 EndZ=0
    g12: ArcOfCircle CenterX=-25 CenterY=105.185 CenterZ=0 NormalX=0 NormalY=0 NormalZ=1 AngleXU=0 Radius=5 StartAngle=1.5708 EndAngle=2.5117
    g13: ArcOfCircle CenterX=25 CenterY=105.185 CenterZ=0 NormalX=0 NormalY=0 NormalZ=1 AngleXU=0 Radius=5 StartAngle=0.629894 EndAngle=1.5708
    g14: ArcOfCircle CenterX=-64.5 CenterY=17 CenterZ=0 NormalX=0 NormalY=0 NormalZ=1 AngleXU=0 Radius=7 StartAngle=0 EndAngle=1.5708
    g15: ArcOfCircle CenterX=-64.5 CenterY=-17 CenterZ=0 NormalX=0 NormalY=0 NormalZ=1 AngleXU=0 Radius=7 StartAngle=4.71239 EndAngle=6.28319
    g16: ArcOfCircle CenterX=64.5 CenterY=-17 CenterZ=0 NormalX=0 NormalY=0 NormalZ=1 AngleXU=0 Radius=7 StartAngle=3.14159 EndAngle=4.71239
    g17: ArcOfCircle CenterX=64.5 CenterY=17 CenterZ=0 NormalX=0 NormalY=0 NormalZ=1 AngleXU=0 Radius=7 StartAngle=1.5708 EndAngle=3.14159
    g18: GeomPoint X=0 Y=-59.8154 Z=0
    g19: LineSegment StartX=77.5 StartY=26 StartZ=0 EndX=77.5 EndY=41 EndZ=0
    g20: LineSegment StartX=77.5 StartY=-26 StartZ=0 EndX=77.5 EndY=-28 EndZ=0
    g21: LineSegment StartX=-77.5 StartY=-28 StartZ=0 EndX=-77.5 EndY=-26 EndZ=0
    g22: LineSegment StartX=-77.5 StartY=26 StartZ=0 EndX=-77.5 EndY=41 EndZ=0
    g23: ArcOfCircle CenterX=75.5 CenterY=-28 CenterZ=0 NormalX=0 NormalY=0 NormalZ=1 AngleXU=0 Radius=2 StartAngle=5.4646 EndAngle=6.28319
    g24: ArcOfCircle CenterX=75.5 CenterY=-26 CenterZ=0 NormalX=0 NormalY=0 NormalZ=1 AngleXU=0 Radius=2 StartAngle=0 EndAngle=1.5708
    g25: ArcOfCircle CenterX=-75.5 CenterY=-28 CenterZ=0 NormalX=0 NormalY=0 NormalZ=1 AngleXU=0 Radius=2 StartAngle=3.14159 EndAngle=3.96017
    g26: ArcOfCircle CenterX=-75.5 CenterY=-26 CenterZ=0 NormalX=0 NormalY=0 NormalZ=1 AngleXU=0 Radius=2 StartAngle=1.5708 EndAngle=3.14159
    g27: ArcOfCircle CenterX=75.5 CenterY=26 CenterZ=0 NormalX=0 NormalY=0 NormalZ=1 AngleXU=0 Radius=2 StartAngle=4.71239 EndAngle=6.28319
    g28: ArcOfCircle CenterX=75.5 CenterY=41 CenterZ=0 NormalX=0 NormalY=0 NormalZ=1 AngleXU=0 Radius=2 StartAngle=1.3e-15 EndAngle=0.629894
    g29: ArcOfCircle CenterX=-75.5 CenterY=26 CenterZ=0 NormalX=0 NormalY=0 NormalZ=1 AngleXU=0 Radius=2 StartAngle=3.14159 EndAngle=4.71239
    g30: ArcOfCircle CenterX=-75.5 CenterY=41 CenterZ=0 NormalX=0 NormalY=0 NormalZ=1 AngleXU=0 Radius=2 StartAngle=2.5117 EndAngle=3.14159
    g31: LineSegment StartX=-77.5 StartY=110.185 StartZ=0 EndX=-2.5 EndY=110.185 EndZ=0
    g32: LineSegment StartX=-2.5 StartY=110.185 StartZ=0 EndX=-2.5 EndY=2.5 EndZ=0
    g33: LineSegment StartX=-2.5 StartY=2.5 StartZ=0 EndX=-77.5 EndY=2.5 EndZ=0
    g34: LineSegment StartX=-77.5 StartY=2.5 StartZ=0 EndX=-77.5 EndY=110.185 EndZ=0
    g35: LineSegment StartX=2.5 StartY=2.5 StartZ=0 EndX=77.5 EndY=2.5 EndZ=0
    g36: LineSegment StartX=77.5 StartY=2.5 StartZ=0 EndX=77.5 EndY=110.185 EndZ=0
    g37: LineSegment StartX=77.5 StartY=110.185 StartZ=0 EndX=2.5 EndY=110.185 EndZ=0
    g38: LineSegment StartX=2.5 StartY=110.185 StartZ=0 EndX=2.5 EndY=2.5 EndZ=0
    g39: LineSegment StartX=-77.5 StartY=-2.5 StartZ=0 EndX=-2.5 EndY=-2.5 EndZ=0
    g40: LineSegment StartX=-2.5 StartY=-2.5 StartZ=0 EndX=-2.5 EndY=-59.8154 EndZ=0
    g41: LineSegment StartX=-2.5 StartY=-59.8154 StartZ=0 EndX=-77.5 EndY=-59.8154 EndZ=0
    g42: LineSegment StartX=-77.5 StartY=-59.8154 StartZ=0 EndX=-77.5 EndY=-2.5 EndZ=0
    g43: LineSegment StartX=2.5 StartY=-2.5 StartZ=0 EndX=77.5 EndY=-2.5 EndZ=0
    g44: LineSegment StartX=77.5 StartY=-2.5 StartZ=0 EndX=77.5 EndY=-59.8154 EndZ=0
    g45: LineSegment StartX=77.5 StartY=-59.8154 StartZ=0 EndX=2.5 EndY=-59.8154 EndZ=0
    g46: LineSegment StartX=2.5 StartY=-59.8154 StartZ=0 EndX=2.5 EndY=-2.5 EndZ=0
    g47: LineSegment StartX=-2.5 StartY=110.185 StartZ=0 EndX=2.5 EndY=110.185 EndZ=0
    g48: LineSegment StartX=-2.5 StartY=2.5 StartZ=0 EndX=2.5 EndY=2.5 EndZ=0
    g49: LineSegment StartX=-2.5 StartY=-2.5 StartZ=0 EndX=2.5 EndY=-2.5 EndZ=0
    g50: LineSegment StartX=-77.5 StartY=-2.5 StartZ=0 EndX=-77.5 EndY=2.5 EndZ=0
    g51: LineSegment StartX=-2.5 StartY=-2.5 StartZ=0 EndX=-2.5 EndY=2.5 EndZ=0
    g52: LineSegment StartX=2.5 StartY=-2.5 StartZ=0 EndX=2.5 EndY=2.5 EndZ=0
    g53: LineSegment StartX=77.5 StartY=-2.5 StartZ=0 EndX=77.5 EndY=2.5 EndZ=0
    g54: LineSegment StartX=-2.5 StartY=-59.8154 StartZ=0 EndX=2.5 EndY=-59.8154 EndZ=0
  constraints (139):
    c: Vertical(g0)
    c: Vertical(g1)
    c: Horizontal(g2)
    c: Symmetric(g2,g2,g-1)
    c: Horizontal(g3)
    c: Horizontal(g4)
    c: PointOnObject(g5,g-2)
    c: Horizontal(g6)
    c: Horizontal(g7)
    c: Horizontal(g9)
    c: Coincident(g11,g-1)
    c: PointOnObject(g11,g-2)
    c: Tangent(g8,g12) = 1.5708
    c: Tangent(g9,g12) = 1.5708
    c: Tangent(g9,g13) = 1.5708
    c: Tangent(g10,g13) = 1.5708
    c: Tangent(g6,g14) = -1.5708
    c: Tangent(g0,g14) = 1.5708
    c: Tangent(g3,g15) = 1.5708
    c: Tangent(g0,g15) = 1.5708
    c: Tangent(g1,g16) = -1.5708
    c: Tangent(g4,g16) = -1.5708
    c: Tangent(g1,g17) = -1.5708
    c: Tangent(g7,g17) = 1.5708
    c: Equal(g13,g12)
    c: Symmetric(g9,g9,g11)
    c: Equal(g16,g17)
    c: Equal(g17,g14)
    c: Equal(g14,g15)
    c: PointOnObject(g18,g-2)
    c: PointOnObject(g18,g5)
    c: DistanceX(g2,g2) = 115
    c: Symmetric(g0,g0,g2)
    c: Symmetric(g1,g1,g2)
    c: Radius(g17) = 7
    c: DistanceY(g18,g9) = 170
    c: Radius(g13) = 5
    c: DistanceX(g9,g9) = 50
    c: Equal(g7,g6)
    c: Equal(g7,g4)
    c: Vertical(g19)
    c: Vertical(g20)
    c: Vertical(g21)
    c: Vertical(g22)
    c: Equal(g3,g6)
    c: Equal(g8,g10)
    c: Tangent(g5,g23) = -1.5708
    c: Tangent(g20,g23) = 1.5708
    c: Tangent(g20,g24) = 1.5708
    c: Tangent(g4,g24) = 1.5708
    c: Tangent(g5,g25) = -1.5708
    c: Tangent(g21,g25) = 1.5708
    c: Tangent(g21,g26) = 1.5708
    c: Tangent(g3,g26) = -1.5708
    c: Equal(g26,g24)
    c: Radius(g24) = 2
    c: Equal(g23,g25)
    c: Radius(g23) = 2
    c: Tangent(g7,g27) = -1.5708
    c: Tangent(g19,g27) = -1.5708
    c: Tangent(g19,g28) = -1.5708
    c: Tangent(g10,g28) = 1.5708
    c: Tangent(g6,g29) = 1.5708
    c: Tangent(g22,g29) = 1.5708
    c: Tangent(g8,g30) = 1.5708
    c: Tangent(g22,g30) = 1.5708
    c: Equal(g27,g29)
    c: Equal(g28,g30)
    c: DistanceY(g20,g20) = 2
    c: DistanceY(g19,g19) = 15
    c: DistanceY(g4,g7) = 48
    c: DistanceX(g21,g20) = 155
    c: Radius(g27) = 2
    c: Radius(g28) = 2
    c: Diameter(g5) = 225
    c: Equal(g21,g20)
    c: Coincident(g31,g32)
    c: Coincident(g32,g33)
    c: Coincident(g33,g34)
    c: Coincident(g34,g31)
    c: Horizontal(g31)
    c: Horizontal(g33)
    c: Vertical(g32)
    c: Vertical(g34)
    c: Coincident(g35,g36)
    c: Coincident(g36,g37)
    c: Coincident(g37,g38)
    c: Coincident(g38,g35)
    c: Horizontal(g35)
    c: Horizontal(g37)
    c: Vertical(g36)
    c: Vertical(g38)
    c: Coincident(g39,g40)
    c: Coincident(g40,g41)
    c: Coincident(g41,g42)
    c: Coincident(g42,g39)
    c: Horizontal(g39)
    c: Horizontal(g41)
    c: Vertical(g40)
    c: Vertical(g42)
    c: Coincident(g43,g44)
    c: Coincident(g44,g45)
    c: Coincident(g45,g46)
    c: Coincident(g46,g43)
    c: Horizontal(g43)
    c: Horizontal(g45)
    c: Vertical(g44)
    c: Vertical(g46)
    c: Coincident(g47,g31)
    c: Coincident(g47,g37)
    c: Coincident(g48,g32)
    c: Coincident(g48,g35)
    c: Horizontal(g48)
    c: Coincident(g49,g39)
    c: Coincident(g49,g43)
    c: Horizontal(g49)
    c: Coincident(g50,g39)
    c: Coincident(g50,g33)
    c: Coincident(g51,g39)
    c: Coincident(g51,g32)
    c: Coincident(g52,g43)
    c: Coincident(g52,g35)
    c: Coincident(g53,g43)
    c: Coincident(g53,g35)
    c: Coincident(g54,g40)
    c: Coincident(g54,g45)
    c: Horizontal(g47)
    c: Horizontal(g54)
    c: Vertical(g51)
    c: Vertical(g52)
    c: Vertical(g53)
    c: Vertical(g50)
    c: Symmetric(g39,g35,g-1)
    c: PointOnObject(g37,g9)
    c: PointOnObject(g19,g36)
    c: PointOnObject(g22,g34)
    c: PointOnObject(g18,g54)
    c: Equal(g52,g48)
    c: DistanceX(g39,g43) = 5
FEATURE [Sketcher::SketchObject] Sketch041  label="Sketch_RibSubLoftBot001"
  FullyConstrained = true
  MapMode = 5
  Placement = pos=(0,0,-6) rot=(0,0,1;0rad)
  Support = -> [DatumPlane003]
  expr: Constraints[138] = Spreadsheet.rib_width_min
  expr: Constraints[74] = <<params>>.front_diameter
  expr: Constraints[69] = <<params>>.back_vert_edge
  expr: Constraints[71] = <<params>>.plate_width
  expr: Constraints[31] = <<params>>.wheel_well_plate_width
  expr: Constraints[37] = <<params>>.tail_width
  expr: Constraints[35] = <<params>>.plate_length
  expr: Constraints[73] = <<params>>.std_rad
  expr: Constraints[57] = <<params>>.std_rad
  expr: Constraints[72] = <<params>>.std_rad
  expr: Constraints[68] = <<params>>.front_vert_edge
  expr: Constraints[70] = <<params>>.wheel_well_clearance
  expr: Constraints[55] = <<params>>.std_rad
  expr: Constraints[36] = <<params>>.tail_rad
  sketch-geometry (55):
    g0: LineSegment StartX=-57.5 StartY=17 StartZ=0 EndX=-57.5 EndY=-17 EndZ=0
    g1: LineSegment StartX=57.5 StartY=17 StartZ=0 EndX=57.5 EndY=-17 EndZ=0
    g2: LineSegment StartX=-57.5 StartY=0 StartZ=0 EndX=57.5 EndY=0 EndZ=0
    g3: LineSegment StartX=-64.5 StartY=-24 StartZ=0 EndX=-75.5 EndY=-24 EndZ=0
    g4: LineSegment StartX=64.5 StartY=-24 StartZ=0 EndX=75.5 EndY=-24 EndZ=0
    g5: ArcOfCircle CenterX=0 CenterY=52.6846 CenterZ=0 NormalX=0 NormalY=0 NormalZ=1 AngleXU=0 Radius=112.5 StartAngle=3.96017 EndAngle=5.4646
    g6: LineSegment StartX=-64.5 StartY=24 StartZ=0 EndX=-75.5 EndY=24 EndZ=0
    g7: LineSegment StartX=64.5 StartY=24 StartZ=0 EndX=75.5 EndY=24 EndZ=0
    g8: LineSegment StartX=-77.1162 StartY=42.1781 StartZ=0 EndX=-29.0404 EndY=108.13 EndZ=0
    g9: LineSegment StartX=-25 StartY=110.185 StartZ=0 EndX=25 EndY=110.185 EndZ=0
    g10: LineSegment StartX=29.0404 StartY=108.13 StartZ=0 EndX=77.1162 EndY=42.1781 EndZ=0
    g11: LineSegment StartX=0 StartY=0 StartZ=0 EndX=0 EndY=110.185 EndZ=0
    g12: ArcOfCircle CenterX=-25 CenterY=105.185 CenterZ=0 NormalX=0 NormalY=0 NormalZ=1 AngleXU=0 Radius=5 StartAngle=1.5708 EndAngle=2.5117
    g13: ArcOfCircle CenterX=25 CenterY=105.185 CenterZ=0 NormalX=0 NormalY=0 NormalZ=1 AngleXU=0 Radius=5 StartAngle=0.629894 EndAngle=1.5708
    g14: ArcOfCircle CenterX=-64.5 CenterY=17 CenterZ=0 NormalX=0 NormalY=0 NormalZ=1 AngleXU=0 Radius=7 StartAngle=0 EndAngle=1.5708
    g15: ArcOfCircle CenterX=-64.5 CenterY=-17 CenterZ=0 NormalX=0 NormalY=0 NormalZ=1 AngleXU=0 Radius=7 StartAngle=4.71239 EndAngle=6.28319
    g16: ArcOfCircle CenterX=64.5 CenterY=-17 CenterZ=0 NormalX=0 NormalY=0 NormalZ=1 AngleXU=0 Radius=7 StartAngle=3.14159 EndAngle=4.71239
    g17: ArcOfCircle CenterX=64.5 CenterY=17 CenterZ=0 NormalX=0 NormalY=0 NormalZ=1 AngleXU=0 Radius=7 StartAngle=1.5708 EndAngle=3.14159
    g18: GeomPoint X=0 Y=-59.8154 Z=0
    g19: LineSegment StartX=77.5 StartY=26 StartZ=0 EndX=77.5 EndY=41 EndZ=0
    g20: LineSegment StartX=77.5 StartY=-26 StartZ=0 EndX=77.5 EndY=-28 EndZ=0
    g21: LineSegment StartX=-77.5 StartY=-28 StartZ=0 EndX=-77.5 EndY=-26 EndZ=0
    g22: LineSegment StartX=-77.5 StartY=26 StartZ=0 EndX=-77.5 EndY=41 EndZ=0
    g23: ArcOfCircle CenterX=75.5 CenterY=-28 CenterZ=0 NormalX=0 NormalY=0 NormalZ=1 AngleXU=0 Radius=2 StartAngle=5.4646 EndAngle=6.28319
    g24: ArcOfCircle CenterX=75.5 CenterY=-26 CenterZ=0 NormalX=0 NormalY=0 NormalZ=1 AngleXU=0 Radius=2 StartAngle=0 EndAngle=1.5708
    g25: ArcOfCircle CenterX=-75.5 CenterY=-28 CenterZ=0 NormalX=0 NormalY=0 NormalZ=1 AngleXU=0 Radius=2 StartAngle=3.14159 EndAngle=3.96017
    g26: ArcOfCircle CenterX=-75.5 CenterY=-26 CenterZ=0 NormalX=0 NormalY=0 NormalZ=1 AngleXU=0 Radius=2 StartAngle=1.5708 EndAngle=3.14159
    g27: ArcOfCircle CenterX=75.5 CenterY=26 CenterZ=0 NormalX=0 NormalY=0 NormalZ=1 AngleXU=0 Radius=2 StartAngle=4.71239 EndAngle=6.28319
    g28: ArcOfCircle CenterX=75.5 CenterY=41 CenterZ=0 NormalX=0 NormalY=0 NormalZ=1 AngleXU=0 Radius=2 StartAngle=1.3e-15 EndAngle=0.629894
    g29: ArcOfCircle CenterX=-75.5 CenterY=26 CenterZ=0 NormalX=0 NormalY=0 NormalZ=1 AngleXU=0 Radius=2 StartAngle=3.14159 EndAngle=4.71239
    g30: ArcOfCircle CenterX=-75.5 CenterY=41 CenterZ=0 NormalX=0 NormalY=0 NormalZ=1 AngleXU=0 Radius=2 StartAngle=2.5117 EndAngle=3.14159
    g31: LineSegment StartX=-77.5 StartY=110.185 StartZ=0 EndX=-1.5 EndY=110.185 EndZ=0
    g32: LineSegment StartX=-1.5 StartY=110.185 StartZ=0 EndX=-1.5 EndY=1.5 EndZ=0
    g33: LineSegment StartX=-1.5 StartY=1.5 StartZ=0 EndX=-77.5 EndY=1.5 EndZ=0
    g34: LineSegment StartX=-77.5 StartY=1.5 StartZ=0 EndX=-77.5 EndY=110.185 EndZ=0
    g35: LineSegment StartX=1.5 StartY=1.5 StartZ=0 EndX=77.5 EndY=1.5 EndZ=0
    g36: LineSegment StartX=77.5 StartY=1.5 StartZ=0 EndX=77.5 EndY=110.185 EndZ=0
    g37: LineSegment StartX=77.5 StartY=110.185 StartZ=0 EndX=1.5 EndY=110.185 EndZ=0
    g38: LineSegment StartX=1.5 StartY=110.185 StartZ=0 EndX=1.5 EndY=1.5 EndZ=0
    g39: LineSegment StartX=-77.5 StartY=-1.5 StartZ=0 EndX=-1.5 EndY=-1.5 EndZ=0
    g40: LineSegment StartX=-1.5 StartY=-1.5 StartZ=0 EndX=-1.5 EndY=-59.8154 EndZ=0
    g41: LineSegment StartX=-1.5 StartY=-59.8154 StartZ=0 EndX=-77.5 EndY=-59.8154 EndZ=0
    g42: LineSegment StartX=-77.5 StartY=-59.8154 StartZ=0 EndX=-77.5 EndY=-1.5 EndZ=0
    g43: LineSegment StartX=1.5 StartY=-1.5 StartZ=0 EndX=77.5 EndY=-1.5 EndZ=0
    g44: LineSegment StartX=77.5 StartY=-1.5 StartZ=0 EndX=77.5 EndY=-59.8154 EndZ=0
    g45: LineSegment StartX=77.5 StartY=-59.8154 StartZ=0 EndX=1.5 EndY=-59.8154 EndZ=0
    g46: LineSegment StartX=1.5 StartY=-59.8154 StartZ=0 EndX=1.5 EndY=-1.5 EndZ=0
    g47: LineSegment StartX=-1.5 StartY=110.185 StartZ=0 EndX=1.5 EndY=110.185 EndZ=0
    g48: LineSegment StartX=-1.5 StartY=1.5 StartZ=0 EndX=1.5 EndY=1.5 EndZ=0
    g49: LineSegment StartX=-1.5 StartY=-1.5 StartZ=0 EndX=1.5 EndY=-1.5 EndZ=0
    g50: LineSegment StartX=-77.5 StartY=-1.5 StartZ=0 EndX=-77.5 EndY=1.5 EndZ=0
    g51: LineSegment StartX=-1.5 StartY=-1.5 StartZ=0 EndX=-1.5 EndY=1.5 EndZ=0
    g52: LineSegment StartX=1.5 StartY=-1.5 StartZ=0 EndX=1.5 EndY=1.5 EndZ=0
    g53: LineSegment StartX=77.5 StartY=-1.5 StartZ=0 EndX=77.5 EndY=1.5 EndZ=0
    g54: LineSegment StartX=-1.5 StartY=-59.8154 StartZ=0 EndX=1.5 EndY=-59.8154 EndZ=0
  constraints (139):
    c: Vertical(g0)
    c: Vertical(g1)
    c: Horizontal(g2)
    c: Symmetric(g2,g2,g-1)
    c: Horizontal(g3)
    c: Horizontal(g4)
    c: PointOnObject(g5,g-2)
    c: Horizontal(g6)
    c: Horizontal(g7)
    c: Horizontal(g9)
    c: Coincident(g11,g-1)
    c: PointOnObject(g11,g-2)
    c: Tangent(g8,g12) = 1.5708
    c: Tangent(g9,g12) = 1.5708
    c: Tangent(g9,g13) = 1.5708
    c: Tangent(g10,g13) = 1.5708
    c: Tangent(g6,g14) = -1.5708
    c: Tangent(g0,g14) = 1.5708
    c: Tangent(g3,g15) = 1.5708
    c: Tangent(g0,g15) = 1.5708
    c: Tangent(g1,g16) = -1.5708
    c: Tangent(g4,g16) = -1.5708
    c: Tangent(g1,g17) = -1.5708
    c: Tangent(g7,g17) = 1.5708
    c: Equal(g13,g12)
    c: Symmetric(g9,g9,g11)
    c: Equal(g16,g17)
    c: Equal(g17,g14)
    c: Equal(g14,g15)
    c: PointOnObject(g18,g-2)
    c: PointOnObject(g18,g5)
    c: DistanceX(g2,g2) = 115
    c: Symmetric(g0,g0,g2)
    c: Symmetric(g1,g1,g2)
    c: Radius(g17) = 7
    c: DistanceY(g18,g9) = 170
    c: Radius(g13) = 5
    c: DistanceX(g9,g9) = 50
    c: Equal(g7,g6)
    c: Equal(g7,g4)
    c: Vertical(g19)
    c: Vertical(g20)
    c: Vertical(g21)
    c: Vertical(g22)
    c: Equal(g3,g6)
    c: Equal(g8,g10)
    c: Tangent(g5,g23) = -1.5708
    c: Tangent(g20,g23) = 1.5708
    c: Tangent(g20,g24) = 1.5708
    c: Tangent(g4,g24) = 1.5708
    c: Tangent(g5,g25) = -1.5708
    c: Tangent(g21,g25) = 1.5708
    c: Tangent(g21,g26) = 1.5708
    c: Tangent(g3,g26) = -1.5708
    c: Equal(g26,g24)
    c: Radius(g24) = 2
    c: Equal(g23,g25)
    c: Radius(g23) = 2
    c: Tangent(g7,g27) = -1.5708
    c: Tangent(g19,g27) = -1.5708
    c: Tangent(g19,g28) = -1.5708
    c: Tangent(g10,g28) = 1.5708
    c: Tangent(g6,g29) = 1.5708
    c: Tangent(g22,g29) = 1.5708
    c: Tangent(g8,g30) = 1.5708
    c: Tangent(g22,g30) = 1.5708
    c: Equal(g27,g29)
    c: Equal(g28,g30)
    c: DistanceY(g20,g20) = 2
    c: DistanceY(g19,g19) = 15
    c: DistanceY(g4,g7) = 48
    c: DistanceX(g21,g20) = 155
    c: Radius(g27) = 2
    c: Radius(g28) = 2
    c: Diameter(g5) = 225
    c: Equal(g21,g20)
    c: Coincident(g31,g32)
    c: Coincident(g32,g33)
    c: Coincident(g33,g34)
    c: Coincident(g34,g31)
    c: Horizontal(g31)
    c: Horizontal(g33)
    c: Vertical(g32)
    c: Vertical(g34)
    c: Coincident(g35,g36)
    c: Coincident(g36,g37)
    c: Coincident(g37,g38)
    c: Coincident(g38,g35)
    c: Horizontal(g35)
    c: Horizontal(g37)
    c: Vertical(g36)
    c: Vertical(g38)
    c: Coincident(g39,g40)
    c: Coincident(g40,g41)
    c: Coincident(g41,g42)
    c: Coincident(g42,g39)
    c: Horizontal(g39)
    c: Horizontal(g41)
    c: Vertical(g40)
    c: Vertical(g42)
    c: Coincident(g43,g44)
    c: Coincident(g44,g45)
    c: Coincident(g45,g46)
    c: Coincident(g46,g43)
    c: Horizontal(g43)
    c: Horizontal(g45)
    c: Vertical(g44)
    c: Vertical(g46)
    c: Coincident(g47,g31)
    c: Coincident(g47,g37)
    c: Coincident(g48,g32)
    c: Coincident(g48,g35)
    c: Horizontal(g48)
    c: Coincident(g49,g39)
    c: Coincident(g49,g43)
    c: Horizontal(g49)
    c: Coincident(g50,g39)
    c: Coincident(g50,g33)
    c: Coincident(g51,g39)
    c: Coincident(g51,g32)
    c: Coincident(g52,g43)
    c: Coincident(g52,g35)
    c: Coincident(g53,g43)
    c: Coincident(g53,g35)
    c: Coincident(g54,g40)
    c: Coincident(g54,g45)
    c: Horizontal(g47)
    c: Horizontal(g54)
    c: Vertical(g51)
    c: Vertical(g52)
    c: Vertical(g53)
    c: Vertical(g50)
    c: Symmetric(g39,g35,g-1)
    c: PointOnObject(g37,g9)
    c: PointOnObject(g19,g36)
    c: PointOnObject(g22,g34)
    c: PointOnObject(g18,g54)
    c: Equal(g52,g48)
    c: DistanceX(g39,g43) = 3
FEATURE [PartDesign::SubtractiveLoft] SubtractiveLoft001  label="SubLoft_Ribs_Front2"
  BaseFeature = -> SubtractiveLoft
  Closed = false
  Profile = -> Sketch040
  Ruled = false
  Sections = -> [Sketch041]
FEATURE [Sketcher::SketchObject] Sketch042  label="Sketch_RibSubLoftTop002"
  FullyConstrained = true
  MapMode = 5
  Placement = pos=(0,0,-3) rot=(0,0,1;0rad)
  Support = -> [DatumPlane002]
  expr: Constraints[36] = <<params>>.tail_rad
  expr: Constraints[55] = <<params>>.std_rad
  expr: Constraints[70] = <<params>>.wheel_well_clearance
  expr: Constraints[68] = <<params>>.front_vert_edge
  expr: Constraints[72] = <<params>>.std_rad
  expr: Constraints[57] = <<params>>.std_rad
  expr: Constraints[73] = <<params>>.std_rad
  expr: Constraints[35] = <<params>>.plate_length
  expr: Constraints[37] = <<params>>.tail_width
  expr: Constraints[31] = <<params>>.wheel_well_plate_width
  expr: Constraints[71] = <<params>>.plate_width
  expr: Constraints[69] = <<params>>.back_vert_edge
  expr: Constraints[74] = <<params>>.front_diameter
  expr: Constraints[138] = <<params>>.rib_width_max
  sketch-geometry (55):
    g0: LineSegment StartX=-57.5 StartY=17 StartZ=0 EndX=-57.5 EndY=-17 EndZ=0
    g1: LineSegment StartX=57.5 StartY=17 StartZ=0 EndX=57.5 EndY=-17 EndZ=0
    g2: LineSegment StartX=-57.5 StartY=0 StartZ=0 EndX=57.5 EndY=0 EndZ=0
    g3: LineSegment StartX=-64.5 StartY=-24 StartZ=0 EndX=-75.5 EndY=-24 EndZ=0
    g4: LineSegment StartX=64.5 StartY=-24 StartZ=0 EndX=75.5 EndY=-24 EndZ=0
    g5: ArcOfCircle CenterX=0 CenterY=52.6846 CenterZ=0 NormalX=0 NormalY=0 NormalZ=1 AngleXU=0 Radius=112.5 StartAngle=3.96017 EndAngle=5.4646
    g6: LineSegment StartX=-64.5 StartY=24 StartZ=0 EndX=-75.5 EndY=24 EndZ=0
    g7: LineSegment StartX=64.5 StartY=24 StartZ=0 EndX=75.5 EndY=24 EndZ=0
    g8: LineSegment StartX=-77.1162 StartY=42.1781 StartZ=0 EndX=-29.0404 EndY=108.13 EndZ=0
    g9: LineSegment StartX=-25 StartY=110.185 StartZ=0 EndX=25 EndY=110.185 EndZ=0
    g10: LineSegment StartX=29.0404 StartY=108.13 StartZ=0 EndX=77.1162 EndY=42.1781 EndZ=0
    g11: LineSegment StartX=0 StartY=0 StartZ=0 EndX=0 EndY=110.185 EndZ=0
    g12: ArcOfCircle CenterX=-25 CenterY=105.185 CenterZ=0 NormalX=0 NormalY=0 NormalZ=1 AngleXU=0 Radius=5 StartAngle=1.5708 EndAngle=2.5117
    g13: ArcOfCircle CenterX=25 CenterY=105.185 CenterZ=0 NormalX=0 NormalY=0 NormalZ=1 AngleXU=0 Radius=5 StartAngle=0.629894 EndAngle=1.5708
    g14: ArcOfCircle CenterX=-64.5 CenterY=17 CenterZ=0 NormalX=0 NormalY=0 NormalZ=1 AngleXU=0 Radius=7 StartAngle=0 EndAngle=1.5708
    g15: ArcOfCircle CenterX=-64.5 CenterY=-17 CenterZ=0 NormalX=0 NormalY=0 NormalZ=1 AngleXU=0 Radius=7 StartAngle=4.71239 EndAngle=6.28319
    g16: ArcOfCircle CenterX=64.5 CenterY=-17 CenterZ=0 NormalX=0 NormalY=0 NormalZ=1 AngleXU=0 Radius=7 StartAngle=3.14159 EndAngle=4.71239
    g17: ArcOfCircle CenterX=64.5 CenterY=17 CenterZ=0 NormalX=0 NormalY=0 NormalZ=1 AngleXU=0 Radius=7 StartAngle=1.5708 EndAngle=3.14159
    g18: GeomPoint X=0 Y=-59.8154 Z=0
    g19: LineSegment StartX=77.5 StartY=26 StartZ=0 EndX=77.5 EndY=41 EndZ=0
    g20: LineSegment StartX=77.5 StartY=-26 StartZ=0 EndX=77.5 EndY=-28 EndZ=0
    g21: LineSegment StartX=-77.5 StartY=-28 StartZ=0 EndX=-77.5 EndY=-26 EndZ=0
    g22: LineSegment StartX=-77.5 StartY=26 StartZ=0 EndX=-77.5 EndY=41 EndZ=0
    g23: ArcOfCircle CenterX=75.5 CenterY=-28 CenterZ=0 NormalX=0 NormalY=0 NormalZ=1 AngleXU=0 Radius=2 StartAngle=5.4646 EndAngle=6.28319
    g24: ArcOfCircle CenterX=75.5 CenterY=-26 CenterZ=0 NormalX=0 NormalY=0 NormalZ=1 AngleXU=0 Radius=2 StartAngle=0 EndAngle=1.5708
    g25: ArcOfCircle CenterX=-75.5 CenterY=-28 CenterZ=0 NormalX=0 NormalY=0 NormalZ=1 AngleXU=0 Radius=2 StartAngle=3.14159 EndAngle=3.96017
    g26: ArcOfCircle CenterX=-75.5 CenterY=-26 CenterZ=0 NormalX=0 NormalY=0 NormalZ=1 AngleXU=0 Radius=2 StartAngle=1.5708 EndAngle=3.14159
    g27: ArcOfCircle CenterX=75.5 CenterY=26 CenterZ=0 NormalX=0 NormalY=0 NormalZ=1 AngleXU=0 Radius=2 StartAngle=4.71239 EndAngle=6.28319
    g28: ArcOfCircle CenterX=75.5 CenterY=41 CenterZ=0 NormalX=0 NormalY=0 NormalZ=1 AngleXU=0 Radius=2 StartAngle=1.3e-15 EndAngle=0.629894
    g29: ArcOfCircle CenterX=-75.5 CenterY=26 CenterZ=0 NormalX=0 NormalY=0 NormalZ=1 AngleXU=0 Radius=2 StartAngle=3.14159 EndAngle=4.71239
    g30: ArcOfCircle CenterX=-75.5 CenterY=41 CenterZ=0 NormalX=0 NormalY=0 NormalZ=1 AngleXU=0 Radius=2 StartAngle=2.5117 EndAngle=3.14159
    g31: LineSegment StartX=-77.5 StartY=110.185 StartZ=0 EndX=-2.5 EndY=110.185 EndZ=0
    g32: LineSegment StartX=-2.5 StartY=110.185 StartZ=0 EndX=-2.5 EndY=2.5 EndZ=0
    g33: LineSegment StartX=-2.5 StartY=2.5 StartZ=0 EndX=-77.5 EndY=2.5 EndZ=0
    g34: LineSegment StartX=-77.5 StartY=2.5 StartZ=0 EndX=-77.5 EndY=110.185 EndZ=0
    g35: LineSegment StartX=2.5 StartY=2.5 StartZ=0 EndX=77.5 EndY=2.5 EndZ=0
    g36: LineSegment StartX=77.5 StartY=2.5 StartZ=0 EndX=77.5 EndY=110.185 EndZ=0
    g37: LineSegment StartX=77.5 StartY=110.185 StartZ=0 EndX=2.5 EndY=110.185 EndZ=0
    g38: LineSegment StartX=2.5 StartY=110.185 StartZ=0 EndX=2.5 EndY=2.5 EndZ=0
    g39: LineSegment StartX=-77.5 StartY=-2.5 StartZ=0 EndX=-2.5 EndY=-2.5 EndZ=0
    g40: LineSegment StartX=-2.5 StartY=-2.5 StartZ=0 EndX=-2.5 EndY=-59.8154 EndZ=0
    g41: LineSegment StartX=-2.5 StartY=-59.8154 StartZ=0 EndX=-77.5 EndY=-59.8154 EndZ=0
    g42: LineSegment StartX=-77.5 StartY=-59.8154 StartZ=0 EndX=-77.5 EndY=-2.5 EndZ=0
    g43: LineSegment StartX=2.5 StartY=-2.5 StartZ=0 EndX=77.5 EndY=-2.5 EndZ=0
    g44: LineSegment StartX=77.5 StartY=-2.5 StartZ=0 EndX=77.5 EndY=-59.8154 EndZ=0
    g45: LineSegment StartX=77.5 StartY=-59.8154 StartZ=0 EndX=2.5 EndY=-59.8154 EndZ=0
    g46: LineSegment StartX=2.5 StartY=-59.8154 StartZ=0 EndX=2.5 EndY=-2.5 EndZ=0
    g47: LineSegment StartX=-2.5 StartY=110.185 StartZ=0 EndX=2.5 EndY=110.185 EndZ=0
    g48: LineSegment StartX=-2.5 StartY=2.5 StartZ=0 EndX=2.5 EndY=2.5 EndZ=0
    g49: LineSegment StartX=-2.5 StartY=-2.5 StartZ=0 EndX=2.5 EndY=-2.5 EndZ=0
    g50: LineSegment StartX=-77.5 StartY=-2.5 StartZ=0 EndX=-77.5 EndY=2.5 EndZ=0
    g51: LineSegment StartX=-2.5 StartY=-2.5 StartZ=0 EndX=-2.5 EndY=2.5 EndZ=0
    g52: LineSegment StartX=2.5 StartY=-2.5 StartZ=0 EndX=2.5 EndY=2.5 EndZ=0
    g53: LineSegment StartX=77.5 StartY=-2.5 StartZ=0 EndX=77.5 EndY=2.5 EndZ=0
    g54: LineSegment StartX=-2.5 StartY=-59.8154 StartZ=0 EndX=2.5 EndY=-59.8154 EndZ=0
  constraints (139):
    c: Vertical(g0)
    c: Vertical(g1)
    c: Horizontal(g2)
    c: Symmetric(g2,g2,g-1)
    c: Horizontal(g3)
    c: Horizontal(g4)
    c: PointOnObject(g5,g-2)
    c: Horizontal(g6)
    c: Horizontal(g7)
    c: Horizontal(g9)
    c: Coincident(g11,g-1)
    c: PointOnObject(g11,g-2)
    c: Tangent(g8,g12) = 1.5708
    c: Tangent(g9,g12) = 1.5708
    c: Tangent(g9,g13) = 1.5708
    c: Tangent(g10,g13) = 1.5708
    c: Tangent(g6,g14) = -1.5708
    c: Tangent(g0,g14) = 1.5708
    c: Tangent(g3,g15) = 1.5708
    c: Tangent(g0,g15) = 1.5708
    c: Tangent(g1,g16) = -1.5708
    c: Tangent(g4,g16) = -1.5708
    c: Tangent(g1,g17) = -1.5708
    c: Tangent(g7,g17) = 1.5708
    c: Equal(g13,g12)
    c: Symmetric(g9,g9,g11)
    c: Equal(g16,g17)
    c: Equal(g17,g14)
    c: Equal(g14,g15)
    c: PointOnObject(g18,g-2)
    c: PointOnObject(g18,g5)
    c: DistanceX(g2,g2) = 115
    c: Symmetric(g0,g0,g2)
    c: Symmetric(g1,g1,g2)
    c: Radius(g17) = 7
    c: DistanceY(g18,g9) = 170
    c: Radius(g13) = 5
    c: DistanceX(g9,g9) = 50
    c: Equal(g7,g6)
    c: Equal(g7,g4)
    c: Vertical(g19)
    c: Vertical(g20)
    c: Vertical(g21)
    c: Vertical(g22)
    c: Equal(g3,g6)
    c: Equal(g8,g10)
    c: Tangent(g5,g23) = -1.5708
    c: Tangent(g20,g23) = 1.5708
    c: Tangent(g20,g24) = 1.5708
    c: Tangent(g4,g24) = 1.5708
    c: Tangent(g5,g25) = -1.5708
    c: Tangent(g21,g25) = 1.5708
    c: Tangent(g21,g26) = 1.5708
    c: Tangent(g3,g26) = -1.5708
    c: Equal(g26,g24)
    c: Radius(g24) = 2
    c: Equal(g23,g25)
    c: Radius(g23) = 2
    c: Tangent(g7,g27) = -1.5708
    c: Tangent(g19,g27) = -1.5708
    c: Tangent(g19,g28) = -1.5708
    c: Tangent(g10,g28) = 1.5708
    c: Tangent(g6,g29) = 1.5708
    c: Tangent(g22,g29) = 1.5708
    c: Tangent(g8,g30) = 1.5708
    c: Tangent(g22,g30) = 1.5708
    c: Equal(g27,g29)
    c: Equal(g28,g30)
    c: DistanceY(g20,g20) = 2
    c: DistanceY(g19,g19) = 15
    c: DistanceY(g4,g7) = 48
    c: DistanceX(g21,g20) = 155
    c: Radius(g27) = 2
    c: Radius(g28) = 2
    c: Diameter(g5) = 225
    c: Equal(g21,g20)
    c: Coincident(g31,g32)
    c: Coincident(g32,g33)
    c: Coincident(g33,g34)
    c: Coincident(g34,g31)
    c: Horizontal(g31)
    c: Horizontal(g33)
    c: Vertical(g32)
    c: Vertical(g34)
    c: Coincident(g35,g36)
    c: Coincident(g36,g37)
    c: Coincident(g37,g38)
    c: Coincident(g38,g35)
    c: Horizontal(g35)
    c: Horizontal(g37)
    c: Vertical(g36)
    c: Vertical(g38)
    c: Coincident(g39,g40)
    c: Coincident(g40,g41)
    c: Coincident(g41,g42)
    c: Coincident(g42,g39)
    c: Horizontal(g39)
    c: Horizontal(g41)
    c: Vertical(g40)
    c: Vertical(g42)
    c: Coincident(g43,g44)
    c: Coincident(g44,g45)
    c: Coincident(g45,g46)
    c: Coincident(g46,g43)
    c: Horizontal(g43)
    c: Horizontal(g45)
    c: Vertical(g44)
    c: Vertical(g46)
    c: Coincident(g47,g31)
    c: Coincident(g47,g37)
    c: Coincident(g48,g32)
    c: Coincident(g48,g35)
    c: Horizontal(g48)
    c: Coincident(g49,g39)
    c: Coincident(g49,g43)
    c: Horizontal(g49)
    c: Coincident(g50,g39)
    c: Coincident(g50,g33)
    c: Coincident(g51,g39)
    c: Coincident(g51,g32)
    c: Coincident(g52,g43)
    c: Coincident(g52,g35)
    c: Coincident(g53,g43)
    c: Coincident(g53,g35)
    c: Coincident(g54,g40)
    c: Coincident(g54,g45)
    c: Horizontal(g47)
    c: Horizontal(g54)
    c: Vertical(g51)
    c: Vertical(g52)
    c: Vertical(g53)
    c: Vertical(g50)
    c: Symmetric(g39,g35,g-1)
    c: PointOnObject(g37,g9)
    c: PointOnObject(g19,g36)
    c: PointOnObject(g22,g34)
    c: PointOnObject(g18,g54)
    c: Equal(g52,g48)
    c: DistanceX(g39,g43) = 5
FEATURE [Sketcher::SketchObject] Sketch043  label="Sketch_RibSubLoftBot002"
  FullyConstrained = true
  MapMode = 5
  Placement = pos=(0,0,-6) rot=(0,0,1;0rad)
  Support = -> [DatumPlane003]
  expr: Constraints[138] = Spreadsheet.rib_width_min
  expr: Constraints[74] = <<params>>.front_diameter
  expr: Constraints[69] = <<params>>.back_vert_edge
  expr: Constraints[71] = <<params>>.plate_width
  expr: Constraints[31] = <<params>>.wheel_well_plate_width
  expr: Constraints[37] = <<params>>.tail_width
  expr: Constraints[35] = <<params>>.plate_length
  expr: Constraints[73] = <<params>>.std_rad
  expr: Constraints[57] = <<params>>.std_rad
  expr: Constraints[72] = <<params>>.std_rad
  expr: Constraints[68] = <<params>>.front_vert_edge
  expr: Constraints[70] = <<params>>.wheel_well_clearance
  expr: Constraints[55] = <<params>>.std_rad
  expr: Constraints[36] = <<params>>.tail_rad
  sketch-geometry (55):
    g0: LineSegment StartX=-57.5 StartY=17 StartZ=0 EndX=-57.5 EndY=-17 EndZ=0
    g1: LineSegment StartX=57.5 StartY=17 StartZ=0 EndX=57.5 EndY=-17 EndZ=0
    g2: LineSegment StartX=-57.5 StartY=0 StartZ=0 EndX=57.5 EndY=0 EndZ=0
    g3: LineSegment StartX=-64.5 StartY=-24 StartZ=0 EndX=-75.5 EndY=-24 EndZ=0
    g4: LineSegment StartX=64.5 StartY=-24 StartZ=0 EndX=75.5 EndY=-24 EndZ=0
    g5: ArcOfCircle CenterX=0 CenterY=52.6846 CenterZ=0 NormalX=0 NormalY=0 NormalZ=1 AngleXU=0 Radius=112.5 StartAngle=3.96017 EndAngle=5.4646
    g6: LineSegment StartX=-64.5 StartY=24 StartZ=0 EndX=-75.5 EndY=24 EndZ=0
    g7: LineSegment StartX=64.5 StartY=24 StartZ=0 EndX=75.5 EndY=24 EndZ=0
    g8: LineSegment StartX=-77.1162 StartY=42.1781 StartZ=0 EndX=-29.0404 EndY=108.13 EndZ=0
    g9: LineSegment StartX=-25 StartY=110.185 StartZ=0 EndX=25 EndY=110.185 EndZ=0
    g10: LineSegment StartX=29.0404 StartY=108.13 StartZ=0 EndX=77.1162 EndY=42.1781 EndZ=0
    g11: LineSegment StartX=0 StartY=0 StartZ=0 EndX=0 EndY=110.185 EndZ=0
    g12: ArcOfCircle CenterX=-25 CenterY=105.185 CenterZ=0 NormalX=0 NormalY=0 NormalZ=1 AngleXU=0 Radius=5 StartAngle=1.5708 EndAngle=2.5117
    g13: ArcOfCircle CenterX=25 CenterY=105.185 CenterZ=0 NormalX=0 NormalY=0 NormalZ=1 AngleXU=0 Radius=5 StartAngle=0.629894 EndAngle=1.5708
    g14: ArcOfCircle CenterX=-64.5 CenterY=17 CenterZ=0 NormalX=0 NormalY=0 NormalZ=1 AngleXU=0 Radius=7 StartAngle=0 EndAngle=1.5708
    g15: ArcOfCircle CenterX=-64.5 CenterY=-17 CenterZ=0 NormalX=0 NormalY=0 NormalZ=1 AngleXU=0 Radius=7 StartAngle=4.71239 EndAngle=6.28319
    g16: ArcOfCircle CenterX=64.5 CenterY=-17 CenterZ=0 NormalX=0 NormalY=0 NormalZ=1 AngleXU=0 Radius=7 StartAngle=3.14159 EndAngle=4.71239
    g17: ArcOfCircle CenterX=64.5 CenterY=17 CenterZ=0 NormalX=0 NormalY=0 NormalZ=1 AngleXU=0 Radius=7 StartAngle=1.5708 EndAngle=3.14159
    g18: GeomPoint X=0 Y=-59.8154 Z=0
    g19: LineSegment StartX=77.5 StartY=26 StartZ=0 EndX=77.5 EndY=41 EndZ=0
    g20: LineSegment StartX=77.5 StartY=-26 StartZ=0 EndX=77.5 EndY=-28 EndZ=0
    g21: LineSegment StartX=-77.5 StartY=-28 StartZ=0 EndX=-77.5 EndY=-26 EndZ=0
    g22: LineSegment StartX=-77.5 StartY=26 StartZ=0 EndX=-77.5 EndY=41 EndZ=0
    g23: ArcOfCircle CenterX=75.5 CenterY=-28 CenterZ=0 NormalX=0 NormalY=0 NormalZ=1 AngleXU=0 Radius=2 StartAngle=5.4646 EndAngle=6.28319
    g24: ArcOfCircle CenterX=75.5 CenterY=-26 CenterZ=0 NormalX=0 NormalY=0 NormalZ=1 AngleXU=0 Radius=2 StartAngle=0 EndAngle=1.5708
    g25: ArcOfCircle CenterX=-75.5 CenterY=-28 CenterZ=0 NormalX=0 NormalY=0 NormalZ=1 AngleXU=0 Radius=2 StartAngle=3.14159 EndAngle=3.96017
    g26: ArcOfCircle CenterX=-75.5 CenterY=-26 CenterZ=0 NormalX=0 NormalY=0 NormalZ=1 AngleXU=0 Radius=2 StartAngle=1.5708 EndAngle=3.14159
    g27: ArcOfCircle CenterX=75.5 CenterY=26 CenterZ=0 NormalX=0 NormalY=0 NormalZ=1 AngleXU=0 Radius=2 StartAngle=4.71239 EndAngle=6.28319
    g28: ArcOfCircle CenterX=75.5 CenterY=41 CenterZ=0 NormalX=0 NormalY=0 NormalZ=1 AngleXU=0 Radius=2 StartAngle=1.3e-15 EndAngle=0.629894
    g29: ArcOfCircle CenterX=-75.5 CenterY=26 CenterZ=0 NormalX=0 NormalY=0 NormalZ=1 AngleXU=0 Radius=2 StartAngle=3.14159 EndAngle=4.71239
    g30: ArcOfCircle CenterX=-75.5 CenterY=41 CenterZ=0 NormalX=0 NormalY=0 NormalZ=1 AngleXU=0 Radius=2 StartAngle=2.5117 EndAngle=3.14159
    g31: LineSegment StartX=-77.5 StartY=110.185 StartZ=0 EndX=-1.5 EndY=110.185 EndZ=0
    g32: LineSegment StartX=-1.5 StartY=110.185 StartZ=0 EndX=-1.5 EndY=1.5 EndZ=0
    g33: LineSegment StartX=-1.5 StartY=1.5 StartZ=0 EndX=-77.5 EndY=1.5 EndZ=0
    g34: LineSegment StartX=-77.5 StartY=1.5 StartZ=0 EndX=-77.5 EndY=110.185 EndZ=0
    g35: LineSegment StartX=1.5 StartY=1.5 StartZ=0 EndX=77.5 EndY=1.5 EndZ=0
    g36: LineSegment StartX=77.5 StartY=1.5 StartZ=0 EndX=77.5 EndY=110.185 EndZ=0
    g37: LineSegment StartX=77.5 StartY=110.185 StartZ=0 EndX=1.5 EndY=110.185 EndZ=0
    g38: LineSegment StartX=1.5 StartY=110.185 StartZ=0 EndX=1.5 EndY=1.5 EndZ=0
    g39: LineSegment StartX=-77.5 StartY=-1.5 StartZ=0 EndX=-1.5 EndY=-1.5 EndZ=0
    g40: LineSegment StartX=-1.5 StartY=-1.5 StartZ=0 EndX=-1.5 EndY=-59.8154 EndZ=0
    g41: LineSegment StartX=-1.5 StartY=-59.8154 StartZ=0 EndX=-77.5 EndY=-59.8154 EndZ=0
    g42: LineSegment StartX=-77.5 StartY=-59.8154 StartZ=0 EndX=-77.5 EndY=-1.5 EndZ=0
    g43: LineSegment StartX=1.5 StartY=-1.5 StartZ=0 EndX=77.5 EndY=-1.5 EndZ=0
    g44: LineSegment StartX=77.5 StartY=-1.5 StartZ=0 EndX=77.5 EndY=-59.8154 EndZ=0
    g45: LineSegment StartX=77.5 StartY=-59.8154 StartZ=0 EndX=1.5 EndY=-59.8154 EndZ=0
    g46: LineSegment StartX=1.5 StartY=-59.8154 StartZ=0 EndX=1.5 EndY=-1.5 EndZ=0
    g47: LineSegment StartX=-1.5 StartY=110.185 StartZ=0 EndX=1.5 EndY=110.185 EndZ=0
    g48: LineSegment StartX=-1.5 StartY=1.5 StartZ=0 EndX=1.5 EndY=1.5 EndZ=0
    g49: LineSegment StartX=-1.5 StartY=-1.5 StartZ=0 EndX=1.5 EndY=-1.5 EndZ=0
    g50: LineSegment StartX=-77.5 StartY=-1.5 StartZ=0 EndX=-77.5 EndY=1.5 EndZ=0
    g51: LineSegment StartX=-1.5 StartY=-1.5 StartZ=0 EndX=-1.5 EndY=1.5 EndZ=0
    g52: LineSegment StartX=1.5 StartY=-1.5 StartZ=0 EndX=1.5 EndY=1.5 EndZ=0
    g53: LineSegment StartX=77.5 StartY=-1.5 StartZ=0 EndX=77.5 EndY=1.5 EndZ=0
    g54: LineSegment StartX=-1.5 StartY=-59.8154 StartZ=0 EndX=1.5 EndY=-59.8154 EndZ=0
  constraints (139):
    c: Vertical(g0)
    c: Vertical(g1)
    c: Horizontal(g2)
    c: Symmetric(g2,g2,g-1)
    c: Horizontal(g3)
    c: Horizontal(g4)
    c: PointOnObject(g5,g-2)
    c: Horizontal(g6)
    c: Horizontal(g7)
    c: Horizontal(g9)
    c: Coincident(g11,g-1)
    c: PointOnObject(g11,g-2)
    c: Tangent(g8,g12) = 1.5708
    c: Tangent(g9,g12) = 1.5708
    c: Tangent(g9,g13) = 1.5708
    c: Tangent(g10,g13) = 1.5708
    c: Tangent(g6,g14) = -1.5708
    c: Tangent(g0,g14) = 1.5708
    c: Tangent(g3,g15) = 1.5708
    c: Tangent(g0,g15) = 1.5708
    c: Tangent(g1,g16) = -1.5708
    c: Tangent(g4,g16) = -1.5708
    c: Tangent(g1,g17) = -1.5708
    c: Tangent(g7,g17) = 1.5708
    c: Equal(g13,g12)
    c: Symmetric(g9,g9,g11)
    c: Equal(g16,g17)
    c: Equal(g17,g14)
    c: Equal(g14,g15)
    c: PointOnObject(g18,g-2)
    c: PointOnObject(g18,g5)
    c: DistanceX(g2,g2) = 115
    c: Symmetric(g0,g0,g2)
    c: Symmetric(g1,g1,g2)
    c: Radius(g17) = 7
    c: DistanceY(g18,g9) = 170
    c: Radius(g13) = 5
    c: DistanceX(g9,g9) = 50
    c: Equal(g7,g6)
    c: Equal(g7,g4)
    c: Vertical(g19)
    c: Vertical(g20)
    c: Vertical(g21)
    c: Vertical(g22)
    c: Equal(g3,g6)
    c: Equal(g8,g10)
    c: Tangent(g5,g23) = -1.5708
    c: Tangent(g20,g23) = 1.5708
    c: Tangent(g20,g24) = 1.5708
    c: Tangent(g4,g24) = 1.5708
    c: Tangent(g5,g25) = -1.5708
    c: Tangent(g21,g25) = 1.5708
    c: Tangent(g21,g26) = 1.5708
    c: Tangent(g3,g26) = -1.5708
    c: Equal(g26,g24)
    c: Radius(g24) = 2
    c: Equal(g23,g25)
    c: Radius(g23) = 2
    c: Tangent(g7,g27) = -1.5708
    c: Tangent(g19,g27) = -1.5708
    c: Tangent(g19,g28) = -1.5708
    c: Tangent(g10,g28) = 1.5708
    c: Tangent(g6,g29) = 1.5708
    c: Tangent(g22,g29) = 1.5708
    c: Tangent(g8,g30) = 1.5708
    c: Tangent(g22,g30) = 1.5708
    c: Equal(g27,g29)
    c: Equal(g28,g30)
    c: DistanceY(g20,g20) = 2
    c: DistanceY(g19,g19) = 15
    c: DistanceY(g4,g7) = 48
    c: DistanceX(g21,g20) = 155
    c: Radius(g27) = 2
    c: Radius(g28) = 2
    c: Diameter(g5) = 225
    c: Equal(g21,g20)
    c: Coincident(g31,g32)
    c: Coincident(g32,g33)
    c: Coincident(g33,g34)
    c: Coincident(g34,g31)
    c: Horizontal(g31)
    c: Horizontal(g33)
    c: Vertical(g32)
    c: Vertical(g34)
    c: Coincident(g35,g36)
    c: Coincident(g36,g37)
    c: Coincident(g37,g38)
    c: Coincident(g38,g35)
    c: Horizontal(g35)
    c: Horizontal(g37)
    c: Vertical(g36)
    c: Vertical(g38)
    c: Coincident(g39,g40)
    c: Coincident(g40,g41)
    c: Coincident(g41,g42)
    c: Coincident(g42,g39)
    c: Horizontal(g39)
    c: Horizontal(g41)
    c: Vertical(g40)
    c: Vertical(g42)
    c: Coincident(g43,g44)
    c: Coincident(g44,g45)
    c: Coincident(g45,g46)
    c: Coincident(g46,g43)
    c: Horizontal(g43)
    c: Horizontal(g45)
    c: Vertical(g44)
    c: Vertical(g46)
    c: Coincident(g47,g31)
    c: Coincident(g47,g37)
    c: Coincident(g48,g32)
    c: Coincident(g48,g35)
    c: Horizontal(g48)
    c: Coincident(g49,g39)
    c: Coincident(g49,g43)
    c: Horizontal(g49)
    c: Coincident(g50,g39)
    c: Coincident(g50,g33)
    c: Coincident(g51,g39)
    c: Coincident(g51,g32)
    c: Coincident(g52,g43)
    c: Coincident(g52,g35)
    c: Coincident(g53,g43)
    c: Coincident(g53,g35)
    c: Coincident(g54,g40)
    c: Coincident(g54,g45)
    c: Horizontal(g47)
    c: Horizontal(g54)
    c: Vertical(g51)
    c: Vertical(g52)
    c: Vertical(g53)
    c: Vertical(g50)
    c: Symmetric(g39,g35,g-1)
    c: PointOnObject(g37,g9)
    c: PointOnObject(g19,g36)
    c: PointOnObject(g22,g34)
    c: PointOnObject(g18,g54)
    c: Equal(g52,g48)
    c: DistanceX(g39,g43) = 3
FEATURE [PartDesign::SubtractiveLoft] SubtractiveLoft002  label="SubLoft_Ribs_Back1"
  BaseFeature = -> SubtractiveLoft001
  Closed = false
  Profile = -> Sketch042
  Ruled = false
  Sections = -> [Sketch043]
FEATURE [Sketcher::SketchObject] Sketch044  label="Sketch_RibSubLoftTop003"
  FullyConstrained = true
  MapMode = 5
  Placement = pos=(0,0,-3) rot=(0,0,1;0rad)
  Support = -> [DatumPlane002]
  expr: Constraints[36] = <<params>>.tail_rad
  expr: Constraints[55] = <<params>>.std_rad
  expr: Constraints[70] = <<params>>.wheel_well_clearance
  expr: Constraints[68] = <<params>>.front_vert_edge
  expr: Constraints[72] = <<params>>.std_rad
  expr: Constraints[57] = <<params>>.std_rad
  expr: Constraints[73] = <<params>>.std_rad
  expr: Constraints[35] = <<params>>.plate_length
  expr: Constraints[37] = <<params>>.tail_width
  expr: Constraints[31] = <<params>>.wheel_well_plate_width
  expr: Constraints[71] = <<params>>.plate_width
  expr: Constraints[69] = <<params>>.back_vert_edge
  expr: Constraints[74] = <<params>>.front_diameter
  expr: Constraints[138] = <<params>>.rib_width_max
  sketch-geometry (55):
    g0: LineSegment StartX=-57.5 StartY=17 StartZ=0 EndX=-57.5 EndY=-17 EndZ=0
    g1: LineSegment StartX=57.5 StartY=17 StartZ=0 EndX=57.5 EndY=-17 EndZ=0
    g2: LineSegment StartX=-57.5 StartY=0 StartZ=0 EndX=57.5 EndY=0 EndZ=0
    g3: LineSegment StartX=-64.5 StartY=-24 StartZ=0 EndX=-75.5 EndY=-24 EndZ=0
    g4: LineSegment StartX=64.5 StartY=-24 StartZ=0 EndX=75.5 EndY=-24 EndZ=0
    g5: ArcOfCircle CenterX=0 CenterY=52.6846 CenterZ=0 NormalX=0 NormalY=0 NormalZ=1 AngleXU=0 Radius=112.5 StartAngle=3.96017 EndAngle=5.4646
    g6: LineSegment StartX=-64.5 StartY=24 StartZ=0 EndX=-75.5 EndY=24 EndZ=0
    g7: LineSegment StartX=64.5 StartY=24 StartZ=0 EndX=75.5 EndY=24 EndZ=0
    g8: LineSegment StartX=-77.1162 StartY=42.1781 StartZ=0 EndX=-29.0404 EndY=108.13 EndZ=0
    g9: LineSegment StartX=-25 StartY=110.185 StartZ=0 EndX=25 EndY=110.185 EndZ=0
    g10: LineSegment StartX=29.0404 StartY=108.13 StartZ=0 EndX=77.1162 EndY=42.1781 EndZ=0
    g11: LineSegment StartX=0 StartY=0 StartZ=0 EndX=0 EndY=110.185 EndZ=0
    g12: ArcOfCircle CenterX=-25 CenterY=105.185 CenterZ=0 NormalX=0 NormalY=0 NormalZ=1 AngleXU=0 Radius=5 StartAngle=1.5708 EndAngle=2.5117
    g13: ArcOfCircle CenterX=25 CenterY=105.185 CenterZ=0 NormalX=0 NormalY=0 NormalZ=1 AngleXU=0 Radius=5 StartAngle=0.629894 EndAngle=1.5708
    g14: ArcOfCircle CenterX=-64.5 CenterY=17 CenterZ=0 NormalX=0 NormalY=0 NormalZ=1 AngleXU=0 Radius=7 StartAngle=0 EndAngle=1.5708
    g15: ArcOfCircle CenterX=-64.5 CenterY=-17 CenterZ=0 NormalX=0 NormalY=0 NormalZ=1 AngleXU=0 Radius=7 StartAngle=4.71239 EndAngle=6.28319
    g16: ArcOfCircle CenterX=64.5 CenterY=-17 CenterZ=0 NormalX=0 NormalY=0 NormalZ=1 AngleXU=0 Radius=7 StartAngle=3.14159 EndAngle=4.71239
    g17: ArcOfCircle CenterX=64.5 CenterY=17 CenterZ=0 NormalX=0 NormalY=0 NormalZ=1 AngleXU=0 Radius=7 StartAngle=1.5708 EndAngle=3.14159
    g18: GeomPoint X=0 Y=-59.8154 Z=0
    g19: LineSegment StartX=77.5 StartY=26 StartZ=0 EndX=77.5 EndY=41 EndZ=0
    g20: LineSegment StartX=77.5 StartY=-26 StartZ=0 EndX=77.5 EndY=-28 EndZ=0
    g21: LineSegment StartX=-77.5 StartY=-28 StartZ=0 EndX=-77.5 EndY=-26 EndZ=0
    g22: LineSegment StartX=-77.5 StartY=26 StartZ=0 EndX=-77.5 EndY=41 EndZ=0
    g23: ArcOfCircle CenterX=75.5 CenterY=-28 CenterZ=0 NormalX=0 NormalY=0 NormalZ=1 AngleXU=0 Radius=2 StartAngle=5.4646 EndAngle=6.28319
    g24: ArcOfCircle CenterX=75.5 CenterY=-26 CenterZ=0 NormalX=0 NormalY=0 NormalZ=1 AngleXU=0 Radius=2 StartAngle=0 EndAngle=1.5708
    g25: ArcOfCircle CenterX=-75.5 CenterY=-28 CenterZ=0 NormalX=0 NormalY=0 NormalZ=1 AngleXU=0 Radius=2 StartAngle=3.14159 EndAngle=3.96017
    g26: ArcOfCircle CenterX=-75.5 CenterY=-26 CenterZ=0 NormalX=0 NormalY=0 NormalZ=1 AngleXU=0 Radius=2 StartAngle=1.5708 EndAngle=3.14159
    g27: ArcOfCircle CenterX=75.5 CenterY=26 CenterZ=0 NormalX=0 NormalY=0 NormalZ=1 AngleXU=0 Radius=2 StartAngle=4.71239 EndAngle=6.28319
    g28: ArcOfCircle CenterX=75.5 CenterY=41 CenterZ=0 NormalX=0 NormalY=0 NormalZ=1 AngleXU=0 Radius=2 StartAngle=1.3e-15 EndAngle=0.629894
    g29: ArcOfCircle CenterX=-75.5 CenterY=26 CenterZ=0 NormalX=0 NormalY=0 NormalZ=1 AngleXU=0 Radius=2 StartAngle=3.14159 EndAngle=4.71239
    g30: ArcOfCircle CenterX=-75.5 CenterY=41 CenterZ=0 NormalX=0 NormalY=0 NormalZ=1 AngleXU=0 Radius=2 StartAngle=2.5117 EndAngle=3.14159
    g31: LineSegment StartX=-77.5 StartY=110.185 StartZ=0 EndX=-2.5 EndY=110.185 EndZ=0
    g32: LineSegment StartX=-2.5 StartY=110.185 StartZ=0 EndX=-2.5 EndY=2.5 EndZ=0
    g33: LineSegment StartX=-2.5 StartY=2.5 StartZ=0 EndX=-77.5 EndY=2.5 EndZ=0
    g34: LineSegment StartX=-77.5 StartY=2.5 StartZ=0 EndX=-77.5 EndY=110.185 EndZ=0
    g35: LineSegment StartX=2.5 StartY=2.5 StartZ=0 EndX=77.5 EndY=2.5 EndZ=0
    g36: LineSegment StartX=77.5 StartY=2.5 StartZ=0 EndX=77.5 EndY=110.185 EndZ=0
    g37: LineSegment StartX=77.5 StartY=110.185 StartZ=0 EndX=2.5 EndY=110.185 EndZ=0
    g38: LineSegment StartX=2.5 StartY=110.185 StartZ=0 EndX=2.5 EndY=2.5 EndZ=0
    g39: LineSegment StartX=-77.5 StartY=-2.5 StartZ=0 EndX=-2.5 EndY=-2.5 EndZ=0
    g40: LineSegment StartX=-2.5 StartY=-2.5 StartZ=0 EndX=-2.5 EndY=-59.8154 EndZ=0
    g41: LineSegment StartX=-2.5 StartY=-59.8154 StartZ=0 EndX=-77.5 EndY=-59.8154 EndZ=0
    g42: LineSegment StartX=-77.5 StartY=-59.8154 StartZ=0 EndX=-77.5 EndY=-2.5 EndZ=0
    g43: LineSegment StartX=2.5 StartY=-2.5 StartZ=0 EndX=77.5 EndY=-2.5 EndZ=0
    g44: LineSegment StartX=77.5 StartY=-2.5 StartZ=0 EndX=77.5 EndY=-59.8154 EndZ=0
    g45: LineSegment StartX=77.5 StartY=-59.8154 StartZ=0 EndX=2.5 EndY=-59.8154 EndZ=0
    g46: LineSegment StartX=2.5 StartY=-59.8154 StartZ=0 EndX=2.5 EndY=-2.5 EndZ=0
    g47: LineSegment StartX=-2.5 StartY=110.185 StartZ=0 EndX=2.5 EndY=110.185 EndZ=0
    g48: LineSegment StartX=-2.5 StartY=2.5 StartZ=0 EndX=2.5 EndY=2.5 EndZ=0
    g49: LineSegment StartX=-2.5 StartY=-2.5 StartZ=0 EndX=2.5 EndY=-2.5 EndZ=0
    g50: LineSegment StartX=-77.5 StartY=-2.5 StartZ=0 EndX=-77.5 EndY=2.5 EndZ=0
    g51: LineSegment StartX=-2.5 StartY=-2.5 StartZ=0 EndX=-2.5 EndY=2.5 EndZ=0
    g52: LineSegment StartX=2.5 StartY=-2.5 StartZ=0 EndX=2.5 EndY=2.5 EndZ=0
    g53: LineSegment StartX=77.5 StartY=-2.5 StartZ=0 EndX=77.5 EndY=2.5 EndZ=0
    g54: LineSegment StartX=-2.5 StartY=-59.8154 StartZ=0 EndX=2.5 EndY=-59.8154 EndZ=0
  constraints (139):
    c: Vertical(g0)
    c: Vertical(g1)
    c: Horizontal(g2)
    c: Symmetric(g2,g2,g-1)
    c: Horizontal(g3)
    c: Horizontal(g4)
    c: PointOnObject(g5,g-2)
    c: Horizontal(g6)
    c: Horizontal(g7)
    c: Horizontal(g9)
    c: Coincident(g11,g-1)
    c: PointOnObject(g11,g-2)
    c: Tangent(g8,g12) = 1.5708
    c: Tangent(g9,g12) = 1.5708
    c: Tangent(g9,g13) = 1.5708
    c: Tangent(g10,g13) = 1.5708
    c: Tangent(g6,g14) = -1.5708
    c: Tangent(g0,g14) = 1.5708
    c: Tangent(g3,g15) = 1.5708
    c: Tangent(g0,g15) = 1.5708
    c: Tangent(g1,g16) = -1.5708
    c: Tangent(g4,g16) = -1.5708
    c: Tangent(g1,g17) = -1.5708
    c: Tangent(g7,g17) = 1.5708
    c: Equal(g13,g12)
    c: Symmetric(g9,g9,g11)
    c: Equal(g16,g17)
    c: Equal(g17,g14)
    c: Equal(g14,g15)
    c: PointOnObject(g18,g-2)
    c: PointOnObject(g18,g5)
    c: DistanceX(g2,g2) = 115
    c: Symmetric(g0,g0,g2)
    c: Symmetric(g1,g1,g2)
    c: Radius(g17) = 7
    c: DistanceY(g18,g9) = 170
    c: Radius(g13) = 5
    c: DistanceX(g9,g9) = 50
    c: Equal(g7,g6)
    c: Equal(g7,g4)
    c: Vertical(g19)
    c: Vertical(g20)
    c: Vertical(g21)
    c: Vertical(g22)
    c: Equal(g3,g6)
    c: Equal(g8,g10)
    c: Tangent(g5,g23) = -1.5708
    c: Tangent(g20,g23) = 1.5708
    c: Tangent(g20,g24) = 1.5708
    c: Tangent(g4,g24) = 1.5708
    c: Tangent(g5,g25) = -1.5708
    c: Tangent(g21,g25) = 1.5708
    c: Tangent(g21,g26) = 1.5708
    c: Tangent(g3,g26) = -1.5708
    c: Equal(g26,g24)
    c: Radius(g24) = 2
    c: Equal(g23,g25)
    c: Radius(g23) = 2
    c: Tangent(g7,g27) = -1.5708
    c: Tangent(g19,g27) = -1.5708
    c: Tangent(g19,g28) = -1.5708
    c: Tangent(g10,g28) = 1.5708
    c: Tangent(g6,g29) = 1.5708
    c: Tangent(g22,g29) = 1.5708
    c: Tangent(g8,g30) = 1.5708
    c: Tangent(g22,g30) = 1.5708
    c: Equal(g27,g29)
    c: Equal(g28,g30)
    c: DistanceY(g20,g20) = 2
    c: DistanceY(g19,g19) = 15
    c: DistanceY(g4,g7) = 48
    c: DistanceX(g21,g20) = 155
    c: Radius(g27) = 2
    c: Radius(g28) = 2
    c: Diameter(g5) = 225
    c: Equal(g21,g20)
    c: Coincident(g31,g32)
    c: Coincident(g32,g33)
    c: Coincident(g33,g34)
    c: Coincident(g34,g31)
    c: Horizontal(g31)
    c: Horizontal(g33)
    c: Vertical(g32)
    c: Vertical(g34)
    c: Coincident(g35,g36)
    c: Coincident(g36,g37)
    c: Coincident(g37,g38)
    c: Coincident(g38,g35)
    c: Horizontal(g35)
    c: Horizontal(g37)
    c: Vertical(g36)
    c: Vertical(g38)
    c: Coincident(g39,g40)
    c: Coincident(g40,g41)
    c: Coincident(g41,g42)
    c: Coincident(g42,g39)
    c: Horizontal(g39)
    c: Horizontal(g41)
    c: Vertical(g40)
    c: Vertical(g42)
    c: Coincident(g43,g44)
    c: Coincident(g44,g45)
    c: Coincident(g45,g46)
    c: Coincident(g46,g43)
    c: Horizontal(g43)
    c: Horizontal(g45)
    c: Vertical(g44)
    c: Vertical(g46)
    c: Coincident(g47,g31)
    c: Coincident(g47,g37)
    c: Coincident(g48,g32)
    c: Coincident(g48,g35)
    c: Horizontal(g48)
    c: Coincident(g49,g39)
    c: Coincident(g49,g43)
    c: Horizontal(g49)
    c: Coincident(g50,g39)
    c: Coincident(g50,g33)
    c: Coincident(g51,g39)
    c: Coincident(g51,g32)
    c: Coincident(g52,g43)
    c: Coincident(g52,g35)
    c: Coincident(g53,g43)
    c: Coincident(g53,g35)
    c: Coincident(g54,g40)
    c: Coincident(g54,g45)
    c: Horizontal(g47)
    c: Horizontal(g54)
    c: Vertical(g51)
    c: Vertical(g52)
    c: Vertical(g53)
    c: Vertical(g50)
    c: Symmetric(g39,g35,g-1)
    c: PointOnObject(g37,g9)
    c: PointOnObject(g19,g36)
    c: PointOnObject(g22,g34)
    c: PointOnObject(g18,g54)
    c: Equal(g52,g48)
    c: DistanceX(g39,g43) = 5
FEATURE [Sketcher::SketchObject] Sketch045  label="Sketch_RibSubLoftBot003"
  FullyConstrained = true
  MapMode = 5
  Placement = pos=(0,0,-6) rot=(0,0,1;0rad)
  Support = -> [DatumPlane003]
  expr: Constraints[138] = Spreadsheet.rib_width_min
  expr: Constraints[74] = <<params>>.front_diameter
  expr: Constraints[69] = <<params>>.back_vert_edge
  expr: Constraints[71] = <<params>>.plate_width
  expr: Constraints[31] = <<params>>.wheel_well_plate_width
  expr: Constraints[37] = <<params>>.tail_width
  expr: Constraints[35] = <<params>>.plate_length
  expr: Constraints[73] = <<params>>.std_rad
  expr: Constraints[57] = <<params>>.std_rad
  expr: Constraints[72] = <<params>>.std_rad
  expr: Constraints[68] = <<params>>.front_vert_edge
  expr: Constraints[70] = <<params>>.wheel_well_clearance
  expr: Constraints[55] = <<params>>.std_rad
  expr: Constraints[36] = <<params>>.tail_rad
  sketch-geometry (55):
    g0: LineSegment StartX=-57.5 StartY=17 StartZ=0 EndX=-57.5 EndY=-17 EndZ=0
    g1: LineSegment StartX=57.5 StartY=17 StartZ=0 EndX=57.5 EndY=-17 EndZ=0
    g2: LineSegment StartX=-57.5 StartY=0 StartZ=0 EndX=57.5 EndY=0 EndZ=0
    g3: LineSegment StartX=-64.5 StartY=-24 StartZ=0 EndX=-75.5 EndY=-24 EndZ=0
    g4: LineSegment StartX=64.5 StartY=-24 StartZ=0 EndX=75.5 EndY=-24 EndZ=0
    g5: ArcOfCircle CenterX=0 CenterY=52.6846 CenterZ=0 NormalX=0 NormalY=0 NormalZ=1 AngleXU=0 Radius=112.5 StartAngle=3.96017 EndAngle=5.4646
    g6: LineSegment StartX=-64.5 StartY=24 StartZ=0 EndX=-75.5 EndY=24 EndZ=0
    g7: LineSegment StartX=64.5 StartY=24 StartZ=0 EndX=75.5 EndY=24 EndZ=0
    g8: LineSegment StartX=-77.1162 StartY=42.1781 StartZ=0 EndX=-29.0404 EndY=108.13 EndZ=0
    g9: LineSegment StartX=-25 StartY=110.185 StartZ=0 EndX=25 EndY=110.185 EndZ=0
    g10: LineSegment StartX=29.0404 StartY=108.13 StartZ=0 EndX=77.1162 EndY=42.1781 EndZ=0
    g11: LineSegment StartX=0 StartY=0 StartZ=0 EndX=0 EndY=110.185 EndZ=0
    g12: ArcOfCircle CenterX=-25 CenterY=105.185 CenterZ=0 NormalX=0 NormalY=0 NormalZ=1 AngleXU=0 Radius=5 StartAngle=1.5708 EndAngle=2.5117
    g13: ArcOfCircle CenterX=25 CenterY=105.185 CenterZ=0 NormalX=0 NormalY=0 NormalZ=1 AngleXU=0 Radius=5 StartAngle=0.629894 EndAngle=1.5708
    g14: ArcOfCircle CenterX=-64.5 CenterY=17 CenterZ=0 NormalX=0 NormalY=0 NormalZ=1 AngleXU=0 Radius=7 StartAngle=0 EndAngle=1.5708
    g15: ArcOfCircle CenterX=-64.5 CenterY=-17 CenterZ=0 NormalX=0 NormalY=0 NormalZ=1 AngleXU=0 Radius=7 StartAngle=4.71239 EndAngle=6.28319
    g16: ArcOfCircle CenterX=64.5 CenterY=-17 CenterZ=0 NormalX=0 NormalY=0 NormalZ=1 AngleXU=0 Radius=7 StartAngle=3.14159 EndAngle=4.71239
    g17: ArcOfCircle CenterX=64.5 CenterY=17 CenterZ=0 NormalX=0 NormalY=0 NormalZ=1 AngleXU=0 Radius=7 StartAngle=1.5708 EndAngle=3.14159
    g18: GeomPoint X=0 Y=-59.8154 Z=0
    g19: LineSegment StartX=77.5 StartY=26 StartZ=0 EndX=77.5 EndY=41 EndZ=0
    g20: LineSegment StartX=77.5 StartY=-26 StartZ=0 EndX=77.5 EndY=-28 EndZ=0
    g21: LineSegment StartX=-77.5 StartY=-28 StartZ=0 EndX=-77.5 EndY=-26 EndZ=0
    g22: LineSegment StartX=-77.5 StartY=26 StartZ=0 EndX=-77.5 EndY=41 EndZ=0
    g23: ArcOfCircle CenterX=75.5 CenterY=-28 CenterZ=0 NormalX=0 NormalY=0 NormalZ=1 AngleXU=0 Radius=2 StartAngle=5.4646 EndAngle=6.28319
    g24: ArcOfCircle CenterX=75.5 CenterY=-26 CenterZ=0 NormalX=0 NormalY=0 NormalZ=1 AngleXU=0 Radius=2 StartAngle=0 EndAngle=1.5708
    g25: ArcOfCircle CenterX=-75.5 CenterY=-28 CenterZ=0 NormalX=0 NormalY=0 NormalZ=1 AngleXU=0 Radius=2 StartAngle=3.14159 EndAngle=3.96017
    g26: ArcOfCircle CenterX=-75.5 CenterY=-26 CenterZ=0 NormalX=0 NormalY=0 NormalZ=1 AngleXU=0 Radius=2 StartAngle=1.5708 EndAngle=3.14159
    g27: ArcOfCircle CenterX=75.5 CenterY=26 CenterZ=0 NormalX=0 NormalY=0 NormalZ=1 AngleXU=0 Radius=2 StartAngle=4.71239 EndAngle=6.28319
    g28: ArcOfCircle CenterX=75.5 CenterY=41 CenterZ=0 NormalX=0 NormalY=0 NormalZ=1 AngleXU=0 Radius=2 StartAngle=1.3e-15 EndAngle=0.629894
    g29: ArcOfCircle CenterX=-75.5 CenterY=26 CenterZ=0 NormalX=0 NormalY=0 NormalZ=1 AngleXU=0 Radius=2 StartAngle=3.14159 EndAngle=4.71239
    g30: ArcOfCircle CenterX=-75.5 CenterY=41 CenterZ=0 NormalX=0 NormalY=0 NormalZ=1 AngleXU=0 Radius=2 StartAngle=2.5117 EndAngle=3.14159
    g31: LineSegment StartX=-77.5 StartY=110.185 StartZ=0 EndX=-1.5 EndY=110.185 EndZ=0
    g32: LineSegment StartX=-1.5 StartY=110.185 StartZ=0 EndX=-1.5 EndY=1.5 EndZ=0
    g33: LineSegment StartX=-1.5 StartY=1.5 StartZ=0 EndX=-77.5 EndY=1.5 EndZ=0
    g34: LineSegment StartX=-77.5 StartY=1.5 StartZ=0 EndX=-77.5 EndY=110.185 EndZ=0
    g35: LineSegment StartX=1.5 StartY=1.5 StartZ=0 EndX=77.5 EndY=1.5 EndZ=0
    g36: LineSegment StartX=77.5 StartY=1.5 StartZ=0 EndX=77.5 EndY=110.185 EndZ=0
    g37: LineSegment StartX=77.5 StartY=110.185 StartZ=0 EndX=1.5 EndY=110.185 EndZ=0
    g38: LineSegment StartX=1.5 StartY=110.185 StartZ=0 EndX=1.5 EndY=1.5 EndZ=0
    g39: LineSegment StartX=-77.5 StartY=-1.5 StartZ=0 EndX=-1.5 EndY=-1.5 EndZ=0
    g40: LineSegment StartX=-1.5 StartY=-1.5 StartZ=0 EndX=-1.5 EndY=-59.8154 EndZ=0
    g41: LineSegment StartX=-1.5 StartY=-59.8154 StartZ=0 EndX=-77.5 EndY=-59.8154 EndZ=0
    g42: LineSegment StartX=-77.5 StartY=-59.8154 StartZ=0 EndX=-77.5 EndY=-1.5 EndZ=0
    g43: LineSegment StartX=1.5 StartY=-1.5 StartZ=0 EndX=77.5 EndY=-1.5 EndZ=0
    g44: LineSegment StartX=77.5 StartY=-1.5 StartZ=0 EndX=77.5 EndY=-59.8154 EndZ=0
    g45: LineSegment StartX=77.5 StartY=-59.8154 StartZ=0 EndX=1.5 EndY=-59.8154 EndZ=0
    g46: LineSegment StartX=1.5 StartY=-59.8154 StartZ=0 EndX=1.5 EndY=-1.5 EndZ=0
    g47: LineSegment StartX=-1.5 StartY=110.185 StartZ=0 EndX=1.5 EndY=110.185 EndZ=0
    g48: LineSegment StartX=-1.5 StartY=1.5 StartZ=0 EndX=1.5 EndY=1.5 EndZ=0
    g49: LineSegment StartX=-1.5 StartY=-1.5 StartZ=0 EndX=1.5 EndY=-1.5 EndZ=0
    g50: LineSegment StartX=-77.5 StartY=-1.5 StartZ=0 EndX=-77.5 EndY=1.5 EndZ=0
    g51: LineSegment StartX=-1.5 StartY=-1.5 StartZ=0 EndX=-1.5 EndY=1.5 EndZ=0
    g52: LineSegment StartX=1.5 StartY=-1.5 StartZ=0 EndX=1.5 EndY=1.5 EndZ=0
    g53: LineSegment StartX=77.5 StartY=-1.5 StartZ=0 EndX=77.5 EndY=1.5 EndZ=0
    g54: LineSegment StartX=-1.5 StartY=-59.8154 StartZ=0 EndX=1.5 EndY=-59.8154 EndZ=0
  constraints (139):
    c: Vertical(g0)
    c: Vertical(g1)
    c: Horizontal(g2)
    c: Symmetric(g2,g2,g-1)
    c: Horizontal(g3)
    c: Horizontal(g4)
    c: PointOnObject(g5,g-2)
    c: Horizontal(g6)
    c: Horizontal(g7)
    c: Horizontal(g9)
    c: Coincident(g11,g-1)
    c: PointOnObject(g11,g-2)
    c: Tangent(g8,g12) = 1.5708
    c: Tangent(g9,g12) = 1.5708
    c: Tangent(g9,g13) = 1.5708
    c: Tangent(g10,g13) = 1.5708
    c: Tangent(g6,g14) = -1.5708
    c: Tangent(g0,g14) = 1.5708
    c: Tangent(g3,g15) = 1.5708
    c: Tangent(g0,g15) = 1.5708
    c: Tangent(g1,g16) = -1.5708
    c: Tangent(g4,g16) = -1.5708
    c: Tangent(g1,g17) = -1.5708
    c: Tangent(g7,g17) = 1.5708
    c: Equal(g13,g12)
    c: Symmetric(g9,g9,g11)
    c: Equal(g16,g17)
    c: Equal(g17,g14)
    c: Equal(g14,g15)
    c: PointOnObject(g18,g-2)
    c: PointOnObject(g18,g5)
    c: DistanceX(g2,g2) = 115
    c: Symmetric(g0,g0,g2)
    c: Symmetric(g1,g1,g2)
    c: Radius(g17) = 7
    c: DistanceY(g18,g9) = 170
    c: Radius(g13) = 5
    c: DistanceX(g9,g9) = 50
    c: Equal(g7,g6)
    c: Equal(g7,g4)
    c: Vertical(g19)
    c: Vertical(g20)
    c: Vertical(g21)
    c: Vertical(g22)
    c: Equal(g3,g6)
    c: Equal(g8,g10)
    c: Tangent(g5,g23) = -1.5708
    c: Tangent(g20,g23) = 1.5708
    c: Tangent(g20,g24) = 1.5708
    c: Tangent(g4,g24) = 1.5708
    c: Tangent(g5,g25) = -1.5708
    c: Tangent(g21,g25) = 1.5708
    c: Tangent(g21,g26) = 1.5708
    c: Tangent(g3,g26) = -1.5708
    c: Equal(g26,g24)
    c: Radius(g24) = 2
    c: Equal(g23,g25)
    c: Radius(g23) = 2
    c: Tangent(g7,g27) = -1.5708
    c: Tangent(g19,g27) = -1.5708
    c: Tangent(g19,g28) = -1.5708
    c: Tangent(g10,g28) = 1.5708
    c: Tangent(g6,g29) = 1.5708
    c: Tangent(g22,g29) = 1.5708
    c: Tangent(g8,g30) = 1.5708
    c: Tangent(g22,g30) = 1.5708
    c: Equal(g27,g29)
    c: Equal(g28,g30)
    c: DistanceY(g20,g20) = 2
    c: DistanceY(g19,g19) = 15
    c: DistanceY(g4,g7) = 48
    c: DistanceX(g21,g20) = 155
    c: Radius(g27) = 2
    c: Radius(g28) = 2
    c: Diameter(g5) = 225
    c: Equal(g21,g20)
    c: Coincident(g31,g32)
    c: Coincident(g32,g33)
    c: Coincident(g33,g34)
    c: Coincident(g34,g31)
    c: Horizontal(g31)
    c: Horizontal(g33)
    c: Vertical(g32)
    c: Vertical(g34)
    c: Coincident(g35,g36)
    c: Coincident(g36,g37)
    c: Coincident(g37,g38)
    c: Coincident(g38,g35)
    c: Horizontal(g35)
    c: Horizontal(g37)
    c: Vertical(g36)
    c: Vertical(g38)
    c: Coincident(g39,g40)
    c: Coincident(g40,g41)
    c: Coincident(g41,g42)
    c: Coincident(g42,g39)
    c: Horizontal(g39)
    c: Horizontal(g41)
    c: Vertical(g40)
    c: Vertical(g42)
    c: Coincident(g43,g44)
    c: Coincident(g44,g45)
    c: Coincident(g45,g46)
    c: Coincident(g46,g43)
    c: Horizontal(g43)
    c: Horizontal(g45)
    c: Vertical(g44)
    c: Vertical(g46)
    c: Coincident(g47,g31)
    c: Coincident(g47,g37)
    c: Coincident(g48,g32)
    c: Coincident(g48,g35)
    c: Horizontal(g48)
    c: Coincident(g49,g39)
    c: Coincident(g49,g43)
    c: Horizontal(g49)
    c: Coincident(g50,g39)
    c: Coincident(g50,g33)
    c: Coincident(g51,g39)
    c: Coincident(g51,g32)
    c: Coincident(g52,g43)
    c: Coincident(g52,g35)
    c: Coincident(g53,g43)
    c: Coincident(g53,g35)
    c: Coincident(g54,g40)
    c: Coincident(g54,g45)
    c: Horizontal(g47)
    c: Horizontal(g54)
    c: Vertical(g51)
    c: Vertical(g52)
    c: Vertical(g53)
    c: Vertical(g50)
    c: Symmetric(g39,g35,g-1)
    c: PointOnObject(g37,g9)
    c: PointOnObject(g19,g36)
    c: PointOnObject(g22,g34)
    c: PointOnObject(g18,g54)
    c: Equal(g52,g48)
    c: DistanceX(g39,g43) = 3
FEATURE [PartDesign::SubtractiveLoft] SubtractiveLoft003  label="SubLoft_Ribs_Back2"
  BaseFeature = -> SubtractiveLoft002
  Closed = false
  Profile = -> Sketch044
  Ruled = false
  Sections = -> [Sketch045]
FEATURE [Sketcher::SketchObject] Sketch046  label="Sketch_RibTrimFrontBack"
  FullyConstrained = true
  MapMode = 5
  Placement = pos=(0,0,0) rot=(0.57735,0.57735,0.57735;2.0944rad)
  Support = -> [YZ_Plane001]
  expr: Constraints[24] = <<params>>.plate_ballc_hole_loc_l
  expr: Constraints[27] = <<params>>.rib_trim_loc_front
  expr: Constraints[22] = <<params>>.rib_thick
  expr: Constraints[21] = <<params>>.plate_thick
  sketch-geometry (10):
    g0: LineSegment StartX=-58 StartY=-3 StartZ=0 EndX=-55 EndY=-6 EndZ=0
    g1: LineSegment StartX=-55 StartY=-6 StartZ=0 EndX=-88 EndY=-6 EndZ=0
    g2: LineSegment StartX=-58 StartY=-3 StartZ=0 EndX=-88 EndY=-3 EndZ=0
    g3: LineSegment StartX=-88 StartY=-3 StartZ=0 EndX=-88 EndY=-6 EndZ=0
    g4: LineSegment StartX=94.5 StartY=-3 StartZ=0 EndX=124.5 EndY=-3 EndZ=0
    g5: LineSegment StartX=94.5 StartY=-3 StartZ=0 EndX=94.5 EndY=-6 EndZ=0
    g6: LineSegment StartX=94.5 StartY=-6 StartZ=0 EndX=124.5 EndY=-6 EndZ=0
    g7: LineSegment StartX=124.5 StartY=-6 StartZ=0 EndX=124.5 EndY=-3 EndZ=0
    g8: LineSegment StartX=-55 StartY=-6 StartZ=0 EndX=94.5 EndY=-6 EndZ=0
    g9: LineSegment StartX=-58 StartY=-3 StartZ=0 EndX=94.5 EndY=-3 EndZ=0
  constraints (28):
    c: Coincident(g1,g0)
    c: Horizontal(g1)
    c: Coincident(g2,g0)
    c: Horizontal(g2)
    c: Coincident(g3,g2)
    c: Coincident(g3,g1)
    c: Vertical(g3)
    c: Horizontal(g4)
    c: Coincident(g5,g4)
    c: Vertical(g5)
    c: Coincident(g6,g5)
    c: Horizontal(g6)
    c: Coincident(g7,g6)
    c: Coincident(g7,g4)
    c: Vertical(g7)
    c: Coincident(g8,g0)
    c: Coincident(g8,g5)
    c: Horizontal(g8)
    c: Coincident(g9,g0)
    c: Coincident(g9,g4)
    c: Horizontal(g9)
    c: DistanceY(g4,g-1) = 3
    c: DistanceY(g6,g4) = 3
    c: Angle(g0,g1) = 0.785398
    c: DistanceX(g-1,g5) = 94.5
    c: Distance(g6) = 30
    c: Distance(g2) = 30
    c: DistanceX(g0,g-1) = 58
FEATURE [PartDesign::Pocket] Pocket022  label="TrimRibFrontBack"
  BaseFeature = -> SubtractiveLoft003
  Length = 5
  Length2 = 100
  Midplane = true
  Profile = -> Sketch046
  Type = 0
  expr: Length = <<params>>.rib_width_max
FEATURE [PartDesign::Chamfer] Chamfer
  Angle = 45
  Base = -> Pocket022 [Edge452,Edge477,Edge193,Edge196,Edge187]
  BaseFeature = -> Pocket022
  ChamferType = 0
  FlipDirection = false
  Size = 2
  Size2 = 1
  SupportTransform = false
FEATURE [PartDesign::Body] Body  label="PB3D_Triplate_Base"
  Group = -> [Sketch,Pad,Sketch016,Sketch017,Pocket003,Sketch018,Pocket,Sketch019,Pocket004,Sketch020,Pocket005,Sketch021,Pocket006,Sketch025,Pocket009,Sketch028,Pocket012,Sketch029,Pocket013,Sketch030,Pocket014,DatumPlane001,Sketch032,Pocket016,Sketch033,Pocket017,Sketch034,Pocket018,Sketch035,Pocket019,Sketch036,Pocket020,Sketch037,Pocket021,DatumPlane002,DatumPlane003,Sketch038,Sketch039,SubtractiveLoft,+12 more]
  Origin = -> Origin001
  Tip = -> Chamfer
FEATURE [App::Part] Part  label="PB3D_TriPlate_Base"
  Group = -> [Body]
  Origin = -> Origin
FEATURE [PartDesign::Plane] DatumPlane004  label="Datum_BallCPlate_Bottom001"
  AttachmentOffset = pos=(0,0,-3) rot=(0,0,1;0rad)
  Length = 60.198
  MapMode = 5
  Placement = pos=(0,0,-3) rot=(0,0,1;0rad)
  ResizeMode = 0
  Support = -> [XY_Plane005]
  Width = 62.198
  expr: .AttachmentOffset.Base.z = -1 * <<params>>.ballc_mt_t
FEATURE [Sketcher::SketchObject] Sketch047  label="Sketch_PlateDims001"
  FullyConstrained = true
  MapMode = 5
  Support = -> [XY_Plane005]
  expr: Constraints[18] = <<params>>.ballc_mt_l
  expr: Constraints[17] = <<params>>.ballc_mt_w
  expr: Constraints[16] = <<params>>.std_rad
  sketch-geometry (8):
    g0: LineSegment StartX=-6.5 StartY=0 StartZ=0 EndX=6.5 EndY=0 EndZ=0
    g1: LineSegment StartX=8.5 StartY=2 StartZ=0 EndX=8.5 EndY=25 EndZ=0
    g2: LineSegment StartX=6.5 StartY=27 StartZ=0 EndX=-6.5 EndY=27 EndZ=0
    g3: LineSegment StartX=-8.5 StartY=25 StartZ=0 EndX=-8.5 EndY=2 EndZ=0
    g4: ArcOfCircle CenterX=-6.5 CenterY=2 CenterZ=0 NormalX=0 NormalY=0 NormalZ=1 AngleXU=0 Radius=2 StartAngle=3.14159 EndAngle=4.71239
    g5: ArcOfCircle CenterX=6.5 CenterY=2 CenterZ=0 NormalX=0 NormalY=0 NormalZ=1 AngleXU=0 Radius=2 StartAngle=4.71239 EndAngle=6.28319
    g6: ArcOfCircle CenterX=6.5 CenterY=25 CenterZ=0 NormalX=0 NormalY=0 NormalZ=1 AngleXU=0 Radius=2 StartAngle=0 EndAngle=1.5708
    g7: ArcOfCircle CenterX=-6.5 CenterY=25 CenterZ=0 NormalX=0 NormalY=0 NormalZ=1 AngleXU=0 Radius=2 StartAngle=1.5708 EndAngle=3.14159
  constraints (19):
    c: Horizontal(g0)
    c: Horizontal(g2)
    c: Vertical(g1)
    c: Vertical(g3)
    c: Tangent(g0,g4) = -1.5708
    c: Tangent(g3,g4) = -1.5708
    c: Tangent(g0,g5) = -1.5708
    c: Tangent(g1,g5) = -1.5708
    c: Tangent(g1,g6) = -1.5708
    c: Tangent(g2,g6) = -1.5708
    c: Tangent(g2,g7) = -1.5708
    c: Tangent(g3,g7) = -1.5708
    c: Equal(g7,g6)
    c: Equal(g6,g5)
    c: Equal(g5,g4)
    c: Symmetric(g0,g0,g-1)
    c: Radius(g5) = 2
    c: DistanceX(g3,g1) = 17
    c: DistanceY(g0,g2) = 27
FEATURE [Sketcher::SketchObject] Sketch048  label="Sketch_BallCMtHoles001"
  FullyConstrained = true
  MapMode = 5
  Support = -> [XY_Plane005]
  expr: Constraints[6] = <<params>>.ballc_mt_l / 2
  expr: Constraints[4] = <<params>>.m2_hole_clear_diam
  sketch-geometry (3):
    g0: Circle CenterX=0 CenterY=5.5 CenterZ=0 NormalX=0 NormalY=0 NormalZ=1 AngleXU=0 Radius=1.2
    g1: Circle CenterX=0 CenterY=21.5 CenterZ=0 NormalX=0 NormalY=0 NormalZ=1 AngleXU=0 Radius=1.2
    g2: GeomPoint X=0 Y=13.5 Z=0
  constraints (7):
    c: PointOnObject(g0,g-2)
    c: PointOnObject(g1,g-2)
    c: DistanceY(g0,g1) = 16
    c: Equal(g1,g0)
    c: Diameter(g1) = 2.4
    c: Symmetric(g1,g0,g2)
    c: DistanceY(g-1,g2) = 13.5
FEATURE [Sketcher::SketchObject] Sketch049
  FullyConstrained = true
  MapMode = 5
  Support = -> [XY_Plane005]
  expr: Constraints[21] = <<params>>.ballc_to_plate_l
  expr: Constraints[20] = <<params>>.ballc_to_plate_w
  expr: Constraints[19] = <<params>>.ballc_to_plate_offset
  expr: Constraints[18] = <<params>>.m2_hole_clear_diam
  sketch-geometry (9):
    g0: LineSegment StartX=-5.5 StartY=24 StartZ=0 EndX=5.5 EndY=24 EndZ=0
    g1: LineSegment StartX=5.5 StartY=24 StartZ=0 EndX=5.5 EndY=3 EndZ=0
    g2: LineSegment StartX=5.5 StartY=3 StartZ=0 EndX=-5.5 EndY=3 EndZ=0
    g3: LineSegment StartX=-5.5 StartY=3 StartZ=0 EndX=-5.5 EndY=24 EndZ=0
    g4: LineSegment StartX=0 StartY=0 StartZ=0 EndX=0 EndY=3 EndZ=0
    g5: Circle CenterX=-5.5 CenterY=24 CenterZ=0 NormalX=0 NormalY=0 NormalZ=1 AngleXU=0 Radius=1.2
    g6: Circle CenterX=5.5 CenterY=24 CenterZ=0 NormalX=0 NormalY=0 NormalZ=1 AngleXU=0 Radius=1.2
    g7: Circle CenterX=5.5 CenterY=3 CenterZ=0 NormalX=0 NormalY=0 NormalZ=1 AngleXU=0 Radius=1.2
    g8: Circle CenterX=-5.5 CenterY=3 CenterZ=0 NormalX=0 NormalY=0 NormalZ=1 AngleXU=0 Radius=1.2
  constraints (22):
    c: Coincident(g0,g1)
    c: Coincident(g1,g2)
    c: Coincident(g2,g3)
    c: Coincident(g3,g0)
    c: Horizontal(g0)
    c: Horizontal(g2)
    c: Vertical(g1)
    c: Vertical(g3)
    c: Coincident(g4,g-1)
    c: PointOnObject(g4,g-2)
    c: Symmetric(g2,g1,g4)
    c: Coincident(g5,g0)
    c: Coincident(g6,g0)
    c: Coincident(g7,g1)
    c: Coincident(g8,g2)
    c: Equal(g7,g6)
    c: Equal(g6,g5)
    c: Equal(g5,g8)
    c: Diameter(g6) = 2.4
    c: DistanceY(g-1,g4) = 3
    c: DistanceX(g5,g6) = 11
    c: DistanceY(g7,g6) = 21
FEATURE [PartDesign::Pad] Pad004  label="MainPlate_Ext001"
  Direction = (1,1,1)
  Length = 3
  Length2 = 100
  Profile = -> Sketch047
  Reversed = true
  Type = 0
  expr: Length = <<params>>.ballc_mt_t
FEATURE [PartDesign::Pocket] Pocket025  label="BallCToPlateHoles001"
  BaseFeature = -> Pad004
  Length = 5
  Length2 = 100
  Profile = -> Sketch049
  Type = 1
FEATURE [Sketcher::SketchObject] Sketch050
  FullyConstrained = true
  MapMode = 5
  Support = -> [XY_Plane005]
  expr: Constraints[13] = <<params>>.ballc_to_plate_offset
  expr: Constraints[12] = <<params>>.ballc_to_plate_l
  expr: Constraints[93] = <<params>>.m2_nut_clear_flat
  expr: Constraints[11] = <<params>>.ballc_to_plate_w
  sketch-geometry (33):
    g0: LineSegment StartX=-5.5 StartY=24 StartZ=0 EndX=5.5 EndY=24 EndZ=0
    g1: LineSegment StartX=5.5 StartY=24 StartZ=0 EndX=5.5 EndY=3 EndZ=0
    g2: LineSegment StartX=5.5 StartY=3 StartZ=0 EndX=-5.5 EndY=3 EndZ=0
    g3: LineSegment StartX=-5.5 StartY=3 StartZ=0 EndX=-5.5 EndY=24 EndZ=0
    g4: LineSegment StartX=0 StartY=0 StartZ=0 EndX=0 EndY=3 EndZ=0
    g5: LineSegment StartX=4.28756 StartY=0.9 StartZ=0 EndX=6.71244 EndY=0.9 EndZ=0
    g6: LineSegment StartX=6.71244 StartY=0.9 StartZ=0 EndX=7.92487 EndY=3 EndZ=0
    g7: LineSegment StartX=7.92487 StartY=3 StartZ=0 EndX=6.71244 EndY=5.1 EndZ=0
    g8: LineSegment StartX=6.71244 StartY=5.1 StartZ=0 EndX=4.28756 EndY=5.1 EndZ=0
    g9: LineSegment StartX=4.28756 StartY=5.1 StartZ=0 EndX=3.07513 EndY=3 EndZ=0
    g10: LineSegment StartX=3.07513 StartY=3 StartZ=0 EndX=4.28756 EndY=0.9 EndZ=0
    g11: Circle CenterX=5.5 CenterY=3 CenterZ=0 NormalX=0 NormalY=0 NormalZ=1 AngleXU=0 Radius=2.42487
    g12: LineSegment StartX=6.71244 StartY=26.1 StartZ=0 EndX=4.28756 EndY=26.1 EndZ=0
    g13: LineSegment StartX=4.28756 StartY=26.1 StartZ=0 EndX=3.07513 EndY=24 EndZ=0
    g14: LineSegment StartX=3.07513 StartY=24 StartZ=0 EndX=4.28756 EndY=21.9 EndZ=0
    g15: LineSegment StartX=4.28756 StartY=21.9 StartZ=0 EndX=6.71244 EndY=21.9 EndZ=0
    g16: LineSegment StartX=6.71244 StartY=21.9 StartZ=0 EndX=7.92487 EndY=24 EndZ=0
    g17: LineSegment StartX=7.92487 StartY=24 StartZ=0 EndX=6.71244 EndY=26.1 EndZ=0
    g18: Circle CenterX=5.5 CenterY=24 CenterZ=0 NormalX=0 NormalY=0 NormalZ=1 AngleXU=0 Radius=2.42487
    g19: LineSegment StartX=-4.28756 StartY=21.9 StartZ=0 EndX=-3.07513 EndY=24 EndZ=0
    g20: LineSegment StartX=-3.07513 StartY=24 StartZ=0 EndX=-4.28756 EndY=26.1 EndZ=0
    g21: LineSegment StartX=-4.28756 StartY=26.1 StartZ=0 EndX=-6.71244 EndY=26.1 EndZ=0
    g22: LineSegment StartX=-6.71244 StartY=26.1 StartZ=0 EndX=-7.92487 EndY=24 EndZ=0
    g23: LineSegment StartX=-7.92487 StartY=24 StartZ=0 EndX=-6.71244 EndY=21.9 EndZ=0
    g24: LineSegment StartX=-6.71244 StartY=21.9 StartZ=0 EndX=-4.28756 EndY=21.9 EndZ=0
    g25: Circle CenterX=-5.5 CenterY=24 CenterZ=0 NormalX=0 NormalY=0 NormalZ=1 AngleXU=0 Radius=2.42487
    g26: LineSegment StartX=-4.28756 StartY=0.9 StartZ=0 EndX=-3.07513 EndY=3 EndZ=0
    g27: LineSegment StartX=-3.07513 StartY=3 StartZ=0 EndX=-4.28756 EndY=5.1 EndZ=0
    g28: LineSegment StartX=-4.28756 StartY=5.1 StartZ=0 EndX=-6.71244 EndY=5.1 EndZ=0
    g29: LineSegment StartX=-6.71244 StartY=5.1 StartZ=0 EndX=-7.92487 EndY=3 EndZ=0
    g30: LineSegment StartX=-7.92487 StartY=3 StartZ=0 EndX=-6.71244 EndY=0.9 EndZ=0
    g31: LineSegment StartX=-6.71244 StartY=0.9 StartZ=0 EndX=-4.28756 EndY=0.9 EndZ=0
    g32: Circle CenterX=-5.5 CenterY=3 CenterZ=0 NormalX=0 NormalY=0 NormalZ=1 AngleXU=0 Radius=2.42487
  constraints (78):
    c: Coincident(g0,g1)
    c: Coincident(g1,g2)
    c: Coincident(g2,g3)
    c: Coincident(g3,g0)
    c: Horizontal(g0)
    c: Horizontal(g2)
    c: Vertical(g1)
    c: Vertical(g3)
    c: Coincident(g4,g-1)
    c: PointOnObject(g4,g-2)
    c: Symmetric(g2,g1,g4)
    c: DistanceX(g0,g0) = 11
    c: DistanceY(g1,g0) = 21
    c: DistanceY(g-1,g4) = 3
    c: Coincident(g5,g6)
    c: Coincident(g6,g7)
    c: Coincident(g7,g8)
    c: Coincident(g8,g9)
    c: Coincident(g9,g10)
    c: Coincident(g10,g5)
    c: Equal(g5, g6-g10) x5
    c: PointOnObject(g5,g11)
    c: PointOnObject(g6,g11)
    c: PointOnObject(g7,g11)
    c: PointOnObject(g8,g11)
    c: PointOnObject(g9,g11)
    c: PointOnObject(g10,g11)
    c: Coincident(g11,g1)
    c: Coincident(g12,g13)
    c: Coincident(g13,g14)
    c: Coincident(g14,g15)
    c: Coincident(g15,g16)
    c: Coincident(g16,g17)
    c: Coincident(g17,g12)
    c: Equal(g12, g13-g17) x5
    c: PointOnObject(g12,g18)
    c: PointOnObject(g13,g18)
    c: PointOnObject(g14,g18)
    c: PointOnObject(g15,g18)
    c: PointOnObject(g16,g18)
    c: PointOnObject(g17,g18)
    c: Coincident(g18,g0)
    c: Coincident(g19,g20)
    c: Coincident(g20,g21)
    c: Coincident(g21,g22)
    c: Coincident(g22,g23)
    c: Coincident(g23,g24)
    c: Coincident(g24,g19)
    c: Equal(g19, g20-g24) x5
    c: PointOnObject(g19,g25)
    c: PointOnObject(g20,g25)
    c: PointOnObject(g21,g25)
    c: PointOnObject(g22,g25)
    c: PointOnObject(g23,g25)
    c: PointOnObject(g24,g25)
    c: Coincident(g25,g0)
    c: Coincident(g26,g27)
    c: Coincident(g27,g28)
    c: Coincident(g28,g29)
    c: Coincident(g29,g30)
    c: Coincident(g30,g31)
    c: Coincident(g31,g26)
    c: Equal(g26, g27-g31) x5
    c: PointOnObject(g26,g32)
    c: PointOnObject(g27,g32)
    c: PointOnObject(g28,g32)
    c: PointOnObject(g29,g32)
    c: PointOnObject(g30,g32)
    c: PointOnObject(g31,g32)
    c: Coincident(g32,g2)
    c: Horizontal(g15)
    c: Horizontal(g24)
    c: Horizontal(g28)
    c: Horizontal(g8)
    c: Equal(g18,g11)
    c: Equal(g18,g25)
    c: Equal(g25,g32)
    c: DistanceY(g5,g7) = 4.2
FEATURE [Sketcher::SketchObject] Sketch051  label="Sketch_BallC_Offset001"
  FullyConstrained = true
  MapMode = 5
  Placement = pos=(0,0,-3) rot=(0,0,1;0rad)
  Support = -> [DatumPlane004]
  expr: Constraints[7] = <<params>>.ballc_mt_l / 2
  sketch-geometry (11):
    g0: Circle CenterX=0 CenterY=13.5 CenterZ=0 NormalX=0 NormalY=0 NormalZ=1 AngleXU=0 Radius=8
    g1: Circle CenterX=0 CenterY=21.5 CenterZ=0 NormalX=0 NormalY=0 NormalZ=1 AngleXU=0 Radius=3
    g2: Circle CenterX=0 CenterY=5.5 CenterZ=0 NormalX=0 NormalY=0 NormalZ=1 AngleXU=0 Radius=3
    g3: ArcOfCircle CenterX=0 CenterY=13.5 CenterZ=0 NormalX=0 NormalY=0 NormalZ=1 AngleXU=0 Radius=8 StartAngle=2.08892 EndAngle=4.19427
    g4: ArcOfCircle CenterX=0 CenterY=13.5 CenterZ=0 NormalX=0 NormalY=0 NormalZ=1 AngleXU=0 Radius=8 StartAngle=5.23051 EndAngle=7.33586
    g5: ArcOfCircle CenterX=0 CenterY=21.5 CenterZ=0 NormalX=0 NormalY=0 NormalZ=1 AngleXU=0 Radius=3 StartAngle=0.137937 EndAngle=3.00366
    g6: ArcOfCircle CenterX=0 CenterY=5.5 CenterZ=0 NormalX=0 NormalY=0 NormalZ=1 AngleXU=0 Radius=3 StartAngle=3.27953 EndAngle=6.14525
    g7: ArcOfCircle CenterX=-4.95251 CenterY=22.1875 CenterZ=0 NormalX=0 NormalY=0 NormalZ=1 AngleXU=0 Radius=2 StartAngle=5.23051 EndAngle=6.14525
    g8: ArcOfCircle CenterX=4.95251 CenterY=22.1875 CenterZ=0 NormalX=0 NormalY=0 NormalZ=1 AngleXU=0 Radius=2 StartAngle=3.27953 EndAngle=4.19427
    g9: ArcOfCircle CenterX=4.95251 CenterY=4.8125 CenterZ=0 NormalX=0 NormalY=0 NormalZ=1 AngleXU=0 Radius=2 StartAngle=2.08892 EndAngle=3.00366
    g10: ArcOfCircle CenterX=-4.95251 CenterY=4.8125 CenterZ=0 NormalX=0 NormalY=0 NormalZ=1 AngleXU=0 Radius=2 StartAngle=0.137937 EndAngle=1.05267
  constraints (28):
    c: PointOnObject(g0,g-2)
    c: PointOnObject(g1,g-2)
    c: Symmetric(g1,g2,g0)
    c: Equal(g1,g2)
    c: Diameter(g0) = 16
    c: Radius(g2) = 3
    c: DistanceY(g2,g1) = 16
    c: DistanceY(g-1,g0) = 13.5
    c: Coincident(g3,g0)
    c: Coincident(g4,g3)
    c: Coincident(g5,g1)
    c: Coincident(g6,g2)
    c: Tangent(g3,g7) = 1.5708
    c: Tangent(g5,g7) = 1.5708
    c: Tangent(g5,g8) = 1.5708
    c: Tangent(g4,g8) = 1.5708
    c: Tangent(g4,g9) = 1.5708
    c: Tangent(g6,g9) = 1.5708
    c: Tangent(g6,g10) = 1.5708
    c: Tangent(g3,g10) = 1.5708
    c: Equal(g7,g8)
    c: Equal(g8,g9)
    c: Equal(g9,g10)
    c: Radius(g8) = 2
    c: PointOnObject(g3,g0)
    c: PointOnObject(g4,g0)
    c: PointOnObject(g6,g2)
    c: PointOnObject(g5,g1)
FEATURE [PartDesign::Pad] Pad003  label="BallCOffset001"
  BaseFeature = -> Pocket025
  Direction = (1,1,1)
  Length = 1
  Length2 = 100
  Profile = -> Sketch051
  Reversed = true
  Type = 0
  expr: Length = <<params>>.ballc_mt_thick_inset
FEATURE [PartDesign::Pocket] Pocket023  label="BallCMtHoles001"
  BaseFeature = -> Pad003
  Length = 5
  Length2 = 100
  Midplane = true
  Profile = -> Sketch048
  Type = 1
FEATURE [PartDesign::Pocket] Pocket024  label="BallCMtCSunk001"
  BaseFeature = -> Pocket023
  Length = 1.75
  Length2 = 100
  Profile = -> Sketch050
  Type = 0
  expr: Length = <<params>>.m2_nut_min_depth
FEATURE [Sketcher::SketchObject] Sketch052
  FullyConstrained = true
  MapMode = 5
  Support = -> [XY_Plane005]
  expr: Constraints[4] = 16
  expr: Constraints[5] = <<params>>.m2_head_clear_diam
  expr: Constraints[6] = <<params>>.ballc_mt_l / 2
  sketch-geometry (3):
    g0: Circle CenterX=0 CenterY=21.5 CenterZ=0 NormalX=0 NormalY=0 NormalZ=1 AngleXU=0 Radius=2.1
    g1: Circle CenterX=0 CenterY=5.5 CenterZ=0 NormalX=0 NormalY=0 NormalZ=1 AngleXU=0 Radius=2.1
    g2: GeomPoint X=0 Y=13.5 Z=0
  constraints (7):
    c: PointOnObject(g0,g-2)
    c: PointOnObject(g2,g-2)
    c: Symmetric(g0,g1,g2)
    c: Equal(g0,g1)
    c: DistanceY(g1,g0) = 16
    c: Diameter(g0) = 4.2
    c: DistanceY(g-1,g2) = 13.5
FEATURE [PartDesign::Pocket] Pocket026  label="Pocket_HeadMtCSunk"
  BaseFeature = -> Pocket024
  Length = 2.4
  Length2 = 100
  Profile = -> Sketch052
  Type = 0
  expr: Length = <<params>>.ballc_mt_t + <<params>>.ballc_mt_thick_inset - 1.6mm
FEATURE [PartDesign::Body] Body002  label="PB3D_Triplate_BallCastMt001"
  Group = -> [Sketch047,Pad004,Sketch048,Sketch049,Pocket025,Sketch051,DatumPlane004,Pad003,Pocket023,Sketch050,Pocket024,Sketch052,Pocket026]
  Origin = -> Origin004
  Tip = -> Pocket026
FEATURE [App::Part] Part002  label="PB3D_TriPlate_BallCastMt_DFRob"
  Group = -> [Body002]
  Origin = -> Origin005
  Placement = pos=(0,81,3) rot=(0,0,1;0rad)
FEATURE [Mesh::Feature] Mesh  label="PB3D_Triplate_BallCastMt001 (Meshed)"
FEATURE [Mesh::Feature] Mesh001  label="PB3D_Triplate_Base (Meshed)"
